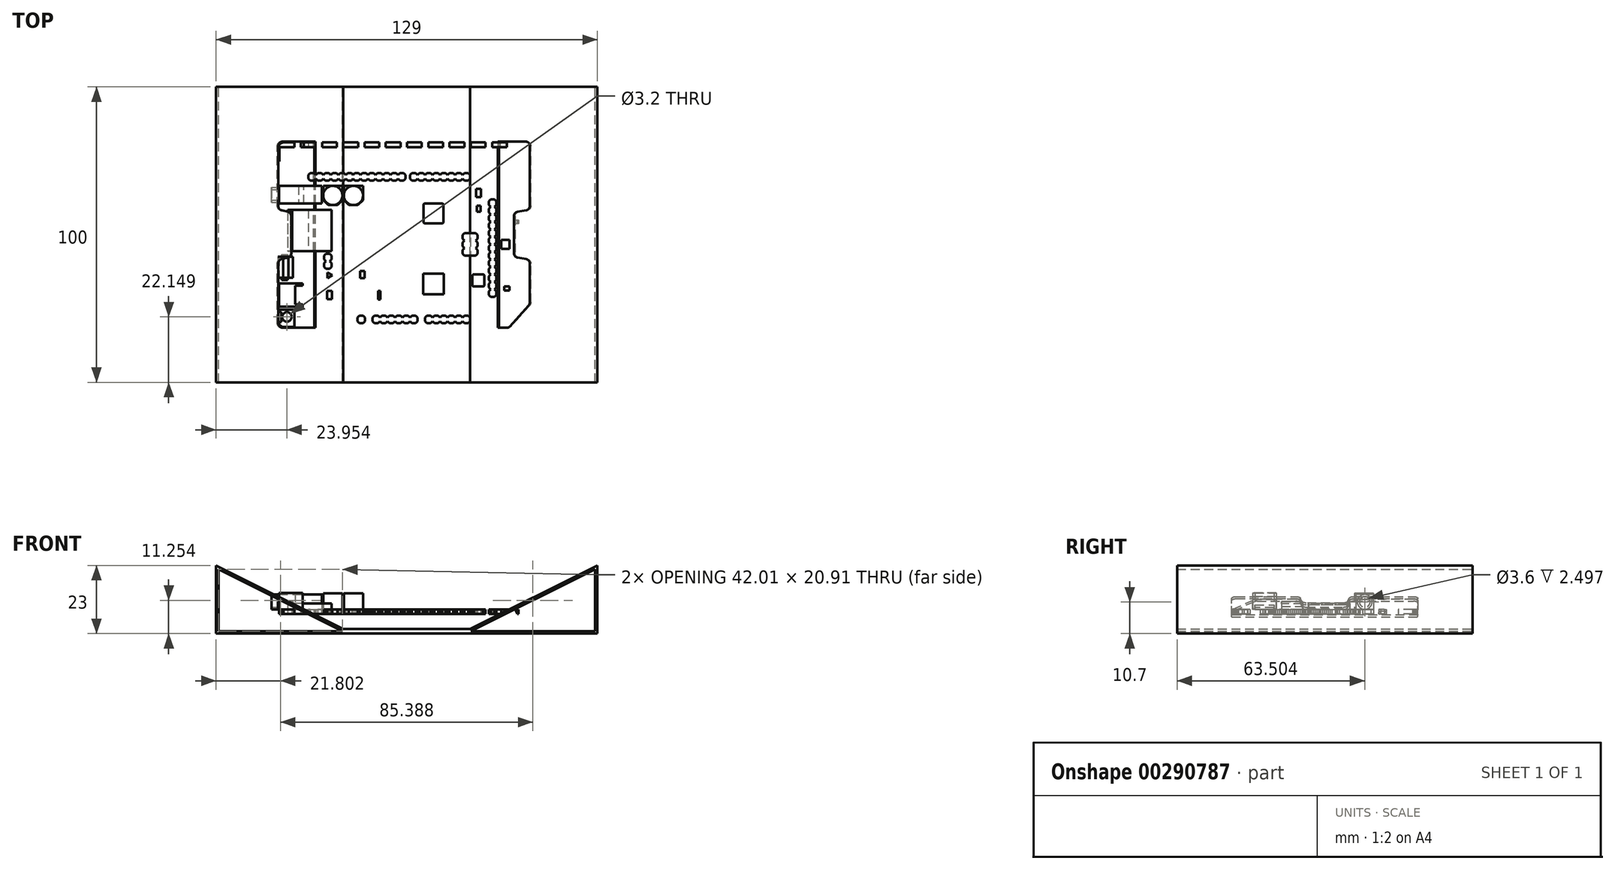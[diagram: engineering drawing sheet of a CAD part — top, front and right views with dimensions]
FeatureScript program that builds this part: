
annotation { "Feature Type Name" : "Feature", "Feature Type Description" : "" }
export const myFeature = defineFeature(function(context is Context, id is Id, definition is map)
    precondition{}
    {
        {
            var Q0;
            Q0=qCreatedBy(makeId("Top.planeOp"),FACE);
            var sketch = newSketch(context, id + "F0", { "sketchPlane" : qUnion([Q0])});
            skLineSegment(sketch, "E0", {"start": v(-41.68, 28.46) * mm, "end": v(-41.68, -30.97) * mm});
            skFitSpline(sketch, "E1", {"points": [v(-41.68, -30.97) * mm, v(-41.68, -31.8) * mm, v(-41.01, -32.47) * mm, v(-40.18, -32.47) * mm]});
            skLineSegment(sketch, "E2", {"start": v(-40.18, -32.47) * mm, "end": v(34.93, -32.47) * mm});
            skFitSpline(sketch, "E3", {"points": [v(-40.18, 29.96) * mm, v(-41.01, 29.96) * mm, v(-41.68, 29.29) * mm, v(-41.68, 28.46) * mm]});
            skLineSegment(sketch, "E4", {"start": v(-40.18, 29.96) * mm, "end": v(41.32, 29.96) * mm});
            skFitSpline(sketch, "E5", {"points": [v(42.82, 28.46) * mm, v(42.82, 29.29) * mm, v(42.15, 29.96) * mm, v(41.32, 29.96) * mm]});
            skLineSegment(sketch, "E6", {"start": v(42.82, 28.46) * mm, "end": v(42.82, -24.58) * mm});
            skLineSegment(sketch, "E7", {"start": v(42.82, -24.58) * mm, "end": v(34.93, -32.47) * mm});
            skLineSegment(sketch, "E8", {"start": v(-23.54, -14.96) * mm, "end": v(-25.32, -14.08) * mm});
            skLineSegment(sketch, "E9", {"start": v(-25.32, -14.08) * mm, "end": v(-25.32, -14.96) * mm});
            skLineSegment(sketch, "E10", {"start": v(-25.32, -14.96) * mm, "end": v(-25.32, -15.98) * mm});
            skLineSegment(sketch, "E11", {"start": v(-25.32, -15.98) * mm, "end": v(-23.54, -14.96) * mm});
            skLineSegment(sketch, "E12", {"start": v(-25.32, -14.96) * mm, "end": v(-25.95, -14.96) * mm});
            skLineSegment(sketch, "E13", {"start": v(-23.54, -14.96) * mm, "end": v(-23.16, -14.96) * mm});
            skLineSegment(sketch, "E14", {"start": v(-24.84, -27.62) * mm, "end": v(-24.35, -27.62) * mm});
            skLineSegment(sketch, "E15", {"start": v(-24.6, -27.38) * mm, "end": v(-24.6, -27.87) * mm});
            skLineSegment(sketch, "E16", {"start": v(-22.3, -27.62) * mm, "end": v(-21.8, -27.62) * mm});
            skLineSegment(sketch, "E17", {"start": v(-22.06, -27.38) * mm, "end": v(-22.06, -27.87) * mm});
            skLineSegment(sketch, "E18", {"start": v(-19.76, -27.62) * mm, "end": v(-19.27, -27.62) * mm});
            skLineSegment(sketch, "E19", {"start": v(-19.52, -27.38) * mm, "end": v(-19.52, -27.87) * mm});
            skLineSegment(sketch, "E20", {"start": v(-17.23, -27.62) * mm, "end": v(-16.74, -27.62) * mm});
            skLineSegment(sketch, "E21", {"start": v(-16.98, -27.38) * mm, "end": v(-16.98, -27.87) * mm});
            skLineSegment(sketch, "E22", {"start": v(-24.52, -31.43) * mm, "end": v(-24.03, -31.43) * mm});
            skLineSegment(sketch, "E23", {"start": v(-21.98, -31.43) * mm, "end": v(-21.5, -31.43) * mm});
            skLineSegment(sketch, "E24", {"start": v(-19.45, -31.43) * mm, "end": v(-18.96, -31.43) * mm});
            skLineSegment(sketch, "E25", {"start": v(-16.9, -31.43) * mm, "end": v(-16.42, -31.43) * mm});
            skLineSegment(sketch, "E26", {"start": v(-22.82, -17.79) * mm, "end": v(-22.33, -17.79) * mm});
            skLineSegment(sketch, "E27", {"start": v(-22.58, -17.54) * mm, "end": v(-22.58, -18.03) * mm});
            skLineSegment(sketch, "E28", {"start": v(-26.68, -17.86) * mm, "end": v(-26.19, -17.86) * mm});
            skLineSegment(sketch, "E29", {"start": v(-38.87, -9.81) * mm, "end": v(-38.5, -10.37) * mm});
            skLineSegment(sketch, "E30", {"start": v(-38.5, -9.81) * mm, "end": v(-38.87, -10.37) * mm});
            skLineSegment(sketch, "E31", {"start": v(-38.3, -10) * mm, "end": v(-38.12, -9.81) * mm});
            skLineSegment(sketch, "E32", {"start": v(-38.12, -9.81) * mm, "end": v(-38.12, -10.37) * mm});
            skLineSegment(sketch, "E33", {"start": v(-38.3, -10.37) * mm, "end": v(-37.93, -10.37) * mm});
            skLineSegment(sketch, "E34", {"start": v(19.2, -17.12) * mm, "end": v(19.2, -17.06) * mm});
            skLineSegment(sketch, "E35", {"start": v(4.38, -13) * mm, "end": v(4.38, -12.94) * mm});
            skLineSegment(sketch, "E36", {"start": v(13.53, -10.11) * mm, "end": v(13.47, -10.11) * mm});
            skLineSegment(sketch, "E37", {"start": v(8.14, -7.42) * mm, "end": v(8.08, -7.42) * mm});
            skLineSegment(sketch, "E38", {"start": v(15.4, -23.94) * mm, "end": v(15.4, -23.88) * mm});
            skLineSegment(sketch, "E39", {"start": v(19.2, -18.39) * mm, "end": v(19.2, -18.33) * mm});
            skLineSegment(sketch, "E40", {"start": v(5.89, -23.88) * mm, "end": v(5.89, -23.94) * mm});
            skLineSegment(sketch, "E41", {"start": v(-5.24, -16.93) * mm, "end": v(-5.18, -16.93) * mm});
            skLineSegment(sketch, "E42", {"start": v(17.9, -10.11) * mm, "end": v(17.97, -10.11) * mm});
            skLineSegment(sketch, "E43", {"start": v(-24.56, -19.44) * mm, "end": v(-24.56, -19.5) * mm});
            skLineSegment(sketch, "E44", {"start": v(1.13, 2.22) * mm, "end": v(1.13, 2.29) * mm});
            skLineSegment(sketch, "E45", {"start": v(1.13, 9.58) * mm, "end": v(1.13, 9.52) * mm});
            skLineSegment(sketch, "E46", {"start": v(39.79, -4.56) * mm, "end": v(39.85, -4.56) * mm});
            skLineSegment(sketch, "E47", {"start": v(37.1, -8.69) * mm, "end": v(37.15, -8.69) * mm});
            skLineSegment(sketch, "E48", {"start": v(18.57, 6.88) * mm, "end": v(18.57, 6.82) * mm});
            skLineSegment(sketch, "E49", {"start": v(29.67, 13.8) * mm, "end": v(29.67, 13.86) * mm});
            skLineSegment(sketch, "E50", {"start": v(21.1, 8.73) * mm, "end": v(21.1, 8.79) * mm});
            skLineSegment(sketch, "E51", {"start": v(21.1, 3.02) * mm, "end": v(21.1, 3.08) * mm});
            skLineSegment(sketch, "E52", {"start": v(25.86, 15.39) * mm, "end": v(25.86, 15.45) * mm});
            skLineSegment(sketch, "E53", {"start": v(25.86, 5.47) * mm, "end": v(25.86, 5.54) * mm});
            skLineSegment(sketch, "E54", {"start": v(3.95, 3.36) * mm, "end": v(4.01, 3.36) * mm});
            skLineSegment(sketch, "E55", {"start": v(10.61, -1.87) * mm, "end": v(10.67, -1.87) * mm});
            skLineSegment(sketch, "E56", {"start": v(3.95, 8.83) * mm, "end": v(4.01, 8.83) * mm});
            skLineSegment(sketch, "E57", {"start": v(18.57, 4.98) * mm, "end": v(18.57, 4.92) * mm});
            skLineSegment(sketch, "E58", {"start": v(-26.86, -14.03) * mm, "end": v(-26.86, -13.58) * mm});
            skLineSegment(sketch, "E59", {"start": v(-26.86, -13.58) * mm, "end": v(-22.26, -13.58) * mm});
            skLineSegment(sketch, "E60", {"start": v(-22.26, -13.58) * mm, "end": v(-22.26, -14.03) * mm});
            skLineSegment(sketch, "E61", {"start": v(-22.26, -16.03) * mm, "end": v(-22.26, -16.48) * mm});
            skLineSegment(sketch, "E62", {"start": v(-22.26, -16.48) * mm, "end": v(-26.86, -16.48) * mm});
            skLineSegment(sketch, "E63", {"start": v(-26.86, -16.48) * mm, "end": v(-26.86, -16.03) * mm});
            skLineSegment(sketch, "E64", {"start": v(-23.56, -14.03) * mm, "end": v(-23.56, -16.03) * mm});
            skLineSegment(sketch, "E65", {"start": v(-14.26, -15.9) * mm, "end": v(-14.26, -13.51) * mm});
            skLineSegment(sketch, "E66", {"start": v(-14.26, -13.51) * mm, "end": v(-12.66, -13.51) * mm});
            skLineSegment(sketch, "E67", {"start": v(-12.66, -13.51) * mm, "end": v(-12.66, -15.9) * mm});
            skLineSegment(sketch, "E68", {"start": v(-12.66, -15.9) * mm, "end": v(-14.26, -15.9) * mm});
            skLineSegment(sketch, "E69", {"start": v(-31.28, -12.8) * mm, "end": v(-31.28, -10.9) * mm});
            skLineSegment(sketch, "E70", {"start": v(-27.98, -12.8) * mm, "end": v(-27.98, -10.9) * mm});
            skLineSegment(sketch, "E71", {"start": v(-31.28, -12.75) * mm, "end": v(-31.28, -12.87) * mm});
            skLineSegment(sketch, "E72", {"start": v(-31.28, -12.87) * mm, "end": v(-31.03, -12.87) * mm});
            skLineSegment(sketch, "E73", {"start": v(-31.28, -10.97) * mm, "end": v(-31.28, -10.84) * mm});
            skLineSegment(sketch, "E74", {"start": v(-31.28, -10.84) * mm, "end": v(-31.03, -10.84) * mm});
            skLineSegment(sketch, "E75", {"start": v(-27.98, -12.75) * mm, "end": v(-27.98, -12.87) * mm});
            skLineSegment(sketch, "E76", {"start": v(-27.98, -12.87) * mm, "end": v(-28.24, -12.87) * mm});
            skLineSegment(sketch, "E77", {"start": v(-27.98, -10.97) * mm, "end": v(-27.98, -10.84) * mm});
            skLineSegment(sketch, "E78", {"start": v(-27.98, -10.84) * mm, "end": v(-28.24, -10.84) * mm});
            skLineSegment(sketch, "E79", {"start": v(-6.13, -15.63) * mm, "end": v(-6.13, -18.23) * mm});
            skLineSegment(sketch, "E80", {"start": v(-9.37, -18.23) * mm, "end": v(-9.37, -15.63) * mm});
            skFitSpline(sketch, "E81", {"points": [v(-6.13, -15.63) * mm, v(-6.13, -15.45) * mm, v(-6.27, -15.3) * mm, v(-6.45, -15.3) * mm]});
            skFitSpline(sketch, "E82", {"points": [v(-9.05, -15.3) * mm, v(-9.23, -15.3) * mm, v(-9.37, -15.45) * mm, v(-9.37, -15.63) * mm]});
            skFitSpline(sketch, "E83", {"points": [v(-9.37, -18.23) * mm, v(-9.37, -18.4) * mm, v(-9.23, -18.56) * mm, v(-9.05, -18.56) * mm]});
            skFitSpline(sketch, "E84", {"points": [v(-6.45, -18.56) * mm, v(-6.27, -18.56) * mm, v(-6.13, -18.4) * mm, v(-6.13, -18.23) * mm]});
            skLineSegment(sketch, "E85", {"start": v(-24.13, -23.1) * mm, "end": v(-24.99, -23.1) * mm});
            skLineSegment(sketch, "E86", {"start": v(-24.99, -20.27) * mm, "end": v(-24.13, -20.27) * mm});
            skLineSegment(sketch, "E87", {"start": v(-23.75, -21.42) * mm, "end": v(-23.75, -21.96) * mm});
            skLineSegment(sketch, "E88", {"start": v(-16.63, 2.1) * mm, "end": v(-20.44, 2.1) * mm});
            skLineSegment(sketch, "E89", {"start": v(-16.63, -2.98) * mm, "end": v(-20.44, -2.98) * mm});
            skLineSegment(sketch, "E90", {"start": v(-16.63, 2.1) * mm, "end": v(-16.63, 1.78) * mm});
            skLineSegment(sketch, "E91", {"start": v(-20.44, 2.1) * mm, "end": v(-20.44, 1.78) * mm});
            skLineSegment(sketch, "E92", {"start": v(-16.63, -2.98) * mm, "end": v(-16.63, -2.66) * mm});
            skLineSegment(sketch, "E93", {"start": v(-20.44, -2.98) * mm, "end": v(-20.44, -2.66) * mm});
            skLineSegment(sketch, "E94", {"start": v(36.56, -5.56) * mm, "end": v(36.56, -6.06) * mm});
            skLineSegment(sketch, "E95", {"start": v(36.56, -6.06) * mm, "end": v(36.06, -6.06) * mm});
            skLineSegment(sketch, "E96", {"start": v(33.56, -6.06) * mm, "end": v(34.06, -6.06) * mm});
            skLineSegment(sketch, "E97", {"start": v(36.56, -3.07) * mm, "end": v(36.06, -3.07) * mm});
            skLineSegment(sketch, "E98", {"start": v(33.56, -3.07) * mm, "end": v(34.06, -3.07) * mm});
            skLineSegment(sketch, "E99", {"start": v(33.56, -5.56) * mm, "end": v(33.56, -6.06) * mm});
            skLineSegment(sketch, "E100", {"start": v(33.56, -3.56) * mm, "end": v(33.56, -3.07) * mm});
            skLineSegment(sketch, "E101", {"start": v(36.56, -3.56) * mm, "end": v(36.56, -3.07) * mm});
            skLineSegment(sketch, "E102", {"start": v(25.44, 14.3) * mm, "end": v(26.3, 14.3) * mm});
            skLineSegment(sketch, "E103", {"start": v(26.3, 11.46) * mm, "end": v(25.44, 11.46) * mm});
            skLineSegment(sketch, "E104", {"start": v(25.06, 12.61) * mm, "end": v(25.06, 13.15) * mm});
            skLineSegment(sketch, "E105", {"start": v(21.1, -0.76) * mm, "end": v(20.47, -1.4) * mm});
            skLineSegment(sketch, "E106", {"start": v(20.47, -2.66) * mm, "end": v(21.1, -3.3) * mm});
            skLineSegment(sketch, "E107", {"start": v(21.1, -3.3) * mm, "end": v(20.47, -3.93) * mm});
            skLineSegment(sketch, "E108", {"start": v(20.47, -5.2) * mm, "end": v(21.1, -5.83) * mm});
            skLineSegment(sketch, "E109", {"start": v(21.1, -0.76) * mm, "end": v(24.91, -0.76) * mm});
            skLineSegment(sketch, "E110", {"start": v(24.91, -0.76) * mm, "end": v(25.55, -1.4) * mm});
            skLineSegment(sketch, "E111", {"start": v(25.55, -1.4) * mm, "end": v(25.55, -2.66) * mm});
            skLineSegment(sketch, "E112", {"start": v(25.55, -2.66) * mm, "end": v(24.91, -3.3) * mm});
            skLineSegment(sketch, "E113", {"start": v(24.91, -3.3) * mm, "end": v(25.55, -3.93) * mm});
            skLineSegment(sketch, "E114", {"start": v(25.55, -3.93) * mm, "end": v(25.55, -5.2) * mm});
            skLineSegment(sketch, "E115", {"start": v(25.55, -5.2) * mm, "end": v(24.91, -5.83) * mm});
            skLineSegment(sketch, "E116", {"start": v(24.91, -3.3) * mm, "end": v(21.1, -3.3) * mm});
            skLineSegment(sketch, "E117", {"start": v(24.91, -5.83) * mm, "end": v(21.1, -5.83) * mm});
            skLineSegment(sketch, "E118", {"start": v(20.47, -3.93) * mm, "end": v(20.47, -5.2) * mm});
            skLineSegment(sketch, "E119", {"start": v(20.47, -1.4) * mm, "end": v(20.47, -2.66) * mm});
            skLineSegment(sketch, "E120", {"start": v(21.1, -5.83) * mm, "end": v(20.47, -6.47) * mm});
            skLineSegment(sketch, "E121", {"start": v(20.47, -7.73) * mm, "end": v(21.1, -8.37) * mm});
            skLineSegment(sketch, "E122", {"start": v(24.91, -5.83) * mm, "end": v(25.55, -6.47) * mm});
            skLineSegment(sketch, "E123", {"start": v(25.55, -6.47) * mm, "end": v(25.55, -7.73) * mm});
            skLineSegment(sketch, "E124", {"start": v(25.55, -7.73) * mm, "end": v(24.91, -8.37) * mm});
            skLineSegment(sketch, "E125", {"start": v(24.91, -8.37) * mm, "end": v(21.1, -8.37) * mm});
            skLineSegment(sketch, "E126", {"start": v(20.47, -6.47) * mm, "end": v(20.47, -7.73) * mm});
            skLineSegment(sketch, "E127", {"start": v(0.81, -28.66) * mm, "end": v(2.08, -28.66) * mm});
            skLineSegment(sketch, "E128", {"start": v(2.08, -28.66) * mm, "end": v(2.71, -29.3) * mm});
            skLineSegment(sketch, "E129", {"start": v(2.71, -29.3) * mm, "end": v(2.71, -30.57) * mm});
            skLineSegment(sketch, "E130", {"start": v(2.71, -30.57) * mm, "end": v(2.08, -31.2) * mm});
            skLineSegment(sketch, "E131", {"start": v(-2.36, -29.3) * mm, "end": v(-1.73, -28.66) * mm});
            skLineSegment(sketch, "E132", {"start": v(-1.73, -28.66) * mm, "end": v(-0.46, -28.66) * mm});
            skLineSegment(sketch, "E133", {"start": v(-0.46, -28.66) * mm, "end": v(0.18, -29.3) * mm});
            skLineSegment(sketch, "E134", {"start": v(0.18, -29.3) * mm, "end": v(0.18, -30.57) * mm});
            skLineSegment(sketch, "E135", {"start": v(0.18, -30.57) * mm, "end": v(-0.46, -31.2) * mm});
            skLineSegment(sketch, "E136", {"start": v(-0.46, -31.2) * mm, "end": v(-1.73, -31.2) * mm});
            skLineSegment(sketch, "E137", {"start": v(-1.73, -31.2) * mm, "end": v(-2.36, -30.57) * mm});
            skLineSegment(sketch, "E138", {"start": v(0.81, -28.66) * mm, "end": v(0.18, -29.3) * mm});
            skLineSegment(sketch, "E139", {"start": v(0.18, -30.57) * mm, "end": v(0.81, -31.2) * mm});
            skLineSegment(sketch, "E140", {"start": v(2.08, -31.2) * mm, "end": v(0.81, -31.2) * mm});
            skLineSegment(sketch, "E141", {"start": v(-6.8, -28.66) * mm, "end": v(-5.53, -28.66) * mm});
            skLineSegment(sketch, "E142", {"start": v(-5.53, -28.66) * mm, "end": v(-4.9, -29.3) * mm});
            skLineSegment(sketch, "E143", {"start": v(-4.9, -29.3) * mm, "end": v(-4.9, -30.57) * mm});
            skLineSegment(sketch, "E144", {"start": v(-4.9, -30.57) * mm, "end": v(-5.53, -31.2) * mm});
            skLineSegment(sketch, "E145", {"start": v(-4.9, -29.3) * mm, "end": v(-4.26, -28.66) * mm});
            skLineSegment(sketch, "E146", {"start": v(-4.26, -28.66) * mm, "end": v(-3, -28.66) * mm});
            skLineSegment(sketch, "E147", {"start": v(-3, -28.66) * mm, "end": v(-2.36, -29.3) * mm});
            skLineSegment(sketch, "E148", {"start": v(-2.36, -29.3) * mm, "end": v(-2.36, -30.57) * mm});
            skLineSegment(sketch, "E149", {"start": v(-2.36, -30.57) * mm, "end": v(-3, -31.2) * mm});
            skLineSegment(sketch, "E150", {"start": v(-3, -31.2) * mm, "end": v(-4.26, -31.2) * mm});
            skLineSegment(sketch, "E151", {"start": v(-4.26, -31.2) * mm, "end": v(-4.9, -30.57) * mm});
            skLineSegment(sketch, "E152", {"start": v(-9.97, -29.3) * mm, "end": v(-9.34, -28.66) * mm});
            skLineSegment(sketch, "E153", {"start": v(-9.34, -28.66) * mm, "end": v(-8.07, -28.66) * mm});
            skLineSegment(sketch, "E154", {"start": v(-8.07, -28.66) * mm, "end": v(-7.43, -29.3) * mm});
            skLineSegment(sketch, "E155", {"start": v(-7.43, -29.3) * mm, "end": v(-7.43, -30.57) * mm});
            skLineSegment(sketch, "E156", {"start": v(-7.43, -30.57) * mm, "end": v(-8.07, -31.2) * mm});
            skLineSegment(sketch, "E157", {"start": v(-8.07, -31.2) * mm, "end": v(-9.34, -31.2) * mm});
            skLineSegment(sketch, "E158", {"start": v(-9.34, -31.2) * mm, "end": v(-9.97, -30.57) * mm});
            skLineSegment(sketch, "E159", {"start": v(-6.8, -28.66) * mm, "end": v(-7.43, -29.3) * mm});
            skLineSegment(sketch, "E160", {"start": v(-7.43, -30.57) * mm, "end": v(-6.8, -31.2) * mm});
            skLineSegment(sketch, "E161", {"start": v(-5.53, -31.2) * mm, "end": v(-6.8, -31.2) * mm});
            skLineSegment(sketch, "E162", {"start": v(-14.41, -28.66) * mm, "end": v(-13.14, -28.66) * mm});
            skLineSegment(sketch, "E163", {"start": v(-13.14, -28.66) * mm, "end": v(-12.5, -29.3) * mm});
            skLineSegment(sketch, "E164", {"start": v(-12.5, -29.3) * mm, "end": v(-12.5, -30.57) * mm});
            skLineSegment(sketch, "E165", {"start": v(-12.5, -30.57) * mm, "end": v(-13.14, -31.2) * mm});
            skLineSegment(sketch, "E166", {"start": v(-12.5, -29.3) * mm, "end": v(-11.87, -28.66) * mm});
            skLineSegment(sketch, "E167", {"start": v(-11.87, -28.66) * mm, "end": v(-10.6, -28.66) * mm});
            skLineSegment(sketch, "E168", {"start": v(-10.6, -28.66) * mm, "end": v(-9.97, -29.3) * mm});
            skLineSegment(sketch, "E169", {"start": v(-9.97, -29.3) * mm, "end": v(-9.97, -30.57) * mm});
            skLineSegment(sketch, "E170", {"start": v(-10.66, -30.05) * mm, "end": v(-11.3, -30.68) * mm});
            skLineSegment(sketch, "E171", {"start": v(-10.6, -31.2) * mm, "end": v(-11.87, -31.2) * mm});
            skLineSegment(sketch, "E172", {"start": v(-11.87, -31.2) * mm, "end": v(-12.5, -30.57) * mm});
            skLineSegment(sketch, "E173", {"start": v(-15.04, -29.3) * mm, "end": v(-15.04, -30.57) * mm});
            skLineSegment(sketch, "E174", {"start": v(-14.41, -28.66) * mm, "end": v(-15.04, -29.3) * mm});
            skLineSegment(sketch, "E175", {"start": v(-15.04, -30.57) * mm, "end": v(-14.41, -31.2) * mm});
            skLineSegment(sketch, "E176", {"start": v(-13.14, -31.2) * mm, "end": v(-14.41, -31.2) * mm});
            skLineSegment(sketch, "E177", {"start": v(3.35, -28.66) * mm, "end": v(4.62, -28.66) * mm});
            skLineSegment(sketch, "E178", {"start": v(4.62, -28.66) * mm, "end": v(5.25, -29.3) * mm});
            skLineSegment(sketch, "E179", {"start": v(5.25, -29.3) * mm, "end": v(5.25, -30.57) * mm});
            skLineSegment(sketch, "E180", {"start": v(5.25, -30.57) * mm, "end": v(4.62, -31.2) * mm});
            skLineSegment(sketch, "E181", {"start": v(3.35, -28.66) * mm, "end": v(2.71, -29.3) * mm});
            skLineSegment(sketch, "E182", {"start": v(2.71, -30.57) * mm, "end": v(3.35, -31.2) * mm});
            skLineSegment(sketch, "E183", {"start": v(4.62, -31.2) * mm, "end": v(3.35, -31.2) * mm});
            skLineSegment(sketch, "E184", {"start": v(16.03, -28.66) * mm, "end": v(17.3, -28.66) * mm});
            skLineSegment(sketch, "E185", {"start": v(17.3, -28.66) * mm, "end": v(17.94, -29.3) * mm});
            skLineSegment(sketch, "E186", {"start": v(17.94, -29.3) * mm, "end": v(17.94, -30.57) * mm});
            skLineSegment(sketch, "E187", {"start": v(17.94, -30.57) * mm, "end": v(17.3, -31.2) * mm});
            skLineSegment(sketch, "E188", {"start": v(17.94, -29.3) * mm, "end": v(18.57, -28.66) * mm});
            skLineSegment(sketch, "E189", {"start": v(18.57, -28.66) * mm, "end": v(19.84, -28.66) * mm});
            skLineSegment(sketch, "E190", {"start": v(19.84, -28.66) * mm, "end": v(20.47, -29.3) * mm});
            skLineSegment(sketch, "E191", {"start": v(20.47, -29.3) * mm, "end": v(20.47, -30.57) * mm});
            skLineSegment(sketch, "E192", {"start": v(20.47, -30.57) * mm, "end": v(19.84, -31.2) * mm});
            skLineSegment(sketch, "E193", {"start": v(19.84, -31.2) * mm, "end": v(18.57, -31.2) * mm});
            skLineSegment(sketch, "E194", {"start": v(18.57, -31.2) * mm, "end": v(17.94, -30.57) * mm});
            skLineSegment(sketch, "E195", {"start": v(12.86, -29.3) * mm, "end": v(13.5, -28.66) * mm});
            skLineSegment(sketch, "E196", {"start": v(13.5, -28.66) * mm, "end": v(14.77, -28.66) * mm});
            skLineSegment(sketch, "E197", {"start": v(14.77, -28.66) * mm, "end": v(15.4, -29.3) * mm});
            skLineSegment(sketch, "E198", {"start": v(15.4, -29.3) * mm, "end": v(15.4, -30.57) * mm});
            skLineSegment(sketch, "E199", {"start": v(15.4, -30.57) * mm, "end": v(14.77, -31.2) * mm});
            skLineSegment(sketch, "E200", {"start": v(14.77, -31.2) * mm, "end": v(13.5, -31.2) * mm});
            skLineSegment(sketch, "E201", {"start": v(13.5, -31.2) * mm, "end": v(12.86, -30.57) * mm});
            skLineSegment(sketch, "E202", {"start": v(16.03, -28.66) * mm, "end": v(15.4, -29.3) * mm});
            skLineSegment(sketch, "E203", {"start": v(15.4, -30.57) * mm, "end": v(16.03, -31.2) * mm});
            skLineSegment(sketch, "E204", {"start": v(17.3, -31.2) * mm, "end": v(16.03, -31.2) * mm});
            skLineSegment(sketch, "E205", {"start": v(8.42, -28.66) * mm, "end": v(9.7, -28.66) * mm});
            skLineSegment(sketch, "E206", {"start": v(9.7, -28.66) * mm, "end": v(10.33, -29.3) * mm});
            skLineSegment(sketch, "E207", {"start": v(10.33, -29.3) * mm, "end": v(10.33, -30.57) * mm});
            skLineSegment(sketch, "E208", {"start": v(10.33, -30.57) * mm, "end": v(9.7, -31.2) * mm});
            skLineSegment(sketch, "E209", {"start": v(10.33, -29.3) * mm, "end": v(10.96, -28.66) * mm});
            skLineSegment(sketch, "E210", {"start": v(10.96, -28.66) * mm, "end": v(12.23, -28.66) * mm});
            skLineSegment(sketch, "E211", {"start": v(12.23, -28.66) * mm, "end": v(12.86, -29.3) * mm});
            skLineSegment(sketch, "E212", {"start": v(12.86, -29.3) * mm, "end": v(12.86, -30.57) * mm});
            skLineSegment(sketch, "E213", {"start": v(12.86, -30.57) * mm, "end": v(12.23, -31.2) * mm});
            skLineSegment(sketch, "E214", {"start": v(12.23, -31.2) * mm, "end": v(10.96, -31.2) * mm});
            skLineSegment(sketch, "E215", {"start": v(10.96, -31.2) * mm, "end": v(10.33, -30.57) * mm});
            skLineSegment(sketch, "E216", {"start": v(7.79, -29.3) * mm, "end": v(7.79, -30.57) * mm});
            skLineSegment(sketch, "E217", {"start": v(8.42, -28.66) * mm, "end": v(7.79, -29.3) * mm});
            skLineSegment(sketch, "E218", {"start": v(7.79, -30.57) * mm, "end": v(8.42, -31.2) * mm});
            skLineSegment(sketch, "E219", {"start": v(9.7, -31.2) * mm, "end": v(8.42, -31.2) * mm});
            skLineSegment(sketch, "E220", {"start": v(21.1, -28.66) * mm, "end": v(22.38, -28.66) * mm});
            skLineSegment(sketch, "E221", {"start": v(22.38, -28.66) * mm, "end": v(23.01, -29.3) * mm});
            skLineSegment(sketch, "E222", {"start": v(23.01, -29.3) * mm, "end": v(23.01, -30.57) * mm});
            skLineSegment(sketch, "E223", {"start": v(23.01, -30.57) * mm, "end": v(22.38, -31.2) * mm});
            skLineSegment(sketch, "E224", {"start": v(21.1, -28.66) * mm, "end": v(20.47, -29.3) * mm});
            skLineSegment(sketch, "E225", {"start": v(20.47, -30.57) * mm, "end": v(21.1, -31.2) * mm});
            skLineSegment(sketch, "E226", {"start": v(22.38, -31.2) * mm, "end": v(21.1, -31.2) * mm});
            skLineSegment(sketch, "E227", {"start": v(7.15, 17) * mm, "end": v(5.89, 17) * mm});
            skLineSegment(sketch, "E228", {"start": v(5.89, 17) * mm, "end": v(5.25, 17.64) * mm});
            skLineSegment(sketch, "E229", {"start": v(5.25, 17.64) * mm, "end": v(5.25, 18.9) * mm});
            skLineSegment(sketch, "E230", {"start": v(5.25, 18.9) * mm, "end": v(5.89, 19.54) * mm});
            skLineSegment(sketch, "E231", {"start": v(10.33, 17.64) * mm, "end": v(9.7, 17) * mm});
            skLineSegment(sketch, "E232", {"start": v(9.7, 17) * mm, "end": v(8.42, 17) * mm});
            skLineSegment(sketch, "E233", {"start": v(8.42, 17) * mm, "end": v(7.79, 17.64) * mm});
            skLineSegment(sketch, "E234", {"start": v(7.79, 17.64) * mm, "end": v(7.79, 18.9) * mm});
            skLineSegment(sketch, "E235", {"start": v(7.79, 18.9) * mm, "end": v(8.42, 19.54) * mm});
            skLineSegment(sketch, "E236", {"start": v(8.42, 19.54) * mm, "end": v(9.7, 19.54) * mm});
            skLineSegment(sketch, "E237", {"start": v(9.7, 19.54) * mm, "end": v(10.33, 18.9) * mm});
            skLineSegment(sketch, "E238", {"start": v(7.15, 17) * mm, "end": v(7.79, 17.64) * mm});
            skLineSegment(sketch, "E239", {"start": v(7.79, 18.9) * mm, "end": v(7.15, 19.54) * mm});
            skLineSegment(sketch, "E240", {"start": v(5.89, 19.54) * mm, "end": v(7.15, 19.54) * mm});
            skLineSegment(sketch, "E241", {"start": v(14.77, 17) * mm, "end": v(13.5, 17) * mm});
            skLineSegment(sketch, "E242", {"start": v(13.5, 17) * mm, "end": v(12.86, 17.64) * mm});
            skLineSegment(sketch, "E243", {"start": v(12.86, 17.64) * mm, "end": v(12.86, 18.9) * mm});
            skLineSegment(sketch, "E244", {"start": v(12.86, 18.9) * mm, "end": v(13.5, 19.54) * mm});
            skLineSegment(sketch, "E245", {"start": v(12.86, 17.64) * mm, "end": v(12.23, 17) * mm});
            skLineSegment(sketch, "E246", {"start": v(12.23, 17) * mm, "end": v(10.96, 17) * mm});
            skLineSegment(sketch, "E247", {"start": v(10.96, 17) * mm, "end": v(10.33, 17.64) * mm});
            skLineSegment(sketch, "E248", {"start": v(10.33, 17.64) * mm, "end": v(10.33, 18.9) * mm});
            skLineSegment(sketch, "E249", {"start": v(10.33, 18.9) * mm, "end": v(10.96, 19.54) * mm});
            skLineSegment(sketch, "E250", {"start": v(10.96, 19.54) * mm, "end": v(12.23, 19.54) * mm});
            skLineSegment(sketch, "E251", {"start": v(12.23, 19.54) * mm, "end": v(12.86, 18.9) * mm});
            skLineSegment(sketch, "E252", {"start": v(17.94, 17.64) * mm, "end": v(17.3, 17) * mm});
            skLineSegment(sketch, "E253", {"start": v(17.3, 17) * mm, "end": v(16.03, 17) * mm});
            skLineSegment(sketch, "E254", {"start": v(16.03, 17) * mm, "end": v(15.4, 17.64) * mm});
            skLineSegment(sketch, "E255", {"start": v(15.4, 17.64) * mm, "end": v(15.4, 18.9) * mm});
            skLineSegment(sketch, "E256", {"start": v(15.4, 18.9) * mm, "end": v(16.03, 19.54) * mm});
            skLineSegment(sketch, "E257", {"start": v(16.03, 19.54) * mm, "end": v(17.3, 19.54) * mm});
            skLineSegment(sketch, "E258", {"start": v(17.3, 19.54) * mm, "end": v(17.94, 18.9) * mm});
            skLineSegment(sketch, "E259", {"start": v(14.77, 17) * mm, "end": v(15.4, 17.64) * mm});
            skLineSegment(sketch, "E260", {"start": v(15.4, 18.9) * mm, "end": v(14.77, 19.54) * mm});
            skLineSegment(sketch, "E261", {"start": v(13.5, 19.54) * mm, "end": v(14.77, 19.54) * mm});
            skLineSegment(sketch, "E262", {"start": v(22.38, 17) * mm, "end": v(21.1, 17) * mm});
            skLineSegment(sketch, "E263", {"start": v(21.1, 17) * mm, "end": v(20.47, 17.64) * mm});
            skLineSegment(sketch, "E264", {"start": v(20.47, 17.64) * mm, "end": v(20.47, 18.9) * mm});
            skLineSegment(sketch, "E265", {"start": v(20.47, 18.9) * mm, "end": v(21.1, 19.54) * mm});
            skLineSegment(sketch, "E266", {"start": v(20.47, 17.64) * mm, "end": v(19.84, 17) * mm});
            skLineSegment(sketch, "E267", {"start": v(19.84, 17) * mm, "end": v(18.57, 17) * mm});
            skLineSegment(sketch, "E268", {"start": v(18.57, 17) * mm, "end": v(17.94, 17.64) * mm});
            skLineSegment(sketch, "E269", {"start": v(17.94, 17.64) * mm, "end": v(17.94, 18.9) * mm});
            skLineSegment(sketch, "E270", {"start": v(17.94, 18.9) * mm, "end": v(18.57, 19.54) * mm});
            skLineSegment(sketch, "E271", {"start": v(18.57, 19.54) * mm, "end": v(19.84, 19.54) * mm});
            skLineSegment(sketch, "E272", {"start": v(19.84, 19.54) * mm, "end": v(20.47, 18.9) * mm});
            skLineSegment(sketch, "E273", {"start": v(23.01, 17.64) * mm, "end": v(23.01, 18.9) * mm});
            skLineSegment(sketch, "E274", {"start": v(22.38, 17) * mm, "end": v(23.01, 17.64) * mm});
            skLineSegment(sketch, "E275", {"start": v(23.01, 18.9) * mm, "end": v(22.38, 19.54) * mm});
            skLineSegment(sketch, "E276", {"start": v(21.1, 19.54) * mm, "end": v(22.38, 19.54) * mm});
            skLineSegment(sketch, "E277", {"start": v(4.62, 17) * mm, "end": v(3.35, 17) * mm});
            skLineSegment(sketch, "E278", {"start": v(3.35, 17) * mm, "end": v(2.71, 17.64) * mm});
            skLineSegment(sketch, "E279", {"start": v(2.71, 17.64) * mm, "end": v(2.71, 18.9) * mm});
            skLineSegment(sketch, "E280", {"start": v(2.71, 18.9) * mm, "end": v(3.35, 19.54) * mm});
            skLineSegment(sketch, "E281", {"start": v(4.62, 17) * mm, "end": v(5.25, 17.64) * mm});
            skLineSegment(sketch, "E282", {"start": v(5.25, 18.9) * mm, "end": v(4.62, 19.54) * mm});
            skLineSegment(sketch, "E283", {"start": v(3.35, 19.54) * mm, "end": v(4.62, 19.54) * mm});
            skLineSegment(sketch, "E284", {"start": v(-26.46, -12.17) * mm, "end": v(-26.46, -10.9) * mm});
            skLineSegment(sketch, "E285", {"start": v(-26.46, -10.9) * mm, "end": v(-25.83, -10.27) * mm});
            skLineSegment(sketch, "E286", {"start": v(-24.56, -10.27) * mm, "end": v(-23.92, -10.9) * mm});
            skLineSegment(sketch, "E287", {"start": v(-25.83, -10.27) * mm, "end": v(-26.46, -9.64) * mm});
            skLineSegment(sketch, "E288", {"start": v(-26.46, -9.64) * mm, "end": v(-26.46, -8.37) * mm});
            skLineSegment(sketch, "E289", {"start": v(-26.46, -8.37) * mm, "end": v(-25.83, -7.73) * mm});
            skLineSegment(sketch, "E290", {"start": v(-24.56, -7.73) * mm, "end": v(-23.92, -8.37) * mm});
            skLineSegment(sketch, "E291", {"start": v(-23.92, -8.37) * mm, "end": v(-23.92, -9.64) * mm});
            skLineSegment(sketch, "E292", {"start": v(-23.92, -9.64) * mm, "end": v(-24.56, -10.27) * mm});
            skLineSegment(sketch, "E293", {"start": v(-25.83, -12.8) * mm, "end": v(-24.56, -12.8) * mm});
            skLineSegment(sketch, "E294", {"start": v(-26.46, -12.17) * mm, "end": v(-25.83, -12.8) * mm});
            skLineSegment(sketch, "E295", {"start": v(-24.56, -12.8) * mm, "end": v(-23.92, -12.17) * mm});
            skLineSegment(sketch, "E296", {"start": v(-23.92, -10.9) * mm, "end": v(-23.92, -12.17) * mm});
            skLineSegment(sketch, "E297", {"start": v(-25.83, -7.73) * mm, "end": v(-24.56, -7.73) * mm});
            skLineSegment(sketch, "E298", {"start": v(-19.1, 17.64) * mm, "end": v(-19.74, 17) * mm});
            skLineSegment(sketch, "E299", {"start": v(-19.74, 17) * mm, "end": v(-21, 17) * mm});
            skLineSegment(sketch, "E300", {"start": v(-21, 17) * mm, "end": v(-21.64, 17.64) * mm});
            skLineSegment(sketch, "E301", {"start": v(-21.64, 17.64) * mm, "end": v(-21.64, 18.9) * mm});
            skLineSegment(sketch, "E302", {"start": v(-21.64, 18.9) * mm, "end": v(-21, 19.54) * mm});
            skLineSegment(sketch, "E303", {"start": v(-21, 19.54) * mm, "end": v(-19.74, 19.54) * mm});
            skLineSegment(sketch, "E304", {"start": v(-19.74, 19.54) * mm, "end": v(-19.1, 18.9) * mm});
            skLineSegment(sketch, "E305", {"start": v(-14.66, 17) * mm, "end": v(-15.93, 17) * mm});
            skLineSegment(sketch, "E306", {"start": v(-15.93, 17) * mm, "end": v(-16.57, 17.64) * mm});
            skLineSegment(sketch, "E307", {"start": v(-16.57, 17.64) * mm, "end": v(-16.57, 18.9) * mm});
            skLineSegment(sketch, "E308", {"start": v(-16.57, 18.9) * mm, "end": v(-15.93, 19.54) * mm});
            skLineSegment(sketch, "E309", {"start": v(-16.57, 17.64) * mm, "end": v(-17.2, 17) * mm});
            skLineSegment(sketch, "E310", {"start": v(-17.2, 17) * mm, "end": v(-18.47, 17) * mm});
            skLineSegment(sketch, "E311", {"start": v(-18.47, 17) * mm, "end": v(-19.1, 17.64) * mm});
            skLineSegment(sketch, "E312", {"start": v(-19.1, 17.64) * mm, "end": v(-19.1, 18.9) * mm});
            skLineSegment(sketch, "E313", {"start": v(-19.1, 18.9) * mm, "end": v(-18.47, 19.54) * mm});
            skLineSegment(sketch, "E314", {"start": v(-18.47, 19.54) * mm, "end": v(-17.2, 19.54) * mm});
            skLineSegment(sketch, "E315", {"start": v(-17.2, 19.54) * mm, "end": v(-16.57, 18.9) * mm});
            skLineSegment(sketch, "E316", {"start": v(-11.5, 17.64) * mm, "end": v(-12.13, 17) * mm});
            skLineSegment(sketch, "E317", {"start": v(-12.13, 17) * mm, "end": v(-13.4, 17) * mm});
            skLineSegment(sketch, "E318", {"start": v(-13.4, 17) * mm, "end": v(-14.03, 17.64) * mm});
            skLineSegment(sketch, "E319", {"start": v(-14.03, 17.64) * mm, "end": v(-14.03, 18.9) * mm});
            skLineSegment(sketch, "E320", {"start": v(-14.03, 18.9) * mm, "end": v(-13.4, 19.54) * mm});
            skLineSegment(sketch, "E321", {"start": v(-13.4, 19.54) * mm, "end": v(-12.13, 19.54) * mm});
            skLineSegment(sketch, "E322", {"start": v(-12.13, 19.54) * mm, "end": v(-11.5, 18.9) * mm});
            skLineSegment(sketch, "E323", {"start": v(-14.66, 17) * mm, "end": v(-14.03, 17.64) * mm});
            skLineSegment(sketch, "E324", {"start": v(-14.03, 18.9) * mm, "end": v(-14.66, 19.54) * mm});
            skLineSegment(sketch, "E325", {"start": v(-15.93, 19.54) * mm, "end": v(-14.66, 19.54) * mm});
            skLineSegment(sketch, "E326", {"start": v(-7.05, 17) * mm, "end": v(-8.32, 17) * mm});
            skLineSegment(sketch, "E327", {"start": v(-8.32, 17) * mm, "end": v(-8.96, 17.64) * mm});
            skLineSegment(sketch, "E328", {"start": v(-8.96, 17.64) * mm, "end": v(-8.96, 18.9) * mm});
            skLineSegment(sketch, "E329", {"start": v(-8.96, 18.9) * mm, "end": v(-8.32, 19.54) * mm});
            skLineSegment(sketch, "E330", {"start": v(-8.96, 17.64) * mm, "end": v(-9.6, 17) * mm});
            skLineSegment(sketch, "E331", {"start": v(-9.6, 17) * mm, "end": v(-10.86, 17) * mm});
            skLineSegment(sketch, "E332", {"start": v(-10.86, 17) * mm, "end": v(-11.5, 17.64) * mm});
            skLineSegment(sketch, "E333", {"start": v(-11.5, 17.64) * mm, "end": v(-11.5, 18.9) * mm});
            skLineSegment(sketch, "E334", {"start": v(-11.5, 18.9) * mm, "end": v(-10.86, 19.54) * mm});
            skLineSegment(sketch, "E335", {"start": v(-10.86, 19.54) * mm, "end": v(-9.6, 19.54) * mm});
            skLineSegment(sketch, "E336", {"start": v(-9.6, 19.54) * mm, "end": v(-8.96, 18.9) * mm});
            skLineSegment(sketch, "E337", {"start": v(-3.88, 17.64) * mm, "end": v(-4.52, 17) * mm});
            skLineSegment(sketch, "E338", {"start": v(-4.52, 17) * mm, "end": v(-5.78, 17) * mm});
            skLineSegment(sketch, "E339", {"start": v(-5.78, 17) * mm, "end": v(-6.42, 17.64) * mm});
            skLineSegment(sketch, "E340", {"start": v(-6.42, 17.64) * mm, "end": v(-6.42, 18.9) * mm});
            skLineSegment(sketch, "E341", {"start": v(-6.42, 18.9) * mm, "end": v(-5.78, 19.54) * mm});
            skLineSegment(sketch, "E342", {"start": v(-5.78, 19.54) * mm, "end": v(-4.52, 19.54) * mm});
            skLineSegment(sketch, "E343", {"start": v(-4.52, 19.54) * mm, "end": v(-3.88, 18.9) * mm});
            skLineSegment(sketch, "E344", {"start": v(-7.05, 17) * mm, "end": v(-6.42, 17.64) * mm});
            skLineSegment(sketch, "E345", {"start": v(-6.42, 18.9) * mm, "end": v(-7.05, 19.54) * mm});
            skLineSegment(sketch, "E346", {"start": v(-8.32, 19.54) * mm, "end": v(-7.05, 19.54) * mm});
            skLineSegment(sketch, "E347", {"start": v(0.56, 17) * mm, "end": v(-0.71, 17) * mm});
            skLineSegment(sketch, "E348", {"start": v(-0.71, 17) * mm, "end": v(-1.34, 17.64) * mm});
            skLineSegment(sketch, "E349", {"start": v(-1.34, 17.64) * mm, "end": v(-1.34, 18.9) * mm});
            skLineSegment(sketch, "E350", {"start": v(-1.34, 18.9) * mm, "end": v(-0.71, 19.54) * mm});
            skLineSegment(sketch, "E351", {"start": v(-1.34, 17.64) * mm, "end": v(-1.98, 17) * mm});
            skLineSegment(sketch, "E352", {"start": v(-1.98, 17) * mm, "end": v(-3.25, 17) * mm});
            skLineSegment(sketch, "E353", {"start": v(-3.25, 17) * mm, "end": v(-3.88, 17.64) * mm});
            skLineSegment(sketch, "E354", {"start": v(-3.88, 17.64) * mm, "end": v(-3.88, 18.9) * mm});
            skLineSegment(sketch, "E355", {"start": v(-3.88, 18.9) * mm, "end": v(-3.25, 19.54) * mm});
            skLineSegment(sketch, "E356", {"start": v(-3.25, 19.54) * mm, "end": v(-1.98, 19.54) * mm});
            skLineSegment(sketch, "E357", {"start": v(-1.98, 19.54) * mm, "end": v(-1.34, 18.9) * mm});
            skLineSegment(sketch, "E358", {"start": v(1.2, 17.64) * mm, "end": v(1.2, 18.9) * mm});
            skLineSegment(sketch, "E359", {"start": v(0.56, 17) * mm, "end": v(1.2, 17.64) * mm});
            skLineSegment(sketch, "E360", {"start": v(1.2, 18.9) * mm, "end": v(0.56, 19.54) * mm});
            skLineSegment(sketch, "E361", {"start": v(-0.71, 19.54) * mm, "end": v(0.56, 19.54) * mm});
            skLineSegment(sketch, "E362", {"start": v(-22.28, 17) * mm, "end": v(-23.54, 17) * mm});
            skLineSegment(sketch, "E363", {"start": v(-23.54, 17) * mm, "end": v(-24.18, 17.64) * mm});
            skLineSegment(sketch, "E364", {"start": v(-24.18, 17.64) * mm, "end": v(-24.18, 18.9) * mm});
            skLineSegment(sketch, "E365", {"start": v(-24.18, 18.9) * mm, "end": v(-23.54, 19.54) * mm});
            skLineSegment(sketch, "E366", {"start": v(-22.28, 17) * mm, "end": v(-21.64, 17.64) * mm});
            skLineSegment(sketch, "E367", {"start": v(-21.64, 18.9) * mm, "end": v(-22.28, 19.54) * mm});
            skLineSegment(sketch, "E368", {"start": v(-23.54, 19.54) * mm, "end": v(-22.28, 19.54) * mm});
            skLineSegment(sketch, "E369", {"start": v(-4.15, 14.63) * mm, "end": v(-4.15, 13.03) * mm});
            skFitSpline(sketch, "E370", {"points": [v(-5.85, 14.83) * mm, v(-5.99, 14.86) * mm, v(-6.12, 14.77) * mm, v(-6.15, 14.63) * mm]});
            skFitSpline(sketch, "E371", {"points": [v(-6.15, 13.03) * mm, v(-6.12, 12.9) * mm, v(-5.99, 12.8) * mm, v(-5.85, 12.83) * mm]});
            skFitSpline(sketch, "E372", {"points": [v(-4.45, 12.83) * mm, v(-4.31, 12.8) * mm, v(-4.18, 12.9) * mm, v(-4.15, 13.03) * mm]});
            skFitSpline(sketch, "E373", {"points": [v(-4.15, 14.63) * mm, v(-4.18, 14.77) * mm, v(-4.31, 14.86) * mm, v(-4.45, 14.83) * mm]});
            skLineSegment(sketch, "E374", {"start": v(-6.15, 13.03) * mm, "end": v(-6.15, 14.63) * mm});
            skLineSegment(sketch, "E375", {"start": v(-1.61, 14.63) * mm, "end": v(-1.61, 13.03) * mm});
            skFitSpline(sketch, "E376", {"points": [v(-3.36, 14.93) * mm, v(-3.51, 14.91) * mm, v(-3.63, 14.78) * mm, v(-3.61, 14.63) * mm]});
            skFitSpline(sketch, "E377", {"points": [v(-3.61, 13.03) * mm, v(-3.63, 12.88) * mm, v(-3.51, 12.75) * mm, v(-3.36, 12.73) * mm]});
            skFitSpline(sketch, "E378", {"points": [v(-1.86, 12.73) * mm, v(-1.71, 12.74) * mm, v(-1.6, 12.88) * mm, v(-1.61, 13.03) * mm]});
            skFitSpline(sketch, "E379", {"points": [v(-1.61, 14.63) * mm, v(-1.6, 14.78) * mm, v(-1.71, 14.91) * mm, v(-1.86, 14.93) * mm]});
            skLineSegment(sketch, "E380", {"start": v(-1.86, 14.93) * mm, "end": v(-3.36, 14.93) * mm});
            skLineSegment(sketch, "E381", {"start": v(-1.86, 12.73) * mm, "end": v(-3.36, 12.73) * mm});
            skLineSegment(sketch, "E382", {"start": v(-3.61, 13.03) * mm, "end": v(-3.61, 14.63) * mm});
            skLineSegment(sketch, "E383", {"start": v(0.92, 14.63) * mm, "end": v(0.92, 13.03) * mm});
            skFitSpline(sketch, "E384", {"points": [v(-0.83, 14.93) * mm, v(-0.98, 14.91) * mm, v(-1.09, 14.78) * mm, v(-1.08, 14.63) * mm]});
            skFitSpline(sketch, "E385", {"points": [v(-1.08, 13.03) * mm, v(-1.09, 12.88) * mm, v(-0.98, 12.75) * mm, v(-0.83, 12.73) * mm]});
            skFitSpline(sketch, "E386", {"points": [v(0.67, 12.73) * mm, v(0.82, 12.74) * mm, v(0.94, 12.88) * mm, v(0.92, 13.03) * mm]});
            skFitSpline(sketch, "E387", {"points": [v(0.92, 14.63) * mm, v(0.94, 14.78) * mm, v(0.82, 14.91) * mm, v(0.67, 14.93) * mm]});
            skLineSegment(sketch, "E388", {"start": v(0.67, 14.93) * mm, "end": v(-0.83, 14.93) * mm});
            skLineSegment(sketch, "E389", {"start": v(0.67, 12.73) * mm, "end": v(-0.83, 12.73) * mm});
            skLineSegment(sketch, "E390", {"start": v(-1.08, 13.03) * mm, "end": v(-1.08, 14.63) * mm});
            skLineSegment(sketch, "E391", {"start": v(4.98, 14.63) * mm, "end": v(4.98, 13.03) * mm});
            skFitSpline(sketch, "E392", {"points": [v(3.23, 14.93) * mm, v(3.08, 14.91) * mm, v(2.97, 14.78) * mm, v(2.98, 14.63) * mm]});
            skFitSpline(sketch, "E393", {"points": [v(2.98, 13.03) * mm, v(2.97, 12.88) * mm, v(3.08, 12.75) * mm, v(3.23, 12.73) * mm]});
            skFitSpline(sketch, "E394", {"points": [v(4.73, 12.73) * mm, v(4.88, 12.74) * mm, v(5, 12.88) * mm, v(4.98, 13.03) * mm]});
            skFitSpline(sketch, "E395", {"points": [v(4.98, 14.63) * mm, v(5, 14.78) * mm, v(4.88, 14.91) * mm, v(4.73, 14.93) * mm]});
            skLineSegment(sketch, "E396", {"start": v(4.73, 14.93) * mm, "end": v(3.23, 14.93) * mm});
            skLineSegment(sketch, "E397", {"start": v(4.73, 12.73) * mm, "end": v(3.23, 12.73) * mm});
            skLineSegment(sketch, "E398", {"start": v(2.98, 13.03) * mm, "end": v(2.98, 14.63) * mm});
            skLineSegment(sketch, "E399", {"start": v(7.52, 14.63) * mm, "end": v(7.52, 13.03) * mm});
            skFitSpline(sketch, "E400", {"points": [v(5.77, 14.93) * mm, v(5.62, 14.91) * mm, v(5.5, 14.78) * mm, v(5.52, 14.63) * mm]});
            skFitSpline(sketch, "E401", {"points": [v(5.52, 13.03) * mm, v(5.5, 12.88) * mm, v(5.62, 12.75) * mm, v(5.77, 12.73) * mm]});
            skFitSpline(sketch, "E402", {"points": [v(7.27, 12.73) * mm, v(7.42, 12.74) * mm, v(7.53, 12.88) * mm, v(7.52, 13.03) * mm]});
            skFitSpline(sketch, "E403", {"points": [v(7.52, 14.63) * mm, v(7.53, 14.78) * mm, v(7.42, 14.91) * mm, v(7.27, 14.93) * mm]});
            skLineSegment(sketch, "E404", {"start": v(7.27, 14.93) * mm, "end": v(5.77, 14.93) * mm});
            skLineSegment(sketch, "E405", {"start": v(7.27, 12.73) * mm, "end": v(5.77, 12.73) * mm});
            skLineSegment(sketch, "E406", {"start": v(5.52, 13.03) * mm, "end": v(5.52, 14.63) * mm});
            skLineSegment(sketch, "E407", {"start": v(10.06, 14.63) * mm, "end": v(10.06, 13.03) * mm});
            skFitSpline(sketch, "E408", {"points": [v(8.3, 14.93) * mm, v(8.16, 14.91) * mm, v(8.04, 14.78) * mm, v(8.06, 14.63) * mm]});
            skFitSpline(sketch, "E409", {"points": [v(8.06, 13.03) * mm, v(8.04, 12.88) * mm, v(8.16, 12.75) * mm, v(8.3, 12.73) * mm]});
            skFitSpline(sketch, "E410", {"points": [v(9.8, 12.73) * mm, v(9.96, 12.74) * mm, v(10.07, 12.88) * mm, v(10.06, 13.03) * mm]});
            skFitSpline(sketch, "E411", {"points": [v(10.06, 14.63) * mm, v(10.07, 14.78) * mm, v(9.96, 14.91) * mm, v(9.8, 14.93) * mm]});
            skLineSegment(sketch, "E412", {"start": v(9.8, 14.93) * mm, "end": v(8.3, 14.93) * mm});
            skLineSegment(sketch, "E413", {"start": v(9.8, 12.73) * mm, "end": v(8.3, 12.73) * mm});
            skLineSegment(sketch, "E414", {"start": v(8.06, 13.03) * mm, "end": v(8.06, 14.63) * mm});
            skLineSegment(sketch, "E415", {"start": v(24, 1.63) * mm, "end": v(24, 0.03) * mm});
            skFitSpline(sketch, "E416", {"points": [v(22.31, 1.83) * mm, v(22.17, 1.85) * mm, v(22.04, 1.76) * mm, v(22.01, 1.63) * mm]});
            skFitSpline(sketch, "E417", {"points": [v(22.01, 0.03) * mm, v(22.04, -0.1) * mm, v(22.17, -0.2) * mm, v(22.31, -0.17) * mm]});
            skFitSpline(sketch, "E418", {"points": [v(23.7, -0.17) * mm, v(23.85, -0.2) * mm, v(23.98, -0.1) * mm, v(24, 0.03) * mm]});
            skFitSpline(sketch, "E419", {"points": [v(24, 1.63) * mm, v(23.98, 1.76) * mm, v(23.85, 1.85) * mm, v(23.7, 1.83) * mm]});
            skLineSegment(sketch, "E420", {"start": v(22.01, 0.03) * mm, "end": v(22.01, 1.63) * mm});
            skLineSegment(sketch, "E421", {"start": v(-26.71, 18.9) * mm, "end": v(-26.08, 19.54) * mm});
            skLineSegment(sketch, "E422", {"start": v(-26.08, 19.54) * mm, "end": v(-24.81, 19.54) * mm});
            skLineSegment(sketch, "E423", {"start": v(-24.81, 19.54) * mm, "end": v(-24.18, 18.9) * mm});
            skLineSegment(sketch, "E424", {"start": v(-24.18, 17.64) * mm, "end": v(-24.81, 17) * mm});
            skLineSegment(sketch, "E425", {"start": v(-24.81, 17) * mm, "end": v(-26.08, 17) * mm});
            skLineSegment(sketch, "E426", {"start": v(-26.08, 17) * mm, "end": v(-26.71, 17.64) * mm});
            skLineSegment(sketch, "E427", {"start": v(-31.15, 19.54) * mm, "end": v(-29.89, 19.54) * mm});
            skLineSegment(sketch, "E428", {"start": v(-29.89, 19.54) * mm, "end": v(-29.25, 18.9) * mm});
            skLineSegment(sketch, "E429", {"start": v(-29.25, 17.64) * mm, "end": v(-29.89, 17) * mm});
            skLineSegment(sketch, "E430", {"start": v(-29.25, 18.9) * mm, "end": v(-28.62, 19.54) * mm});
            skLineSegment(sketch, "E431", {"start": v(-28.62, 19.54) * mm, "end": v(-27.35, 19.54) * mm});
            skLineSegment(sketch, "E432", {"start": v(-27.35, 19.54) * mm, "end": v(-26.71, 18.9) * mm});
            skLineSegment(sketch, "E433", {"start": v(-26.71, 17.64) * mm, "end": v(-27.35, 17) * mm});
            skLineSegment(sketch, "E434", {"start": v(-27.35, 17) * mm, "end": v(-28.62, 17) * mm});
            skLineSegment(sketch, "E435", {"start": v(-28.62, 17) * mm, "end": v(-29.25, 17.64) * mm});
            skLineSegment(sketch, "E436", {"start": v(-31.79, 18.9) * mm, "end": v(-31.79, 17.64) * mm});
            skLineSegment(sketch, "E437", {"start": v(-31.15, 19.54) * mm, "end": v(-31.79, 18.9) * mm});
            skLineSegment(sketch, "E438", {"start": v(-31.79, 17.64) * mm, "end": v(-31.15, 17) * mm});
            skLineSegment(sketch, "E439", {"start": v(-29.89, 17) * mm, "end": v(-31.15, 17) * mm});
            skLineSegment(sketch, "E440", {"start": v(-24.18, 18.9) * mm, "end": v(-24.18, 17.64) * mm});
            skLineSegment(sketch, "E441", {"start": v(31.26, -17.25) * mm, "end": v(31.89, -17.88) * mm});
            skLineSegment(sketch, "E442", {"start": v(31.89, -17.88) * mm, "end": v(31.89, -19.15) * mm});
            skLineSegment(sketch, "E443", {"start": v(31.89, -19.15) * mm, "end": v(31.26, -19.79) * mm});
            skLineSegment(sketch, "E444", {"start": v(31.26, -19.79) * mm, "end": v(29.99, -19.79) * mm});
            skLineSegment(sketch, "E445", {"start": v(29.99, -19.79) * mm, "end": v(29.35, -19.15) * mm});
            skLineSegment(sketch, "E446", {"start": v(29.35, -19.15) * mm, "end": v(29.35, -17.88) * mm});
            skLineSegment(sketch, "E447", {"start": v(29.35, -17.88) * mm, "end": v(29.99, -17.25) * mm});
            skLineSegment(sketch, "E448", {"start": v(31.89, -12.8) * mm, "end": v(31.89, -14.08) * mm});
            skLineSegment(sketch, "E449", {"start": v(31.89, -14.08) * mm, "end": v(31.26, -14.71) * mm});
            skLineSegment(sketch, "E450", {"start": v(31.26, -14.71) * mm, "end": v(29.99, -14.71) * mm});
            skLineSegment(sketch, "E451", {"start": v(29.99, -14.71) * mm, "end": v(29.35, -14.08) * mm});
            skLineSegment(sketch, "E452", {"start": v(31.26, -14.71) * mm, "end": v(31.89, -15.35) * mm});
            skLineSegment(sketch, "E453", {"start": v(31.89, -15.35) * mm, "end": v(31.89, -16.61) * mm});
            skLineSegment(sketch, "E454", {"start": v(31.89, -16.61) * mm, "end": v(31.26, -17.25) * mm});
            skLineSegment(sketch, "E455", {"start": v(31.26, -17.25) * mm, "end": v(29.99, -17.25) * mm});
            skLineSegment(sketch, "E456", {"start": v(29.99, -17.25) * mm, "end": v(29.35, -16.61) * mm});
            skLineSegment(sketch, "E457", {"start": v(29.35, -16.61) * mm, "end": v(29.35, -15.35) * mm});
            skLineSegment(sketch, "E458", {"start": v(29.35, -15.35) * mm, "end": v(29.99, -14.71) * mm});
            skLineSegment(sketch, "E459", {"start": v(31.26, -9.64) * mm, "end": v(31.89, -10.27) * mm});
            skLineSegment(sketch, "E460", {"start": v(31.89, -10.27) * mm, "end": v(31.89, -11.54) * mm});
            skLineSegment(sketch, "E461", {"start": v(31.89, -11.54) * mm, "end": v(31.26, -12.17) * mm});
            skLineSegment(sketch, "E462", {"start": v(31.26, -12.17) * mm, "end": v(29.99, -12.17) * mm});
            skLineSegment(sketch, "E463", {"start": v(29.99, -12.17) * mm, "end": v(29.35, -11.54) * mm});
            skLineSegment(sketch, "E464", {"start": v(29.35, -11.54) * mm, "end": v(29.35, -10.27) * mm});
            skLineSegment(sketch, "E465", {"start": v(29.35, -10.27) * mm, "end": v(29.99, -9.64) * mm});
            skLineSegment(sketch, "E466", {"start": v(31.89, -12.8) * mm, "end": v(31.26, -12.17) * mm});
            skLineSegment(sketch, "E467", {"start": v(29.99, -12.17) * mm, "end": v(29.35, -12.8) * mm});
            skLineSegment(sketch, "E468", {"start": v(29.35, -14.08) * mm, "end": v(29.35, -12.8) * mm});
            skLineSegment(sketch, "E469", {"start": v(31.89, -5.2) * mm, "end": v(31.89, -6.47) * mm});
            skLineSegment(sketch, "E470", {"start": v(31.89, -6.47) * mm, "end": v(31.26, -7.1) * mm});
            skLineSegment(sketch, "E471", {"start": v(31.26, -7.1) * mm, "end": v(29.99, -7.1) * mm});
            skLineSegment(sketch, "E472", {"start": v(29.99, -7.1) * mm, "end": v(29.35, -6.47) * mm});
            skLineSegment(sketch, "E473", {"start": v(31.26, -7.1) * mm, "end": v(31.89, -7.73) * mm});
            skLineSegment(sketch, "E474", {"start": v(31.89, -7.73) * mm, "end": v(31.89, -9) * mm});
            skLineSegment(sketch, "E475", {"start": v(31.89, -9) * mm, "end": v(31.26, -9.64) * mm});
            skLineSegment(sketch, "E476", {"start": v(31.26, -9.64) * mm, "end": v(29.99, -9.64) * mm});
            skLineSegment(sketch, "E477", {"start": v(29.99, -9.64) * mm, "end": v(29.35, -9) * mm});
            skLineSegment(sketch, "E478", {"start": v(29.35, -9) * mm, "end": v(29.35, -7.73) * mm});
            skLineSegment(sketch, "E479", {"start": v(29.35, -7.73) * mm, "end": v(29.99, -7.1) * mm});
            skLineSegment(sketch, "E480", {"start": v(31.26, -2.03) * mm, "end": v(31.89, -2.66) * mm});
            skLineSegment(sketch, "E481", {"start": v(31.89, -2.66) * mm, "end": v(31.89, -3.93) * mm});
            skLineSegment(sketch, "E482", {"start": v(31.89, -3.93) * mm, "end": v(31.26, -4.56) * mm});
            skLineSegment(sketch, "E483", {"start": v(31.26, -4.56) * mm, "end": v(29.99, -4.56) * mm});
            skLineSegment(sketch, "E484", {"start": v(29.99, -4.56) * mm, "end": v(29.35, -3.93) * mm});
            skLineSegment(sketch, "E485", {"start": v(29.35, -3.93) * mm, "end": v(29.35, -2.66) * mm});
            skLineSegment(sketch, "E486", {"start": v(29.35, -2.66) * mm, "end": v(29.99, -2.03) * mm});
            skLineSegment(sketch, "E487", {"start": v(31.89, -5.2) * mm, "end": v(31.26, -4.56) * mm});
            skLineSegment(sketch, "E488", {"start": v(29.99, -4.56) * mm, "end": v(29.35, -5.2) * mm});
            skLineSegment(sketch, "E489", {"start": v(29.35, -6.47) * mm, "end": v(29.35, -5.2) * mm});
            skLineSegment(sketch, "E490", {"start": v(31.89, 2.41) * mm, "end": v(31.89, 1.14) * mm});
            skLineSegment(sketch, "E491", {"start": v(31.89, 1.14) * mm, "end": v(31.26, 0.51) * mm});
            skLineSegment(sketch, "E492", {"start": v(31.26, 0.51) * mm, "end": v(29.99, 0.51) * mm});
            skLineSegment(sketch, "E493", {"start": v(29.99, 0.51) * mm, "end": v(29.35, 1.14) * mm});
            skLineSegment(sketch, "E494", {"start": v(31.26, 0.51) * mm, "end": v(31.89, -0.12) * mm});
            skLineSegment(sketch, "E495", {"start": v(31.89, -0.12) * mm, "end": v(31.89, -1.4) * mm});
            skLineSegment(sketch, "E496", {"start": v(31.89, -1.4) * mm, "end": v(31.26, -2.03) * mm});
            skLineSegment(sketch, "E497", {"start": v(31.26, -2.03) * mm, "end": v(29.99, -2.03) * mm});
            skLineSegment(sketch, "E498", {"start": v(29.99, -2.03) * mm, "end": v(29.35, -1.4) * mm});
            skLineSegment(sketch, "E499", {"start": v(29.35, -1.4) * mm, "end": v(29.35, -0.12) * mm});
            skLineSegment(sketch, "E500", {"start": v(29.35, -0.12) * mm, "end": v(29.99, 0.51) * mm});
            skLineSegment(sketch, "E501", {"start": v(31.26, 5.58) * mm, "end": v(31.89, 4.95) * mm});
            skLineSegment(sketch, "E502", {"start": v(31.89, 4.95) * mm, "end": v(31.89, 3.68) * mm});
            skLineSegment(sketch, "E503", {"start": v(31.89, 3.68) * mm, "end": v(31.26, 3.05) * mm});
            skLineSegment(sketch, "E504", {"start": v(31.26, 3.05) * mm, "end": v(29.99, 3.05) * mm});
            skLineSegment(sketch, "E505", {"start": v(29.99, 3.05) * mm, "end": v(29.35, 3.68) * mm});
            skLineSegment(sketch, "E506", {"start": v(29.35, 3.68) * mm, "end": v(29.35, 4.95) * mm});
            skLineSegment(sketch, "E507", {"start": v(29.35, 4.95) * mm, "end": v(29.99, 5.58) * mm});
            skLineSegment(sketch, "E508", {"start": v(31.89, 2.41) * mm, "end": v(31.26, 3.05) * mm});
            skLineSegment(sketch, "E509", {"start": v(29.99, 3.05) * mm, "end": v(29.35, 2.41) * mm});
            skLineSegment(sketch, "E510", {"start": v(29.35, 1.14) * mm, "end": v(29.35, 2.41) * mm});
            skLineSegment(sketch, "E511", {"start": v(31.89, 10.02) * mm, "end": v(31.89, 8.76) * mm});
            skLineSegment(sketch, "E512", {"start": v(31.89, 8.76) * mm, "end": v(31.26, 8.12) * mm});
            skLineSegment(sketch, "E513", {"start": v(31.26, 8.12) * mm, "end": v(29.99, 8.12) * mm});
            skLineSegment(sketch, "E514", {"start": v(29.99, 8.12) * mm, "end": v(29.35, 8.76) * mm});
            skLineSegment(sketch, "E515", {"start": v(31.26, 8.12) * mm, "end": v(31.89, 7.49) * mm});
            skLineSegment(sketch, "E516", {"start": v(31.89, 7.49) * mm, "end": v(31.89, 6.22) * mm});
            skLineSegment(sketch, "E517", {"start": v(31.89, 6.22) * mm, "end": v(31.26, 5.58) * mm});
            skLineSegment(sketch, "E518", {"start": v(31.26, 5.58) * mm, "end": v(29.99, 5.58) * mm});
            skLineSegment(sketch, "E519", {"start": v(29.99, 5.58) * mm, "end": v(29.35, 6.22) * mm});
            skLineSegment(sketch, "E520", {"start": v(29.35, 6.22) * mm, "end": v(29.35, 7.49) * mm});
            skLineSegment(sketch, "E521", {"start": v(29.35, 7.49) * mm, "end": v(29.99, 8.12) * mm});
            skLineSegment(sketch, "E522", {"start": v(31.26, 10.66) * mm, "end": v(29.99, 10.66) * mm});
            skLineSegment(sketch, "E523", {"start": v(31.89, 10.02) * mm, "end": v(31.26, 10.66) * mm});
            skLineSegment(sketch, "E524", {"start": v(29.99, 10.66) * mm, "end": v(29.35, 10.02) * mm});
            skLineSegment(sketch, "E525", {"start": v(29.35, 8.76) * mm, "end": v(29.35, 10.02) * mm});
            skLineSegment(sketch, "E526", {"start": v(31.26, -19.79) * mm, "end": v(31.89, -20.42) * mm});
            skLineSegment(sketch, "E527", {"start": v(31.89, -20.42) * mm, "end": v(31.89, -21.69) * mm});
            skLineSegment(sketch, "E528", {"start": v(31.89, -21.69) * mm, "end": v(31.26, -22.32) * mm});
            skLineSegment(sketch, "E529", {"start": v(31.26, -22.32) * mm, "end": v(29.99, -22.32) * mm});
            skLineSegment(sketch, "E530", {"start": v(29.99, -22.32) * mm, "end": v(29.35, -21.69) * mm});
            skLineSegment(sketch, "E531", {"start": v(29.35, -21.69) * mm, "end": v(29.35, -20.42) * mm});
            skLineSegment(sketch, "E532", {"start": v(29.35, -20.42) * mm, "end": v(29.99, -19.79) * mm});
            skLineSegment(sketch, "E533", {"start": v(-11.46, -23.69) * mm, "end": v(-15.46, -23.69) * mm});
            skLineSegment(sketch, "E534", {"start": v(-15.46, -19.7) * mm, "end": v(-11.46, -19.7) * mm});
            skLineSegment(sketch, "E535", {"start": v(-11.46, -23.69) * mm, "end": v(-11.46, -23.49) * mm});
            skLineSegment(sketch, "E536", {"start": v(-15.46, -23.69) * mm, "end": v(-15.46, -23.49) * mm});
            skLineSegment(sketch, "E537", {"start": v(-11.46, -19.7) * mm, "end": v(-11.46, -19.9) * mm});
            skLineSegment(sketch, "E538", {"start": v(-15.46, -19.7) * mm, "end": v(-15.46, -19.9) * mm});
            skLineSegment(sketch, "E539", {"start": v(-15.52, 15.25) * mm, "end": v(-13.23, 15.25) * mm});
            skLineSegment(sketch, "E540", {"start": v(-13.23, 15.25) * mm, "end": v(-13.23, 10.46) * mm});
            skLineSegment(sketch, "E541", {"start": v(-13.23, 10.46) * mm, "end": v(-14.92, 8.76) * mm});
            skLineSegment(sketch, "E542", {"start": v(-14.92, 8.76) * mm, "end": v(-15.52, 8.76) * mm});
            skLineSegment(sketch, "E543", {"start": v(-17.42, 8.76) * mm, "end": v(-18.02, 8.76) * mm});
            skLineSegment(sketch, "E544", {"start": v(-18.02, 8.76) * mm, "end": v(-19.72, 10.46) * mm});
            skLineSegment(sketch, "E545", {"start": v(-19.72, 10.46) * mm, "end": v(-19.72, 15.25) * mm});
            skLineSegment(sketch, "E546", {"start": v(-19.72, 15.25) * mm, "end": v(-17.42, 15.25) * mm});
            skLineSegment(sketch, "E547", {"start": v(-22.5, 15.25) * mm, "end": v(-20.2, 15.25) * mm});
            skLineSegment(sketch, "E548", {"start": v(-20.2, 15.25) * mm, "end": v(-20.2, 10.46) * mm});
            skLineSegment(sketch, "E549", {"start": v(-20.2, 10.46) * mm, "end": v(-21.9, 8.76) * mm});
            skLineSegment(sketch, "E550", {"start": v(-21.9, 8.76) * mm, "end": v(-22.5, 8.76) * mm});
            skLineSegment(sketch, "E551", {"start": v(-24.4, 8.76) * mm, "end": v(-25, 8.76) * mm});
            skLineSegment(sketch, "E552", {"start": v(-25, 8.76) * mm, "end": v(-26.7, 10.46) * mm});
            skLineSegment(sketch, "E553", {"start": v(-26.7, 10.46) * mm, "end": v(-26.7, 15.25) * mm});
            skLineSegment(sketch, "E554", {"start": v(-26.7, 15.25) * mm, "end": v(-24.4, 15.25) * mm});
            skLineSegment(sketch, "E555", {"start": v(9.04, -9.6) * mm, "end": v(9.04, -8.4) * mm});
            skLineSegment(sketch, "E556", {"start": v(10.34, -6.5) * mm, "end": v(10.94, -6.5) * mm});
            skLineSegment(sketch, "E557", {"start": v(12.24, -8.4) * mm, "end": v(12.24, -9.6) * mm});
            skLineSegment(sketch, "E558", {"start": v(10.34, -11.5) * mm, "end": v(10.94, -11.5) * mm});
            skLineSegment(sketch, "E559", {"start": v(39.02, -18.77) * mm, "end": v(38.42, -18.77) * mm});
            skLineSegment(sketch, "E560", {"start": v(38.42, -18.77) * mm, "end": v(38.42, -19.57) * mm});
            skLineSegment(sketch, "E561", {"start": v(40.62, -18.77) * mm, "end": v(41.22, -18.77) * mm});
            skLineSegment(sketch, "E562", {"start": v(41.22, -18.77) * mm, "end": v(41.22, -19.57) * mm});
            skLineSegment(sketch, "E563", {"start": v(35.21, -18.77) * mm, "end": v(34.61, -18.77) * mm});
            skLineSegment(sketch, "E564", {"start": v(34.61, -18.77) * mm, "end": v(34.61, -19.57) * mm});
            skLineSegment(sketch, "E565", {"start": v(36.81, -18.77) * mm, "end": v(37.41, -18.77) * mm});
            skLineSegment(sketch, "E566", {"start": v(37.41, -18.77) * mm, "end": v(37.41, -19.57) * mm});
            skLineSegment(sketch, "E567", {"start": v(-0.47, 5.3) * mm, "end": v(-0.47, 6.5) * mm});
            skLineSegment(sketch, "E568", {"start": v(0.83, 8.4) * mm, "end": v(1.43, 8.4) * mm});
            skLineSegment(sketch, "E569", {"start": v(2.73, 6.5) * mm, "end": v(2.73, 5.3) * mm});
            skLineSegment(sketch, "E570", {"start": v(0.83, 3.4) * mm, "end": v(1.43, 3.4) * mm});
            skLineSegment(sketch, "E571", {"start": v(38.71, 2.35) * mm, "end": v(39.31, 2.35) * mm});
            skLineSegment(sketch, "E572", {"start": v(39.31, 2.35) * mm, "end": v(39.31, 3.15) * mm});
            skLineSegment(sketch, "E573", {"start": v(37.12, 2.35) * mm, "end": v(36.52, 2.35) * mm});
            skLineSegment(sketch, "E574", {"start": v(36.52, 2.35) * mm, "end": v(36.52, 3.15) * mm});
            skLineSegment(sketch, "E575", {"start": v(29.38, -26.13) * mm, "end": v(31.89, -26.13) * mm});
            skLineSegment(sketch, "E576", {"start": v(33.16, -27.13) * mm, "end": v(33.16, -30.2) * mm});
            skLineSegment(sketch, "E577", {"start": v(31.86, -31.2) * mm, "end": v(29.38, -31.2) * mm});
            skLineSegment(sketch, "E578", {"start": v(28.08, -30.2) * mm, "end": v(28.08, -27.13) * mm});
            skLineSegment(sketch, "E579", {"start": v(-26.77, -26.85) * mm, "end": v(-25.77, -26.85) * mm});
            skLineSegment(sketch, "E580", {"start": v(-25.77, -26.85) * mm, "end": v(-25.77, -29.85) * mm});
            skLineSegment(sketch, "E581", {"start": v(-25.77, -29.85) * mm, "end": v(-26.77, -29.85) * mm});
            skLineSegment(sketch, "E582", {"start": v(-33.76, -26.85) * mm, "end": v(-34.76, -26.85) * mm});
            skLineSegment(sketch, "E583", {"start": v(-34.76, -26.85) * mm, "end": v(-34.76, -29.85) * mm});
            skLineSegment(sketch, "E584", {"start": v(-34.76, -29.85) * mm, "end": v(-33.76, -29.85) * mm});
            skLineSegment(sketch, "E585", {"start": v(23.8, -18.24) * mm, "end": v(23.8, -15.24) * mm});
            skFitSpline(sketch, "E586", {"points": [v(24.3, -14.74) * mm, v(24.03, -14.74) * mm, v(23.8, -14.97) * mm, v(23.8, -15.24) * mm]});
            skLineSegment(sketch, "E587", {"start": v(24.3, -14.74) * mm, "end": v(27.3, -14.74) * mm});
            skFitSpline(sketch, "E588", {"points": [v(27.8, -15.24) * mm, v(27.8, -14.97) * mm, v(27.58, -14.74) * mm, v(27.3, -14.74) * mm]});
            skLineSegment(sketch, "E589", {"start": v(27.8, -15.24) * mm, "end": v(27.8, -18.24) * mm});
            skFitSpline(sketch, "E590", {"points": [v(27.3, -18.74) * mm, v(27.58, -18.74) * mm, v(27.8, -18.51) * mm, v(27.8, -18.24) * mm]});
            skLineSegment(sketch, "E591", {"start": v(27.3, -18.74) * mm, "end": v(24.3, -18.74) * mm});
            skFitSpline(sketch, "E592", {"points": [v(23.8, -18.24) * mm, v(23.8, -18.51) * mm, v(24.03, -18.74) * mm, v(24.3, -18.74) * mm]});
            skLineSegment(sketch, "E593", {"start": v(-7.37, -20.27) * mm, "end": v(-7.37, -23.16) * mm});
            skLineSegment(sketch, "E594", {"start": v(-7.37, -23.16) * mm, "end": v(-8.13, -23.16) * mm});
            skLineSegment(sketch, "E595", {"start": v(-8.13, -23.16) * mm, "end": v(-8.13, -20.27) * mm});
            skLineSegment(sketch, "E596", {"start": v(-8.13, -20.27) * mm, "end": v(-7.37, -20.27) * mm});
            skLineSegment(sketch, "E597", {"start": v(14.01, 2.8) * mm, "end": v(13.74, 2.53) * mm});
            skLineSegment(sketch, "E598", {"start": v(13.74, 2.53) * mm, "end": v(7.55, 2.53) * mm});
            skLineSegment(sketch, "E599", {"start": v(7.55, 2.53) * mm, "end": v(7.27, 2.8) * mm});
            skLineSegment(sketch, "E600", {"start": v(7.27, 2.8) * mm, "end": v(7.27, 9) * mm});
            skLineSegment(sketch, "E601", {"start": v(7.27, 9) * mm, "end": v(7.55, 9.27) * mm});
            skLineSegment(sketch, "E602", {"start": v(7.55, 9.27) * mm, "end": v(13.74, 9.27) * mm});
            skLineSegment(sketch, "E603", {"start": v(13.74, 9.27) * mm, "end": v(14.01, 9) * mm});
            skLineSegment(sketch, "E604", {"start": v(14.01, 9) * mm, "end": v(14.01, 2.8) * mm});
            skLineSegment(sketch, "E605", {"start": v(-41.23, -8.27) * mm, "end": v(-41.23, -9.34) * mm});
            skLineSegment(sketch, "E606", {"start": v(-41.23, -10.34) * mm, "end": v(-41.23, -11.41) * mm});
            skLineSegment(sketch, "E607", {"start": v(-41.23, -12.41) * mm, "end": v(-41.23, -13.48) * mm});
            skLineSegment(sketch, "E608", {"start": v(-41.23, -14.48) * mm, "end": v(-41.23, -15.55) * mm});
            skLineSegment(sketch, "E609", {"start": v(-36.99, -8.78) * mm, "end": v(-36.99, -15.88) * mm});
            skLineSegment(sketch, "E610", {"start": v(-36.99, -15.88) * mm, "end": v(-38.77, -15.88) * mm});
            skLineSegment(sketch, "E611", {"start": v(-38.77, -15.88) * mm, "end": v(-38.77, -16.65) * mm});
            skLineSegment(sketch, "E612", {"start": v(-38.77, -16.65) * mm, "end": v(-40.8, -16.65) * mm});
            skLineSegment(sketch, "E613", {"start": v(-40.8, -16.65) * mm, "end": v(-40.8, -15.88) * mm});
            skLineSegment(sketch, "E614", {"start": v(-40.8, -15.88) * mm, "end": v(-42.06, -15.88) * mm});
            skLineSegment(sketch, "E615", {"start": v(-42.06, -15.88) * mm, "end": v(-42.06, -8.78) * mm});
            skLineSegment(sketch, "E616", {"start": v(-42.06, -8.78) * mm, "end": v(-40.8, -8.78) * mm});
            skLineSegment(sketch, "E617", {"start": v(-40.8, -8.78) * mm, "end": v(-40.8, -8.02) * mm});
            skLineSegment(sketch, "E618", {"start": v(-40.8, -8.02) * mm, "end": v(-38.77, -8.02) * mm});
            skLineSegment(sketch, "E619", {"start": v(-38.77, -8.02) * mm, "end": v(-38.77, -8.78) * mm});
            skLineSegment(sketch, "E620", {"start": v(-38.77, -8.78) * mm, "end": v(-36.99, -8.78) * mm});
            skLineSegment(sketch, "E621", {"start": v(-37.2, -25.68) * mm, "end": v(-33.7, -25.68) * mm});
            skLineSegment(sketch, "E622", {"start": v(-33.7, -25.68) * mm, "end": v(-33.7, -24.88) * mm});
            skLineSegment(sketch, "E623", {"start": v(-33.7, -24.88) * mm, "end": v(-36.2, -24.88) * mm});
            skLineSegment(sketch, "E624", {"start": v(-36.2, -24.88) * mm, "end": v(-36.2, -23.69) * mm});
            skLineSegment(sketch, "E625", {"start": v(-36.2, -19.7) * mm, "end": v(-36.2, -18.5) * mm});
            skLineSegment(sketch, "E626", {"start": v(-36.2, -18.5) * mm, "end": v(-33.7, -18.5) * mm});
            skLineSegment(sketch, "E627", {"start": v(-33.7, -18.5) * mm, "end": v(-33.7, -17.7) * mm});
            skLineSegment(sketch, "E628", {"start": v(-33.7, -17.7) * mm, "end": v(-37.2, -17.7) * mm});
            skLineSegment(sketch, "E629", {"start": v(-23.92, -6.78) * mm, "end": v(-37.24, -6.78) * mm});
            skLineSegment(sketch, "E630", {"start": v(-23.92, -6.78) * mm, "end": v(-23.92, -2.03) * mm});
            skLineSegment(sketch, "E631", {"start": v(-23.92, 0.83) * mm, "end": v(-23.92, 3.68) * mm});
            skLineSegment(sketch, "E632", {"start": v(-36.3, 7.17) * mm, "end": v(-23.92, 7.17) * mm});
            skLineSegment(sketch, "E633", {"start": v(-23.92, 7.17) * mm, "end": v(-23.92, 6.54) * mm});
            skLineSegment(sketch, "E634", {"start": v(-39.1, -5.48) * mm, "end": v(-39.1, -2.89) * mm});
            skLineSegment(sketch, "E635", {"start": v(-39.1, -2.89) * mm, "end": v(-36.8, -1.89) * mm});
            skLineSegment(sketch, "E636", {"start": v(-36.8, -1.89) * mm, "end": v(-36.8, 5.3) * mm});
            skLineSegment(sketch, "E637", {"start": v(-36.8, 5.3) * mm, "end": v(-37.8, 5.8) * mm});
            skLineSegment(sketch, "E638", {"start": v(-38.71, 7.2) * mm, "end": v(-38.71, -6.78) * mm});
            skLineSegment(sketch, "E639", {"start": v(-38.71, -6.78) * mm, "end": v(-23.93, -6.78) * mm});
            skLineSegment(sketch, "E640", {"start": v(-23.93, -6.78) * mm, "end": v(-23.93, 7.2) * mm});
            skLineSegment(sketch, "E641", {"start": v(-23.93, 7.2) * mm, "end": v(-38.71, 7.2) * mm});
            skLineSegment(sketch, "E642", {"start": v(-41.68, 15.24) * mm, "end": v(-38.69, 15.24) * mm});
            skLineSegment(sketch, "E643", {"start": v(-35.7, 15.24) * mm, "end": v(-27.2, 15.24) * mm});
            skLineSegment(sketch, "E644", {"start": v(-27.2, 15.24) * mm, "end": v(-27.2, 9.25) * mm});
            skLineSegment(sketch, "E645", {"start": v(-27.2, 9.25) * mm, "end": v(-28.2, 9.25) * mm});
            skLineSegment(sketch, "E646", {"start": v(-31.7, 9.25) * mm, "end": v(-37.69, 9.25) * mm});
            skLineSegment(sketch, "E647", {"start": v(-40.68, 9.25) * mm, "end": v(-41.68, 9.25) * mm});
            skLineSegment(sketch, "E648", {"start": v(-41.68, 9.25) * mm, "end": v(-41.68, 9.75) * mm});
            skLineSegment(sketch, "E649", {"start": v(-41.68, 9.75) * mm, "end": v(-41.68, 14.74) * mm});
            skLineSegment(sketch, "E650", {"start": v(-41.68, 14.74) * mm, "end": v(-41.68, 15.24) * mm});
            skLineSegment(sketch, "E651", {"start": v(-41.68, 14.74) * mm, "end": v(-44.18, 14.74) * mm});
            skLineSegment(sketch, "E652", {"start": v(-44.18, 14.74) * mm, "end": v(-44.18, 9.75) * mm});
            skLineSegment(sketch, "E653", {"start": v(-44.18, 9.75) * mm, "end": v(-41.68, 9.75) * mm});
            skLineSegment(sketch, "E654", {"start": v(-14.42, -16.78) * mm, "end": v(-12.5, -16.78) * mm});
            skLineSegment(sketch, "E655", {"start": v(-14.42, -18.35) * mm, "end": v(-12.5, -18.35) * mm});
            skLineSegment(sketch, "E656", {"start": v(-17.89, -18.35) * mm, "end": v(-19.81, -18.35) * mm});
            skLineSegment(sketch, "E657", {"start": v(-17.89, -16.78) * mm, "end": v(-19.81, -16.78) * mm});
            skLineSegment(sketch, "E658", {"start": v(-19.81, -8.22) * mm, "end": v(-17.89, -8.22) * mm});
            skLineSegment(sketch, "E659", {"start": v(-19.81, -9.79) * mm, "end": v(-17.89, -9.79) * mm});
            skLineSegment(sketch, "E660", {"start": v(19.45, -17.31) * mm, "end": v(18.96, -17.31) * mm});
            skLineSegment(sketch, "E661", {"start": v(18.96, -16.87) * mm, "end": v(19.45, -16.87) * mm});
            skLineSegment(sketch, "E662", {"start": v(4.62, -13.2) * mm, "end": v(4.13, -13.2) * mm});
            skLineSegment(sketch, "E663", {"start": v(4.13, -12.74) * mm, "end": v(4.62, -12.74) * mm});
            skLineSegment(sketch, "E664", {"start": v(13.72, -9.87) * mm, "end": v(13.72, -10.36) * mm});
            skLineSegment(sketch, "E665", {"start": v(13.27, -10.36) * mm, "end": v(13.27, -9.87) * mm});
            skLineSegment(sketch, "E666", {"start": v(8.33, -7.17) * mm, "end": v(8.33, -7.66) * mm});
            skLineSegment(sketch, "E667", {"start": v(7.88, -7.66) * mm, "end": v(7.88, -7.17) * mm});
            skLineSegment(sketch, "E668", {"start": v(15.64, -24.13) * mm, "end": v(15.15, -24.13) * mm});
            skLineSegment(sketch, "E669", {"start": v(15.15, -23.68) * mm, "end": v(15.64, -23.68) * mm});
            skLineSegment(sketch, "E670", {"start": v(19.45, -18.58) * mm, "end": v(18.96, -18.58) * mm});
            skLineSegment(sketch, "E671", {"start": v(18.96, -18.13) * mm, "end": v(19.45, -18.13) * mm});
            skLineSegment(sketch, "E672", {"start": v(5.64, -23.68) * mm, "end": v(6.13, -23.68) * mm});
            skLineSegment(sketch, "E673", {"start": v(6.13, -24.13) * mm, "end": v(5.64, -24.13) * mm});
            skLineSegment(sketch, "E674", {"start": v(-5.44, -17.18) * mm, "end": v(-5.44, -16.69) * mm});
            skLineSegment(sketch, "E675", {"start": v(-5, -16.69) * mm, "end": v(-5, -17.18) * mm});
            skLineSegment(sketch, "E676", {"start": v(17.71, -10.36) * mm, "end": v(17.71, -9.87) * mm});
            skLineSegment(sketch, "E677", {"start": v(18.16, -9.87) * mm, "end": v(18.16, -10.36) * mm});
            skLineSegment(sketch, "E678", {"start": v(-19.81, -10.75) * mm, "end": v(-17.89, -10.75) * mm});
            skLineSegment(sketch, "E679", {"start": v(-19.81, -12.33) * mm, "end": v(-17.89, -12.33) * mm});
            skLineSegment(sketch, "E680", {"start": v(-14.25, -11.24) * mm, "end": v(-14.25, -9.3) * mm});
            skLineSegment(sketch, "E681", {"start": v(-12.67, -11.24) * mm, "end": v(-12.67, -9.3) * mm});
            skLineSegment(sketch, "E682", {"start": v(-24.8, -19.24) * mm, "end": v(-24.31, -19.24) * mm});
            skLineSegment(sketch, "E683", {"start": v(-24.31, -19.7) * mm, "end": v(-24.8, -19.7) * mm});
            skLineSegment(sketch, "E684", {"start": v(1.37, 2.03) * mm, "end": v(0.88, 2.03) * mm});
            skLineSegment(sketch, "E685", {"start": v(0.88, 2.48) * mm, "end": v(1.37, 2.48) * mm});
            skLineSegment(sketch, "E686", {"start": v(0.88, 9.77) * mm, "end": v(1.37, 9.77) * mm});
            skLineSegment(sketch, "E687", {"start": v(1.37, 9.33) * mm, "end": v(0.88, 9.33) * mm});
            skLineSegment(sketch, "E688", {"start": v(39.6, -4.8) * mm, "end": v(39.6, -4.32) * mm});
            skLineSegment(sketch, "E689", {"start": v(40.04, -4.32) * mm, "end": v(40.04, -4.8) * mm});
            skLineSegment(sketch, "E690", {"start": v(36.9, -8.93) * mm, "end": v(36.9, -8.44) * mm});
            skLineSegment(sketch, "E691", {"start": v(37.35, -8.44) * mm, "end": v(37.35, -8.93) * mm});
            skLineSegment(sketch, "E692", {"start": v(18.33, 7.08) * mm, "end": v(18.82, 7.08) * mm});
            skLineSegment(sketch, "E693", {"start": v(18.82, 6.63) * mm, "end": v(18.33, 6.63) * mm});
            skLineSegment(sketch, "E694", {"start": v(29.91, 13.6) * mm, "end": v(29.43, 13.6) * mm});
            skLineSegment(sketch, "E695", {"start": v(29.43, 14.05) * mm, "end": v(29.91, 14.05) * mm});
            skLineSegment(sketch, "E696", {"start": v(21.35, 8.53) * mm, "end": v(20.86, 8.53) * mm});
            skLineSegment(sketch, "E697", {"start": v(20.86, 8.98) * mm, "end": v(21.35, 8.98) * mm});
            skLineSegment(sketch, "E698", {"start": v(21.35, 2.82) * mm, "end": v(20.86, 2.82) * mm});
            skLineSegment(sketch, "E699", {"start": v(20.86, 3.27) * mm, "end": v(21.35, 3.27) * mm});
            skLineSegment(sketch, "E700", {"start": v(26.83, 9.08) * mm, "end": v(24.9, 9.08) * mm});
            skLineSegment(sketch, "E701", {"start": v(26.83, 10.65) * mm, "end": v(24.9, 10.65) * mm});
            skLineSegment(sketch, "E702", {"start": v(24.9, 4.23) * mm, "end": v(26.83, 4.23) * mm});
            skLineSegment(sketch, "E703", {"start": v(24.9, 2.66) * mm, "end": v(26.83, 2.66) * mm});
            skLineSegment(sketch, "E704", {"start": v(26.1, 15.2) * mm, "end": v(25.62, 15.2) * mm});
            skLineSegment(sketch, "E705", {"start": v(25.62, 15.64) * mm, "end": v(26.1, 15.64) * mm});
            skLineSegment(sketch, "E706", {"start": v(26.1, 5.28) * mm, "end": v(25.62, 5.28) * mm});
            skLineSegment(sketch, "E707", {"start": v(25.62, 5.73) * mm, "end": v(26.1, 5.73) * mm});
            skLineSegment(sketch, "E708", {"start": v(3.76, 3.12) * mm, "end": v(3.76, 3.6) * mm});
            skLineSegment(sketch, "E709", {"start": v(4.2, 3.6) * mm, "end": v(4.2, 3.12) * mm});
            skLineSegment(sketch, "E710", {"start": v(10.42, -2.11) * mm, "end": v(10.42, -1.62) * mm});
            skLineSegment(sketch, "E711", {"start": v(10.87, -1.62) * mm, "end": v(10.87, -2.11) * mm});
            skLineSegment(sketch, "E712", {"start": v(3.76, 8.59) * mm, "end": v(3.76, 9.08) * mm});
            skLineSegment(sketch, "E713", {"start": v(4.2, 9.08) * mm, "end": v(4.2, 8.59) * mm});
            skLineSegment(sketch, "E714", {"start": v(18.33, 5.17) * mm, "end": v(18.82, 5.17) * mm});
            skLineSegment(sketch, "E715", {"start": v(18.82, 4.73) * mm, "end": v(18.33, 4.73) * mm});
            skLineSegment(sketch, "E716", {"start": v(-25.08, -17.3) * mm, "end": v(-24.03, -17.3) * mm});
            skLineSegment(sketch, "E717", {"start": v(-24.06, -18.46) * mm, "end": v(-25.48, -18.46) * mm});
            skLineSegment(sketch, "E718", {"start": v(-9.1, -18.56) * mm, "end": v(-8.95, -18.56) * mm});
            skLineSegment(sketch, "E719", {"start": v(-8.5, -18.56) * mm, "end": v(-8.3, -18.56) * mm});
            skLineSegment(sketch, "E720", {"start": v(-7.85, -18.56) * mm, "end": v(-7.65, -18.56) * mm});
            skLineSegment(sketch, "E721", {"start": v(-7.2, -18.56) * mm, "end": v(-7, -18.56) * mm});
            skLineSegment(sketch, "E722", {"start": v(-6.55, -18.56) * mm, "end": v(-6.45, -18.56) * mm});
            skLineSegment(sketch, "E723", {"start": v(-9.05, -15.3) * mm, "end": v(-8.95, -15.3) * mm});
            skLineSegment(sketch, "E724", {"start": v(-8.5, -15.3) * mm, "end": v(-8.3, -15.3) * mm});
            skLineSegment(sketch, "E725", {"start": v(-7.85, -15.3) * mm, "end": v(-7.65, -15.3) * mm});
            skLineSegment(sketch, "E726", {"start": v(-7.2, -15.3) * mm, "end": v(-7, -15.3) * mm});
            skLineSegment(sketch, "E727", {"start": v(-6.55, -15.3) * mm, "end": v(-6.45, -15.3) * mm});
            skLineSegment(sketch, "E728", {"start": v(-25.36, -23.09) * mm, "end": v(-25.36, -20.29) * mm});
            skLineSegment(sketch, "E729", {"start": v(-23.76, -20.29) * mm, "end": v(-23.76, -23.09) * mm});
            skLineSegment(sketch, "E730", {"start": v(-23.76, -23.09) * mm, "end": v(-25.36, -23.09) * mm});
            skLineSegment(sketch, "E731", {"start": v(-23.76, -20.29) * mm, "end": v(-25.36, -20.29) * mm});
            skLineSegment(sketch, "E732", {"start": v(36.56, -3.07) * mm, "end": v(36.56, -6.06) * mm});
            skLineSegment(sketch, "E733", {"start": v(33.56, -6.06) * mm, "end": v(36.56, -6.06) * mm});
            skLineSegment(sketch, "E734", {"start": v(33.56, -6.06) * mm, "end": v(33.56, -3.07) * mm});
            skLineSegment(sketch, "E735", {"start": v(36.56, -3.07) * mm, "end": v(33.56, -3.07) * mm});
            skLineSegment(sketch, "E736", {"start": v(25.24, 8.49) * mm, "end": v(26.49, 8.49) * mm});
            skLineSegment(sketch, "E737", {"start": v(26.49, 6.49) * mm, "end": v(25.24, 6.49) * mm});
            skLineSegment(sketch, "E738", {"start": v(26.49, 6.49) * mm, "end": v(26.49, 8.49) * mm});
            skLineSegment(sketch, "E739", {"start": v(25.24, 6.49) * mm, "end": v(25.24, 8.49) * mm});
            skLineSegment(sketch, "E740", {"start": v(26.66, 14.28) * mm, "end": v(26.66, 11.48) * mm});
            skLineSegment(sketch, "E741", {"start": v(25.07, 11.48) * mm, "end": v(25.07, 14.28) * mm});
            skLineSegment(sketch, "E742", {"start": v(25.07, 14.28) * mm, "end": v(26.66, 14.28) * mm});
            skLineSegment(sketch, "E743", {"start": v(25.07, 11.48) * mm, "end": v(26.66, 11.48) * mm});
            skLineSegment(sketch, "E744", {"start": v(-22.28, -30.14) * mm, "end": v(-22.28, -29.1) * mm});
            skLineSegment(sketch, "E745", {"start": v(-21.13, -29.12) * mm, "end": v(-21.13, -30.54) * mm});
            skLineSegment(sketch, "E746", {"start": v(-33.34, -15.6) * mm, "end": v(-33.34, -15.1) * mm});
            skLineSegment(sketch, "E747", {"start": v(-32.9, -15.1) * mm, "end": v(-32.9, -15.6) * mm});
            skLineSegment(sketch, "E748", {"start": v(15.94, -9.87) * mm, "end": v(15.94, -10.36) * mm});
            skLineSegment(sketch, "E749", {"start": v(15.5, -10.36) * mm, "end": v(15.5, -9.87) * mm});
            skLineSegment(sketch, "E750", {"start": v(-24.82, -30.14) * mm, "end": v(-24.82, -29.1) * mm});
            skLineSegment(sketch, "E751", {"start": v(-23.67, -29.12) * mm, "end": v(-23.67, -30.54) * mm});
            skLineSegment(sketch, "E752", {"start": v(-14.92, 8.76) * mm, "end": v(-18.02, 8.76) * mm});
            skLineSegment(sketch, "E753", {"start": v(-19.72, 15.25) * mm, "end": v(-13.23, 15.25) * mm});
            skLineSegment(sketch, "E754", {"start": v(-21.9, 8.76) * mm, "end": v(-25, 8.76) * mm});
            skLineSegment(sketch, "E755", {"start": v(-26.7, 15.25) * mm, "end": v(-20.2, 15.25) * mm});
            skLineSegment(sketch, "E756", {"start": v(41.24, -18.8) * mm, "end": v(41.24, -20.13) * mm});
            skLineSegment(sketch, "E757", {"start": v(41.24, -20.13) * mm, "end": v(38.4, -20.13) * mm});
            skLineSegment(sketch, "E758", {"start": v(38.4, -20.13) * mm, "end": v(38.4, -18.8) * mm});
            skLineSegment(sketch, "E759", {"start": v(38.4, -18.8) * mm, "end": v(41.24, -18.8) * mm});
            skLineSegment(sketch, "E760", {"start": v(37.43, -18.8) * mm, "end": v(37.43, -20.13) * mm});
            skLineSegment(sketch, "E761", {"start": v(37.43, -20.13) * mm, "end": v(34.6, -20.13) * mm});
            skLineSegment(sketch, "E762", {"start": v(34.6, -20.13) * mm, "end": v(34.6, -18.8) * mm});
            skLineSegment(sketch, "E763", {"start": v(34.6, -18.8) * mm, "end": v(37.43, -18.8) * mm});
            skLineSegment(sketch, "E764", {"start": v(36.5, 2.39) * mm, "end": v(36.5, 3.7) * mm});
            skLineSegment(sketch, "E765", {"start": v(36.5, 3.7) * mm, "end": v(39.34, 3.7) * mm});
            skLineSegment(sketch, "E766", {"start": v(39.34, 3.7) * mm, "end": v(39.34, 2.39) * mm});
            skLineSegment(sketch, "E767", {"start": v(39.34, 2.39) * mm, "end": v(36.5, 2.39) * mm});
            skLineSegment(sketch, "E768", {"start": v(26.9, -28.9) * mm, "end": v(26.9, -28.42) * mm});
            skLineSegment(sketch, "E769", {"start": v(27.36, -28.42) * mm, "end": v(27.36, -28.9) * mm});
            skLineSegment(sketch, "E770", {"start": v(-18.13, -14.93) * mm, "end": v(-18.62, -14.93) * mm});
            skLineSegment(sketch, "E771", {"start": v(-18.62, -14.49) * mm, "end": v(-18.13, -14.49) * mm});
            skLineSegment(sketch, "E772", {"start": v(-18.13, -13.67) * mm, "end": v(-18.62, -13.67) * mm});
            skLineSegment(sketch, "E773", {"start": v(-18.62, -13.22) * mm, "end": v(-18.13, -13.22) * mm});
            skLineSegment(sketch, "E774", {"start": v(-30.36, -15.1) * mm, "end": v(-30.36, -15.6) * mm});
            skLineSegment(sketch, "E775", {"start": v(-30.8, -15.6) * mm, "end": v(-30.8, -15.1) * mm});
            skLineSegment(sketch, "E776", {"start": v(-28.46, -15.1) * mm, "end": v(-28.46, -15.6) * mm});
            skLineSegment(sketch, "E777", {"start": v(-28.9, -15.6) * mm, "end": v(-28.9, -15.1) * mm});
            skLineSegment(sketch, "E778", {"start": v(3.76, 5.66) * mm, "end": v(3.76, 6.15) * mm});
            skLineSegment(sketch, "E779", {"start": v(4.2, 6.15) * mm, "end": v(4.2, 5.66) * mm});
            skLineSegment(sketch, "E780", {"start": v(36.74, -0.53) * mm, "end": v(36.74, -0.04) * mm});
            skLineSegment(sketch, "E781", {"start": v(37.19, -0.04) * mm, "end": v(37.19, -0.53) * mm});
            skLineSegment(sketch, "E782", {"start": v(18.82, 11.07) * mm, "end": v(18.33, 11.07) * mm});
            skLineSegment(sketch, "E783", {"start": v(18.33, 11.52) * mm, "end": v(18.82, 11.52) * mm});
            skLineSegment(sketch, "E784", {"start": v(6.74, -1.62) * mm, "end": v(6.74, -2.11) * mm});
            skLineSegment(sketch, "E785", {"start": v(6.3, -2.11) * mm, "end": v(6.3, -1.62) * mm});
            skLineSegment(sketch, "E786", {"start": v(16.73, -1.62) * mm, "end": v(16.73, -2.11) * mm});
            skLineSegment(sketch, "E787", {"start": v(16.29, -2.11) * mm, "end": v(16.29, -1.62) * mm});
            skLineSegment(sketch, "E788", {"start": v(7.56, -2.11) * mm, "end": v(7.56, -1.62) * mm});
            skLineSegment(sketch, "E789", {"start": v(8.01, -1.62) * mm, "end": v(8.01, -2.11) * mm});
            skLineSegment(sketch, "E790", {"start": v(12.13, -1.62) * mm, "end": v(12.13, -2.11) * mm});
            skLineSegment(sketch, "E791", {"start": v(11.69, -2.11) * mm, "end": v(11.69, -1.62) * mm});
            skLineSegment(sketch, "E792", {"start": v(21.35, 11.07) * mm, "end": v(20.86, 11.07) * mm});
            skLineSegment(sketch, "E793", {"start": v(20.86, 11.52) * mm, "end": v(21.35, 11.52) * mm});
            skLineSegment(sketch, "E794", {"start": v(13.88, -1.62) * mm, "end": v(13.88, -2.11) * mm});
            skLineSegment(sketch, "E795", {"start": v(13.43, -2.11) * mm, "end": v(13.43, -1.62) * mm});
            skLineSegment(sketch, "E796", {"start": v(14.86, -2.11) * mm, "end": v(14.86, -1.62) * mm});
            skLineSegment(sketch, "E797", {"start": v(15.3, -1.62) * mm, "end": v(15.3, -2.11) * mm});
            skLineSegment(sketch, "E798", {"start": v(18.33, 8.98) * mm, "end": v(18.82, 8.98) * mm});
            skLineSegment(sketch, "E799", {"start": v(18.82, 8.53) * mm, "end": v(18.33, 8.53) * mm});
            skLineSegment(sketch, "E800", {"start": v(18.33, 3.27) * mm, "end": v(18.82, 3.27) * mm});
            skLineSegment(sketch, "E801", {"start": v(18.82, 2.82) * mm, "end": v(18.33, 2.82) * mm});
            skLineSegment(sketch, "E802", {"start": v(-22.17, -11.78) * mm, "end": v(-22.17, -11.3) * mm});
            skLineSegment(sketch, "E803", {"start": v(-21.72, -11.3) * mm, "end": v(-21.72, -11.78) * mm});
            skLineSegment(sketch, "E804", {"start": v(36.37, 7.92) * mm, "end": v(36.92, 7.92) * mm});
            skLineSegment(sketch, "E805", {"start": v(37.32, 7.92) * mm, "end": v(37.72, 7.92) * mm});
            skLineSegment(sketch, "E806", {"start": v(38.11, 7.92) * mm, "end": v(38.51, 7.92) * mm});
            skLineSegment(sketch, "E807", {"start": v(38.91, 7.92) * mm, "end": v(39.46, 7.92) * mm});
            skLineSegment(sketch, "E808", {"start": v(39.46, 7.92) * mm, "end": v(39.46, 6.42) * mm});
            skLineSegment(sketch, "E809", {"start": v(36.37, 6.42) * mm, "end": v(36.37, 7.92) * mm});
            skLineSegment(sketch, "E810", {"start": v(39.46, 6.42) * mm, "end": v(38.91, 6.42) * mm});
            skLineSegment(sketch, "E811", {"start": v(38.51, 6.42) * mm, "end": v(38.11, 6.42) * mm});
            skLineSegment(sketch, "E812", {"start": v(37.72, 6.42) * mm, "end": v(37.32, 6.42) * mm});
            skLineSegment(sketch, "E813", {"start": v(36.92, 6.42) * mm, "end": v(36.37, 6.42) * mm});
            skLineSegment(sketch, "E814", {"start": v(-28.24, -19.74) * mm, "end": v(-28.8, -19.74) * mm});
            skLineSegment(sketch, "E815", {"start": v(-29.2, -19.74) * mm, "end": v(-29.6, -19.74) * mm});
            skLineSegment(sketch, "E816", {"start": v(-30, -19.74) * mm, "end": v(-30.4, -19.74) * mm});
            skLineSegment(sketch, "E817", {"start": v(-30.79, -19.74) * mm, "end": v(-31.34, -19.74) * mm});
            skLineSegment(sketch, "E818", {"start": v(-31.34, -19.74) * mm, "end": v(-31.34, -18.24) * mm});
            skLineSegment(sketch, "E819", {"start": v(-28.24, -18.24) * mm, "end": v(-28.24, -19.74) * mm});
            skLineSegment(sketch, "E820", {"start": v(-31.34, -18.24) * mm, "end": v(-30.79, -18.24) * mm});
            skLineSegment(sketch, "E821", {"start": v(-30.4, -18.24) * mm, "end": v(-30, -18.24) * mm});
            skLineSegment(sketch, "E822", {"start": v(-29.6, -18.24) * mm, "end": v(-29.2, -18.24) * mm});
            skLineSegment(sketch, "E823", {"start": v(-28.8, -18.24) * mm, "end": v(-28.24, -18.24) * mm});
            skLineSegment(sketch, "E824", {"start": v(-17.94, -23.7) * mm, "end": v(-18.49, -23.7) * mm});
            skLineSegment(sketch, "E825", {"start": v(-18.89, -23.7) * mm, "end": v(-19.28, -23.7) * mm});
            skLineSegment(sketch, "E826", {"start": v(-19.68, -23.7) * mm, "end": v(-20.08, -23.7) * mm});
            skLineSegment(sketch, "E827", {"start": v(-20.48, -23.7) * mm, "end": v(-21.03, -23.7) * mm});
            skLineSegment(sketch, "E828", {"start": v(-21.03, -23.7) * mm, "end": v(-21.03, -22.2) * mm});
            skLineSegment(sketch, "E829", {"start": v(-17.94, -22.2) * mm, "end": v(-17.94, -23.7) * mm});
            skLineSegment(sketch, "E830", {"start": v(-21.03, -22.2) * mm, "end": v(-20.48, -22.2) * mm});
            skLineSegment(sketch, "E831", {"start": v(-20.08, -22.2) * mm, "end": v(-19.68, -22.2) * mm});
            skLineSegment(sketch, "E832", {"start": v(-19.28, -22.2) * mm, "end": v(-18.89, -22.2) * mm});
            skLineSegment(sketch, "E833", {"start": v(-18.49, -22.2) * mm, "end": v(-17.94, -22.2) * mm});
            skLineSegment(sketch, "E834", {"start": v(39.46, -24.02) * mm, "end": v(38.91, -24.02) * mm});
            skLineSegment(sketch, "E835", {"start": v(38.51, -24.02) * mm, "end": v(38.11, -24.02) * mm});
            skLineSegment(sketch, "E836", {"start": v(37.72, -24.02) * mm, "end": v(37.32, -24.02) * mm});
            skLineSegment(sketch, "E837", {"start": v(36.92, -24.02) * mm, "end": v(36.37, -24.02) * mm});
            skLineSegment(sketch, "E838", {"start": v(36.37, -24.02) * mm, "end": v(36.37, -22.52) * mm});
            skLineSegment(sketch, "E839", {"start": v(39.46, -22.52) * mm, "end": v(39.46, -24.02) * mm});
            skLineSegment(sketch, "E840", {"start": v(36.37, -22.52) * mm, "end": v(36.92, -22.52) * mm});
            skLineSegment(sketch, "E841", {"start": v(37.32, -22.52) * mm, "end": v(37.72, -22.52) * mm});
            skLineSegment(sketch, "E842", {"start": v(38.11, -22.52) * mm, "end": v(38.51, -22.52) * mm});
            skLineSegment(sketch, "E843", {"start": v(38.91, -22.52) * mm, "end": v(39.46, -22.52) * mm});
            skLineSegment(sketch, "E844", {"start": v(-1.77, 7.45) * mm, "end": v(-1.77, 6.9) * mm});
            skLineSegment(sketch, "E845", {"start": v(-1.77, 6.5) * mm, "end": v(-1.77, 6.1) * mm});
            skLineSegment(sketch, "E846", {"start": v(-1.77, 5.7) * mm, "end": v(-1.77, 5.3) * mm});
            skLineSegment(sketch, "E847", {"start": v(-1.77, 4.9) * mm, "end": v(-1.77, 4.35) * mm});
            skLineSegment(sketch, "E848", {"start": v(-1.77, 4.35) * mm, "end": v(-3.27, 4.35) * mm});
            skLineSegment(sketch, "E849", {"start": v(-3.27, 7.45) * mm, "end": v(-1.77, 7.45) * mm});
            skLineSegment(sketch, "E850", {"start": v(-3.27, 4.35) * mm, "end": v(-3.27, 4.9) * mm});
            skLineSegment(sketch, "E851", {"start": v(-3.27, 5.3) * mm, "end": v(-3.27, 5.7) * mm});
            skLineSegment(sketch, "E852", {"start": v(-3.27, 6.1) * mm, "end": v(-3.27, 6.5) * mm});
            skLineSegment(sketch, "E853", {"start": v(-3.27, 6.9) * mm, "end": v(-3.27, 7.45) * mm});
            skLineSegment(sketch, "E854", {"start": v(-21.03, -19.35) * mm, "end": v(-20.48, -19.35) * mm});
            skLineSegment(sketch, "E855", {"start": v(-20.08, -19.35) * mm, "end": v(-19.68, -19.35) * mm});
            skLineSegment(sketch, "E856", {"start": v(-19.28, -19.35) * mm, "end": v(-18.89, -19.35) * mm});
            skLineSegment(sketch, "E857", {"start": v(-18.49, -19.35) * mm, "end": v(-17.94, -19.35) * mm});
            skLineSegment(sketch, "E858", {"start": v(-17.94, -19.35) * mm, "end": v(-17.94, -20.85) * mm});
            skLineSegment(sketch, "E859", {"start": v(-21.03, -20.85) * mm, "end": v(-21.03, -19.35) * mm});
            skLineSegment(sketch, "E860", {"start": v(-17.94, -20.85) * mm, "end": v(-18.49, -20.85) * mm});
            skLineSegment(sketch, "E861", {"start": v(-18.89, -20.85) * mm, "end": v(-19.28, -20.85) * mm});
            skLineSegment(sketch, "E862", {"start": v(-19.68, -20.85) * mm, "end": v(-20.08, -20.85) * mm});
            skLineSegment(sketch, "E863", {"start": v(-20.48, -20.85) * mm, "end": v(-21.03, -20.85) * mm});
            skLineSegment(sketch, "E864", {"start": v(-17.2, -30.14) * mm, "end": v(-17.2, -29.1) * mm});
            skLineSegment(sketch, "E865", {"start": v(-16.06, -29.12) * mm, "end": v(-16.06, -30.54) * mm});
            skLineSegment(sketch, "E866", {"start": v(28.08, -27.13) * mm, "end": v(29.08, -26.13) * mm});
            skLineSegment(sketch, "E867", {"start": v(32.16, -26.13) * mm, "end": v(33.16, -27.13) * mm});
            skLineSegment(sketch, "E868", {"start": v(33.16, -30.2) * mm, "end": v(32.16, -31.2) * mm});
            skLineSegment(sketch, "E869", {"start": v(29.08, -31.2) * mm, "end": v(28.08, -30.2) * mm});
            skLineSegment(sketch, "E870", {"start": v(31.89, -30.57) * mm, "end": v(31.07, -30.57) * mm});
            skLineSegment(sketch, "E871", {"start": v(31.07, -30.57) * mm, "end": v(30.61, -30.82) * mm});
            skLineSegment(sketch, "E872", {"start": v(30.4, -30.57) * mm, "end": v(29.5, -30.57) * mm});
            skLineSegment(sketch, "E873", {"start": v(-19.74, -30.14) * mm, "end": v(-19.74, -29.1) * mm});
            skLineSegment(sketch, "E874", {"start": v(-18.6, -29.12) * mm, "end": v(-18.6, -30.54) * mm});
            skLineSegment(sketch, "E875", {"start": v(14.14, -14.39) * mm, "end": v(7.15, -14.39) * mm});
            skLineSegment(sketch, "E876", {"start": v(7.15, -14.39) * mm, "end": v(7.15, -21.38) * mm});
            skLineSegment(sketch, "E877", {"start": v(7.15, -21.38) * mm, "end": v(14.14, -21.38) * mm});
            skLineSegment(sketch, "E878", {"start": v(14.14, -21.38) * mm, "end": v(14.14, -14.39) * mm});
            skLineSegment(sketch, "E879", {"start": v(-34.39, -19.48) * mm, "end": v(-34.39, -18.7) * mm});
            skLineSegment(sketch, "E880", {"start": v(-34.78, -19.1) * mm, "end": v(-34, -19.1) * mm});
            skLineSegment(sketch, "E881", {"start": v(-34.39, -24.55) * mm, "end": v(-34.39, -23.78) * mm});
            skLineSegment(sketch, "E882", {"start": v(-41.68, 28.4) * mm, "end": v(-41.68, 28.46) * mm});
            skLineSegment(sketch, "E883", {"start": v(-41.68, 28.46) * mm, "end": v(-41.66, 28.72) * mm});
            skLineSegment(sketch, "E884", {"start": v(-41.66, 28.72) * mm, "end": v(-41.6, 28.97) * mm});
            skLineSegment(sketch, "E885", {"start": v(-41.6, 28.97) * mm, "end": v(-41.48, 29.2) * mm});
            skLineSegment(sketch, "E886", {"start": v(-41.48, 29.2) * mm, "end": v(-41.33, 29.42) * mm});
            skLineSegment(sketch, "E887", {"start": v(-41.33, 29.42) * mm, "end": v(-41.15, 29.6) * mm});
            skLineSegment(sketch, "E888", {"start": v(-41.15, 29.6) * mm, "end": v(-40.93, 29.76) * mm});
            skLineSegment(sketch, "E889", {"start": v(-40.93, 29.76) * mm, "end": v(-40.7, 29.87) * mm});
            skLineSegment(sketch, "E890", {"start": v(-40.7, 29.87) * mm, "end": v(-40.45, 29.93) * mm});
            skLineSegment(sketch, "E891", {"start": v(-40.45, 29.93) * mm, "end": v(-40.18, 29.96) * mm});
            skLineSegment(sketch, "E892", {"start": v(-40.18, 29.96) * mm, "end": v(-36.49, 29.96) * mm});
            skLineSegment(sketch, "E893", {"start": v(-36.49, 29.96) * mm, "end": v(-36.49, 28.4) * mm});
            skLineSegment(sketch, "E894", {"start": v(-36.49, 28.4) * mm, "end": v(-41.68, 28.4) * mm});
            skLineSegment(sketch, "E895", {"start": v(-41.68, 28.46) * mm, "end": v(-41.48, 28.46) * mm});
            skLineSegment(sketch, "E896", {"start": v(-41.48, 28.46) * mm, "end": v(-41.48, 23.56) * mm});
            skLineSegment(sketch, "E897", {"start": v(-41.48, 23.56) * mm, "end": v(-41.68, 23.56) * mm});
            skLineSegment(sketch, "E898", {"start": v(-41.68, 23.56) * mm, "end": v(-41.68, 28.46) * mm});
            skLineSegment(sketch, "E899", {"start": v(42.82, 28.4) * mm, "end": v(42.82, 28.46) * mm});
            skLineSegment(sketch, "E900", {"start": v(42.82, 28.46) * mm, "end": v(42.8, 28.72) * mm});
            skLineSegment(sketch, "E901", {"start": v(42.8, 28.72) * mm, "end": v(42.73, 28.97) * mm});
            skLineSegment(sketch, "E902", {"start": v(42.73, 28.97) * mm, "end": v(42.62, 29.2) * mm});
            skLineSegment(sketch, "E903", {"start": v(42.62, 29.2) * mm, "end": v(42.47, 29.42) * mm});
            skLineSegment(sketch, "E904", {"start": v(42.47, 29.42) * mm, "end": v(42.28, 29.6) * mm});
            skLineSegment(sketch, "E905", {"start": v(42.28, 29.6) * mm, "end": v(42.07, 29.76) * mm});
            skLineSegment(sketch, "E906", {"start": v(42.07, 29.76) * mm, "end": v(41.83, 29.87) * mm});
            skLineSegment(sketch, "E907", {"start": v(41.83, 29.87) * mm, "end": v(41.58, 29.93) * mm});
            skLineSegment(sketch, "E908", {"start": v(41.58, 29.93) * mm, "end": v(41.32, 29.96) * mm});
            skLineSegment(sketch, "E909", {"start": v(41.32, 29.96) * mm, "end": v(37.62, 29.96) * mm});
            skLineSegment(sketch, "E910", {"start": v(37.62, 29.96) * mm, "end": v(37.62, 28.4) * mm});
            skLineSegment(sketch, "E911", {"start": v(37.62, 28.4) * mm, "end": v(42.82, 28.4) * mm});
            skLineSegment(sketch, "E912", {"start": v(42.82, 28.46) * mm, "end": v(42.62, 28.46) * mm});
            skLineSegment(sketch, "E913", {"start": v(42.62, 28.46) * mm, "end": v(42.62, 23.56) * mm});
            skLineSegment(sketch, "E914", {"start": v(42.62, 23.56) * mm, "end": v(42.82, 23.56) * mm});
            skLineSegment(sketch, "E915", {"start": v(42.82, 23.56) * mm, "end": v(42.82, 28.46) * mm});
            skLineSegment(sketch, "E916", {"start": v(-41.68, -27.38) * mm, "end": v(-36.49, -27.38) * mm});
            skLineSegment(sketch, "E917", {"start": v(-36.49, -27.38) * mm, "end": v(-36.49, -26.58) * mm});
            skLineSegment(sketch, "E918", {"start": v(-36.49, -26.58) * mm, "end": v(-41.68, -26.58) * mm});
            skLineSegment(sketch, "E919", {"start": v(-41.68, -26.58) * mm, "end": v(-41.68, -27.38) * mm});
            skLineSegment(sketch, "E920", {"start": v(-41.68, -30.77) * mm, "end": v(-36.49, -30.77) * mm, "construction": true});
            skLineSegment(sketch, "E921", {"start": v(-36.49, -30.77) * mm, "end": v(-36.49, -32.47) * mm});
            skLineSegment(sketch, "E922", {"start": v(-36.49, -32.47) * mm, "end": v(-40.18, -32.47) * mm});
            skLineSegment(sketch, "E923", {"start": v(-40.18, -32.47) * mm, "end": v(-40.45, -32.45) * mm});
            skLineSegment(sketch, "E924", {"start": v(-40.45, -32.45) * mm, "end": v(-40.7, -32.38) * mm});
            skLineSegment(sketch, "E925", {"start": v(-40.7, -32.38) * mm, "end": v(-40.93, -32.27) * mm});
            skLineSegment(sketch, "E926", {"start": v(-40.93, -32.27) * mm, "end": v(-41.15, -32.12) * mm});
            skLineSegment(sketch, "E927", {"start": v(-41.15, -32.12) * mm, "end": v(-41.33, -31.94) * mm});
            skLineSegment(sketch, "E928", {"start": v(-41.33, -31.94) * mm, "end": v(-41.48, -31.72) * mm});
            skLineSegment(sketch, "E929", {"start": v(-41.48, -31.72) * mm, "end": v(-41.6, -31.48) * mm});
            skLineSegment(sketch, "E930", {"start": v(-41.6, -31.48) * mm, "end": v(-41.66, -31.23) * mm});
            skLineSegment(sketch, "E931", {"start": v(-41.66, -31.23) * mm, "end": v(-41.68, -30.97) * mm});
            skLineSegment(sketch, "E932", {"start": v(-41.68, -30.97) * mm, "end": v(-41.68, -30.77) * mm});
            skLineSegment(sketch, "E933", {"start": v(-40.88, -27.41) * mm, "end": v(-41.68, -27.41) * mm, "construction": true});
            skLineSegment(sketch, "E934", {"start": v(-41.68, -27.38) * mm, "end": v(-41.68, -30.77) * mm});
            skLineSegment(sketch, "E935", {"start": v(-41.68, -30.77) * mm, "end": v(-40.88, -30.77) * mm});
            skLineSegment(sketch, "E936", {"start": v(-40.88, -30.77) * mm, "end": v(-40.88, -27.38) * mm});
            skLineSegment(sketch, "E937", {"start": v(-36.49, -30.8) * mm, "end": v(-37.09, -30.8) * mm});
            skLineSegment(sketch, "E938", {"start": v(-37.09, -30.77) * mm, "end": v(-37.09, -27.38) * mm});
            skLineSegment(sketch, "E939", {"start": v(-37.09, -27.38) * mm, "end": v(-36.49, -27.38) * mm});
            skLineSegment(sketch, "E940", {"start": v(-36.49, -27.38) * mm, "end": v(-36.49, -30.77) * mm});
            skLineSegment(sketch, "E941", {"start": v(30.43, 28.4) * mm, "end": v(30.43, 29.96) * mm});
            skLineSegment(sketch, "E942", {"start": v(30.43, 29.96) * mm, "end": v(35.43, 29.96) * mm});
            skLineSegment(sketch, "E943", {"start": v(35.43, 29.96) * mm, "end": v(35.43, 28.4) * mm});
            skLineSegment(sketch, "E944", {"start": v(35.43, 28.4) * mm, "end": v(30.43, 28.4) * mm});
            skLineSegment(sketch, "E945", {"start": v(23.24, 28.4) * mm, "end": v(23.24, 29.96) * mm});
            skLineSegment(sketch, "E946", {"start": v(23.24, 29.96) * mm, "end": v(28.23, 29.96) * mm});
            skLineSegment(sketch, "E947", {"start": v(28.23, 29.96) * mm, "end": v(28.23, 28.4) * mm});
            skLineSegment(sketch, "E948", {"start": v(28.23, 28.4) * mm, "end": v(23.24, 28.4) * mm});
            skLineSegment(sketch, "E949", {"start": v(16.05, 28.4) * mm, "end": v(16.05, 29.96) * mm});
            skLineSegment(sketch, "E950", {"start": v(16.05, 29.96) * mm, "end": v(21.04, 29.96) * mm});
            skLineSegment(sketch, "E951", {"start": v(21.04, 29.96) * mm, "end": v(21.04, 28.4) * mm});
            skLineSegment(sketch, "E952", {"start": v(21.04, 28.4) * mm, "end": v(16.05, 28.4) * mm});
            skLineSegment(sketch, "E953", {"start": v(8.86, 28.4) * mm, "end": v(8.86, 29.96) * mm});
            skLineSegment(sketch, "E954", {"start": v(8.86, 29.96) * mm, "end": v(13.85, 29.96) * mm});
            skLineSegment(sketch, "E955", {"start": v(13.85, 29.96) * mm, "end": v(13.85, 28.4) * mm});
            skLineSegment(sketch, "E956", {"start": v(13.85, 28.4) * mm, "end": v(8.86, 28.4) * mm});
            skLineSegment(sketch, "E957", {"start": v(1.67, 28.4) * mm, "end": v(1.67, 29.96) * mm});
            skLineSegment(sketch, "E958", {"start": v(1.67, 29.96) * mm, "end": v(6.66, 29.96) * mm});
            skLineSegment(sketch, "E959", {"start": v(6.66, 29.96) * mm, "end": v(6.66, 28.4) * mm});
            skLineSegment(sketch, "E960", {"start": v(6.66, 28.4) * mm, "end": v(1.67, 28.4) * mm});
            skLineSegment(sketch, "E961", {"start": v(-5.53, 28.4) * mm, "end": v(-5.53, 29.96) * mm});
            skLineSegment(sketch, "E962", {"start": v(-5.53, 29.96) * mm, "end": v(-0.53, 29.96) * mm});
            skLineSegment(sketch, "E963", {"start": v(-0.53, 29.96) * mm, "end": v(-0.53, 28.4) * mm});
            skLineSegment(sketch, "E964", {"start": v(-0.53, 28.4) * mm, "end": v(-5.53, 28.4) * mm});
            skLineSegment(sketch, "E965", {"start": v(-12.72, 28.4) * mm, "end": v(-12.72, 29.96) * mm});
            skLineSegment(sketch, "E966", {"start": v(-12.72, 29.96) * mm, "end": v(-7.72, 29.96) * mm});
            skLineSegment(sketch, "E967", {"start": v(-7.72, 29.96) * mm, "end": v(-7.72, 28.4) * mm});
            skLineSegment(sketch, "E968", {"start": v(-7.72, 28.4) * mm, "end": v(-12.72, 28.4) * mm});
            skLineSegment(sketch, "E969", {"start": v(-19.9, 28.4) * mm, "end": v(-19.9, 29.96) * mm});
            skLineSegment(sketch, "E970", {"start": v(-19.9, 29.96) * mm, "end": v(-14.91, 29.96) * mm});
            skLineSegment(sketch, "E971", {"start": v(-14.91, 29.96) * mm, "end": v(-14.91, 28.4) * mm});
            skLineSegment(sketch, "E972", {"start": v(-14.91, 28.4) * mm, "end": v(-19.9, 28.4) * mm});
            skLineSegment(sketch, "E973", {"start": v(-27.1, 28.4) * mm, "end": v(-27.1, 29.96) * mm});
            skLineSegment(sketch, "E974", {"start": v(-27.1, 29.96) * mm, "end": v(-22.1, 29.96) * mm});
            skLineSegment(sketch, "E975", {"start": v(-22.1, 29.96) * mm, "end": v(-22.1, 28.4) * mm});
            skLineSegment(sketch, "E976", {"start": v(-22.1, 28.4) * mm, "end": v(-27.1, 28.4) * mm});
            skLineSegment(sketch, "E977", {"start": v(-34.3, 28.4) * mm, "end": v(-34.3, 29.96) * mm});
            skLineSegment(sketch, "E978", {"start": v(-34.3, 29.96) * mm, "end": v(-29.3, 29.96) * mm});
            skLineSegment(sketch, "E979", {"start": v(-29.3, 29.96) * mm, "end": v(-29.3, 28.4) * mm});
            skLineSegment(sketch, "E980", {"start": v(-29.3, 28.4) * mm, "end": v(-34.3, 28.4) * mm});
            skCircle(sketch, "E981", {"center": v(-38.99, -29.11) * mm, "radius": 1.6 * mm});
            skLineSegment(sketch, "E982", {"start": v(-40.88, -27.41) * mm, "end": v(-37.09, -30.8) * mm});
            skCircle(sketch, "E983", {"center": v(-38.99, 20.89) * mm, "radius": 1.6 * mm});
            skCircle(sketch, "E984", {"center": v(38.01, 20.89) * mm, "radius": 1.6 * mm});
            skLineSegment(sketch, "E985", {"start": v(-38.99, 20.89) * mm, "end": v(-38.99, -29.11) * mm, "construction": true});
            skLineSegment(sketch, "E986", {"start": v(38.01, 20.89) * mm, "end": v(-38.99, 20.89) * mm, "construction": true});
            skLineSegment(sketch, "E987", {"start": v(0, -32.47) * mm, "end": v(0, 29.96) * mm, "construction": true});
            skLineSegment(sketch, "E988", {"start": v(0, -1.26) * mm, "end": v(-4.47, -1.26) * mm, "construction": true});
            skSolve(sketch);
        }
        {
            var Q0;
            {var subQ52=sQuery(id+"F0.wireOp",EDGE,"E2");Q0=makeQuery(id+"F0.imprint","IMPRINT",FACE,{"disambiguationData":[TD([[makeQuery(id+"F0.imprint","IMPRINT",EDGE,{"derivedFrom":subQ52}),1.0]])]});}
            var Q1;
            {var subQ7=sQuery(id+"F0.wireOp",EDGE,"E641");Q1=makeQuery(id+"F0.imprint","IMPRINT",FACE,{"disambiguationData":[TD([[makeQuery(id+"F0.imprint","IMPRINT",EDGE,{"derivedFrom":subQ7}),1.0]])]});}
            var Q2;
            {var subQ138=sQuery(id+"F0.wireOp",EDGE,"E548");Q2=makeQuery(id+"F0.imprint","IMPRINT",FACE,{"disambiguationData":[TD([[makeQuery(id+"F0.imprint","IMPRINT",EDGE,{"derivedFrom":subQ138}),-1.0]])]});}
            var Q3;
            {var subQ138=sQuery(id+"F0.wireOp",EDGE,"E540");Q3=makeQuery(id+"F0.imprint","IMPRINT",FACE,{"disambiguationData":[TD([[makeQuery(id+"F0.imprint","IMPRINT",EDGE,{"derivedFrom":subQ138}),-1.0]])]});}
            var Q4;
            Q4=makeQuery(id+"F0.imprint","IMPRINT",FACE,{"disambiguationData":[TD([[makeQuery(id+"F0.imprint","IMPRINT",EDGE,{"derivedFrom":sQuery(id+"F0.wireOp",EDGE,"E421")}),-1.0]])]});
            var Q5;
            Q5=makeQuery(id+"F0.imprint","IMPRINT",FACE,{"disambiguationData":[TD([[makeQuery(id+"F0.imprint","IMPRINT",EDGE,{"derivedFrom":sQuery(id+"F0.wireOp",EDGE,"E597")}),-1.0]])]});
            var Q6;
            Q6=makeQuery(id+"F0.imprint","IMPRINT",FACE,{"disambiguationData":[TD([[makeQuery(id+"F0.imprint","IMPRINT",EDGE,{"derivedFrom":sQuery(id+"F0.wireOp",EDGE,"E875")}),1.0]])]});
            var Q7;
            Q7=makeQuery(id+"F0.imprint","IMPRINT",FACE,{"disambiguationData":[TD([[makeQuery(id+"F0.imprint","IMPRINT",EDGE,{"derivedFrom":sQuery(id+"F0.wireOp",EDGE,"E593")}),-1.0]])]});
            var Q8;
            Q8=makeQuery(id+"F0.imprint","IMPRINT",FACE,{"disambiguationData":[TD([[makeQuery(id+"F0.imprint","IMPRINT",EDGE,{"derivedFrom":sQuery(id+"F0.wireOp",EDGE,"E65")}),-1.0]])]});
            var Q9;
            Q9=makeQuery(id+"F0.imprint","IMPRINT",FACE,{"disambiguationData":[TD([[makeQuery(id+"F0.imprint","IMPRINT",EDGE,{"derivedFrom":sQuery(id+"F0.wireOp",EDGE,"E284")}),-1.0]])]});
            var Q10;
            Q10=makeQuery(id+"F0.imprint","IMPRINT",FACE,{"disambiguationData":[TD([[makeQuery(id+"F0.imprint","IMPRINT",EDGE,{"derivedFrom":sQuery(id+"F0.wireOp",EDGE,"E609")}),-1.0]])]});
            var Q11;
            Q11=makeQuery(id+"F0.imprint","IMPRINT",FACE,{"disambiguationData":[TD([[makeQuery(id+"F0.imprint","IMPRINT",EDGE,{"derivedFrom":sQuery(id+"F0.wireOp",EDGE,"E728")}),-1.0]])]});
            var Q12;
            {var subQ4=sQuery(id+"F0.wireOp",EDGE,"E922");Q12=makeQuery(id+"F0.imprint","IMPRINT",FACE,{"disambiguationData":[TD([[makeQuery(id+"F0.imprint","IMPRINT",EDGE,{"derivedFrom":subQ4}),-1.0]])]});}
            var Q13;
            {var subQ0=sQuery(id+"F0.wireOp",EDGE,"E933");Q13=makeQuery(id+"F0.imprint","IMPRINT",FACE,{"disambiguationData":[TD([[makeQuery(id+"F0.imprint","IMPRINT",EDGE,{"derivedFrom":subQ0}),1.0]])]});}
            var Q14;
            {var subQ0=sQuery(id+"F0.wireOp",EDGE,"E982");var subQ3=sQuery(id+"F0.wireOp",EDGE,"E981");var subQ4=makeQuery(id+"F0.imprint","INTERSECT",VERTEX,{"disambiguationData":[OD(0.0)],"derivedFrom":[subQ3,subQ0]});Q14=makeQuery(id+"F0.imprint","IMPRINT",FACE,{"disambiguationData":[TD([[makeQuery(id+"F0.imprint","IMPRINT",EDGE,{"disambiguationData":[TD([[subQ4,-1.0]])],"derivedFrom":subQ3}),-1.0]])]});}
            var Q15;
            {var subQ0=sQuery(id+"F0.wireOp",EDGE,"E938");Q15=makeQuery(id+"F0.imprint","IMPRINT",FACE,{"disambiguationData":[TD([[makeQuery(id+"F0.imprint","IMPRINT",EDGE,{"derivedFrom":subQ0}),1.0]])]});}
            var Q16;
            Q16=makeQuery(id+"F0.imprint","IMPRINT",FACE,{"disambiguationData":[TD([[makeQuery(id+"F0.imprint","IMPRINT",EDGE,{"derivedFrom":sQuery(id+"F0.wireOp",EDGE,"E917")}),1.0]])]});
            var Q17;
            Q17=makeQuery(id+"F0.imprint","IMPRINT",FACE,{"disambiguationData":[TD([[makeQuery(id+"F0.imprint","IMPRINT",EDGE,{"derivedFrom":sQuery(id+"F0.wireOp",EDGE,"E162")}),-1.0]])]});
            var Q18;
            Q18=makeQuery(id+"F0.imprint","IMPRINT",FACE,{"disambiguationData":[TD([[makeQuery(id+"F0.imprint","IMPRINT",EDGE,{"derivedFrom":sQuery(id+"F0.wireOp",EDGE,"E152")}),-1.0]])]});
            var Q19;
            Q19=makeQuery(id+"F0.imprint","IMPRINT",FACE,{"disambiguationData":[TD([[makeQuery(id+"F0.imprint","IMPRINT",EDGE,{"derivedFrom":sQuery(id+"F0.wireOp",EDGE,"E141")}),-1.0]])]});
            var Q20;
            Q20=makeQuery(id+"F0.imprint","IMPRINT",FACE,{"disambiguationData":[TD([[makeQuery(id+"F0.imprint","IMPRINT",EDGE,{"derivedFrom":sQuery(id+"F0.wireOp",EDGE,"E143")}),1.0]])]});
            var Q21;
            Q21=makeQuery(id+"F0.imprint","IMPRINT",FACE,{"disambiguationData":[TD([[makeQuery(id+"F0.imprint","IMPRINT",EDGE,{"derivedFrom":sQuery(id+"F0.wireOp",EDGE,"E131")}),-1.0]])]});
            var Q22;
            Q22=makeQuery(id+"F0.imprint","IMPRINT",FACE,{"disambiguationData":[TD([[makeQuery(id+"F0.imprint","IMPRINT",EDGE,{"derivedFrom":sQuery(id+"F0.wireOp",EDGE,"E127")}),-1.0]])]});
            var Q23;
            Q23=makeQuery(id+"F0.imprint","IMPRINT",FACE,{"disambiguationData":[TD([[makeQuery(id+"F0.imprint","IMPRINT",EDGE,{"derivedFrom":sQuery(id+"F0.wireOp",EDGE,"E129")}),1.0]])]});
            var Q24;
            Q24=makeQuery(id+"F0.imprint","IMPRINT",FACE,{"disambiguationData":[TD([[makeQuery(id+"F0.imprint","IMPRINT",EDGE,{"derivedFrom":sQuery(id+"F0.wireOp",EDGE,"E205")}),-1.0]])]});
            var Q25;
            Q25=makeQuery(id+"F0.imprint","IMPRINT",FACE,{"disambiguationData":[TD([[makeQuery(id+"F0.imprint","IMPRINT",EDGE,{"derivedFrom":sQuery(id+"F0.wireOp",EDGE,"E207")}),1.0]])]});
            var Q26;
            Q26=makeQuery(id+"F0.imprint","IMPRINT",FACE,{"disambiguationData":[TD([[makeQuery(id+"F0.imprint","IMPRINT",EDGE,{"derivedFrom":sQuery(id+"F0.wireOp",EDGE,"E195")}),-1.0]])]});
            var Q27;
            Q27=makeQuery(id+"F0.imprint","IMPRINT",FACE,{"disambiguationData":[TD([[makeQuery(id+"F0.imprint","IMPRINT",EDGE,{"derivedFrom":sQuery(id+"F0.wireOp",EDGE,"E184")}),-1.0]])]});
            var Q28;
            Q28=makeQuery(id+"F0.imprint","IMPRINT",FACE,{"disambiguationData":[TD([[makeQuery(id+"F0.imprint","IMPRINT",EDGE,{"derivedFrom":sQuery(id+"F0.wireOp",EDGE,"E186")}),1.0]])]});
            var Q29;
            Q29=makeQuery(id+"F0.imprint","IMPRINT",FACE,{"disambiguationData":[TD([[makeQuery(id+"F0.imprint","IMPRINT",EDGE,{"derivedFrom":sQuery(id+"F0.wireOp",EDGE,"E191")}),1.0]])]});
            var Q30;
            Q30=makeQuery(id+"F0.imprint","IMPRINT",FACE,{"disambiguationData":[TD([[makeQuery(id+"F0.imprint","IMPRINT",EDGE,{"derivedFrom":sQuery(id+"F0.wireOp",EDGE,"E105")}),1.0]])]});
            var Q31;
            Q31=makeQuery(id+"F0.imprint","IMPRINT",FACE,{"disambiguationData":[TD([[makeQuery(id+"F0.imprint","IMPRINT",EDGE,{"derivedFrom":sQuery(id+"F0.wireOp",EDGE,"E107")}),1.0]])]});
            var Q32;
            Q32=makeQuery(id+"F0.imprint","IMPRINT",FACE,{"disambiguationData":[TD([[makeQuery(id+"F0.imprint","IMPRINT",EDGE,{"derivedFrom":sQuery(id+"F0.wireOp",EDGE,"E117")}),1.0]])]});
            var Q33;
            Q33=makeQuery(id+"F0.imprint","IMPRINT",FACE,{"disambiguationData":[TD([[makeQuery(id+"F0.imprint","IMPRINT",EDGE,{"derivedFrom":sQuery(id+"F0.wireOp",EDGE,"E585")}),-1.0]])]});
            var Q34;
            Q34=makeQuery(id+"F0.imprint","IMPRINT",FACE,{"disambiguationData":[TD([[makeQuery(id+"F0.imprint","IMPRINT",EDGE,{"derivedFrom":sQuery(id+"F0.wireOp",EDGE,"E740")}),-1.0]])]});
            var Q35;
            Q35=makeQuery(id+"F0.imprint","IMPRINT",FACE,{"disambiguationData":[TD([[makeQuery(id+"F0.imprint","IMPRINT",EDGE,{"derivedFrom":sQuery(id+"F0.wireOp",EDGE,"E736")}),-1.0]])]});
            var Q36;
            {var subQ3=sQuery(id+"F0.wireOp",EDGE,"E764");Q36=makeQuery(id+"F0.imprint","IMPRINT",FACE,{"disambiguationData":[TD([[makeQuery(id+"F0.imprint","IMPRINT",EDGE,{"derivedFrom":subQ3}),-1.0]])]});}
            var Q37;
            {var subQ1=sQuery(id+"F0.wireOp",EDGE,"E732");var subQ13=makeQuery(id+"F0.imprint","IMPRINT",VERTEX,{"disambiguationData":[OD(0.0)],"derivedFrom":subQ1});Q37=makeQuery(id+"F0.imprint","IMPRINT",FACE,{"disambiguationData":[TD([[makeQuery(id+"F0.imprint","IMPRINT",EDGE,{"disambiguationData":[TD([[subQ13,-1.0]])],"derivedFrom":subQ1}),-1.0]])]});}
            var Q38;
            {var subQ3=sQuery(id+"F0.wireOp",EDGE,"E760");Q38=makeQuery(id+"F0.imprint","IMPRINT",FACE,{"disambiguationData":[TD([[makeQuery(id+"F0.imprint","IMPRINT",EDGE,{"derivedFrom":subQ3}),-1.0]])]});}
            var Q39;
            {var subQ3=sQuery(id+"F0.wireOp",EDGE,"E756");Q39=makeQuery(id+"F0.imprint","IMPRINT",FACE,{"disambiguationData":[TD([[makeQuery(id+"F0.imprint","IMPRINT",EDGE,{"derivedFrom":subQ3}),-1.0]])]});}
            var Q40;
            Q40=makeQuery(id+"F0.imprint","IMPRINT",FACE,{"disambiguationData":[TD([[makeQuery(id+"F0.imprint","IMPRINT",EDGE,{"derivedFrom":sQuery(id+"F0.wireOp",EDGE,"E900")}),1.0]])]});
            var Q41;
            Q41=makeQuery(id+"F0.imprint","IMPRINT",FACE,{"disambiguationData":[TD([[makeQuery(id+"F0.imprint","IMPRINT",EDGE,{"derivedFrom":sQuery(id+"F0.wireOp",EDGE,"E941")}),-1.0]])]});
            var Q42;
            Q42=makeQuery(id+"F0.imprint","IMPRINT",FACE,{"disambiguationData":[TD([[makeQuery(id+"F0.imprint","IMPRINT",EDGE,{"derivedFrom":sQuery(id+"F0.wireOp",EDGE,"E945")}),-1.0]])]});
            var Q43;
            Q43=makeQuery(id+"F0.imprint","IMPRINT",FACE,{"disambiguationData":[TD([[makeQuery(id+"F0.imprint","IMPRINT",EDGE,{"derivedFrom":sQuery(id+"F0.wireOp",EDGE,"E949")}),-1.0]])]});
            var Q44;
            Q44=makeQuery(id+"F0.imprint","IMPRINT",FACE,{"disambiguationData":[TD([[makeQuery(id+"F0.imprint","IMPRINT",EDGE,{"derivedFrom":sQuery(id+"F0.wireOp",EDGE,"E953")}),-1.0]])]});
            var Q45;
            Q45=makeQuery(id+"F0.imprint","IMPRINT",FACE,{"disambiguationData":[TD([[makeQuery(id+"F0.imprint","IMPRINT",EDGE,{"derivedFrom":sQuery(id+"F0.wireOp",EDGE,"E957")}),-1.0]])]});
            var Q46;
            Q46=makeQuery(id+"F0.imprint","IMPRINT",FACE,{"disambiguationData":[TD([[makeQuery(id+"F0.imprint","IMPRINT",EDGE,{"derivedFrom":sQuery(id+"F0.wireOp",EDGE,"E961")}),-1.0]])]});
            var Q47;
            Q47=makeQuery(id+"F0.imprint","IMPRINT",FACE,{"disambiguationData":[TD([[makeQuery(id+"F0.imprint","IMPRINT",EDGE,{"derivedFrom":sQuery(id+"F0.wireOp",EDGE,"E965")}),-1.0]])]});
            var Q48;
            Q48=makeQuery(id+"F0.imprint","IMPRINT",FACE,{"disambiguationData":[TD([[makeQuery(id+"F0.imprint","IMPRINT",EDGE,{"derivedFrom":sQuery(id+"F0.wireOp",EDGE,"E969")}),-1.0]])]});
            var Q49;
            Q49=makeQuery(id+"F0.imprint","IMPRINT",FACE,{"disambiguationData":[TD([[makeQuery(id+"F0.imprint","IMPRINT",EDGE,{"derivedFrom":sQuery(id+"F0.wireOp",EDGE,"E973")}),-1.0]])]});
            var Q50;
            Q50=makeQuery(id+"F0.imprint","IMPRINT",FACE,{"disambiguationData":[TD([[makeQuery(id+"F0.imprint","IMPRINT",EDGE,{"derivedFrom":sQuery(id+"F0.wireOp",EDGE,"E977")}),-1.0]])]});
            var Q51;
            Q51=makeQuery(id+"F0.imprint","IMPRINT",FACE,{"disambiguationData":[TD([[makeQuery(id+"F0.imprint","IMPRINT",EDGE,{"derivedFrom":sQuery(id+"F0.wireOp",EDGE,"E883")}),-1.0]])]});
            var Q52;
            {var subQ4=sQuery(id+"F0.wireOp",EDGE,"E9");Q52=makeQuery(id+"F0.imprint","IMPRINT",FACE,{"disambiguationData":[TD([[makeQuery(id+"F0.imprint","IMPRINT",EDGE,{"derivedFrom":subQ4}),1.0]])]});}
            var Q53;
            {var subQ2=sQuery(id+"F0.wireOp",EDGE,"E938");Q53=makeQuery(id+"F0.imprint","IMPRINT",FACE,{"disambiguationData":[TD([[makeQuery(id+"F0.imprint","IMPRINT",EDGE,{"derivedFrom":subQ2}),-1.0]])]});}
            var Q54;
            Q54=makeQuery(id+"F0.imprint","IMPRINT",FACE,{"disambiguationData":[TD([[makeQuery(id+"F0.imprint","IMPRINT",EDGE,{"derivedFrom":sQuery(id+"F0.wireOp",EDGE,"E301")}),1.0]])]});
            var Q55;
            Q55=makeQuery(id+"F0.imprint","IMPRINT",FACE,{"disambiguationData":[TD([[makeQuery(id+"F0.imprint","IMPRINT",EDGE,{"derivedFrom":sQuery(id+"F0.wireOp",EDGE,"E298")}),-1.0]])]});
            var Q56;
            Q56=makeQuery(id+"F0.imprint","IMPRINT",FACE,{"disambiguationData":[TD([[makeQuery(id+"F0.imprint","IMPRINT",EDGE,{"derivedFrom":sQuery(id+"F0.wireOp",EDGE,"E307")}),1.0]])]});
            var Q57;
            Q57=makeQuery(id+"F0.imprint","IMPRINT",FACE,{"disambiguationData":[TD([[makeQuery(id+"F0.imprint","IMPRINT",EDGE,{"derivedFrom":sQuery(id+"F0.wireOp",EDGE,"E305")}),-1.0]])]});
            var Q58;
            Q58=makeQuery(id+"F0.imprint","IMPRINT",FACE,{"disambiguationData":[TD([[makeQuery(id+"F0.imprint","IMPRINT",EDGE,{"derivedFrom":sQuery(id+"F0.wireOp",EDGE,"E316")}),-1.0]])]});
            var Q59;
            Q59=makeQuery(id+"F0.imprint","IMPRINT",FACE,{"disambiguationData":[TD([[makeQuery(id+"F0.imprint","IMPRINT",EDGE,{"derivedFrom":sQuery(id+"F0.wireOp",EDGE,"E328")}),1.0]])]});
            var Q60;
            Q60=makeQuery(id+"F0.imprint","IMPRINT",FACE,{"disambiguationData":[TD([[makeQuery(id+"F0.imprint","IMPRINT",EDGE,{"derivedFrom":sQuery(id+"F0.wireOp",EDGE,"E326")}),-1.0]])]});
            var Q61;
            Q61=makeQuery(id+"F0.imprint","IMPRINT",FACE,{"disambiguationData":[TD([[makeQuery(id+"F0.imprint","IMPRINT",EDGE,{"derivedFrom":sQuery(id+"F0.wireOp",EDGE,"E337")}),-1.0]])]});
            var Q62;
            Q62=makeQuery(id+"F0.imprint","IMPRINT",FACE,{"disambiguationData":[TD([[makeQuery(id+"F0.imprint","IMPRINT",EDGE,{"derivedFrom":sQuery(id+"F0.wireOp",EDGE,"E349")}),1.0]])]});
            var Q63;
            Q63=makeQuery(id+"F0.imprint","IMPRINT",FACE,{"disambiguationData":[TD([[makeQuery(id+"F0.imprint","IMPRINT",EDGE,{"derivedFrom":sQuery(id+"F0.wireOp",EDGE,"E347")}),-1.0]])]});
            var Q64;
            Q64=makeQuery(id+"F0.imprint","IMPRINT",FACE,{"disambiguationData":[TD([[makeQuery(id+"F0.imprint","IMPRINT",EDGE,{"derivedFrom":sQuery(id+"F0.wireOp",EDGE,"E229")}),1.0]])]});
            var Q65;
            Q65=makeQuery(id+"F0.imprint","IMPRINT",FACE,{"disambiguationData":[TD([[makeQuery(id+"F0.imprint","IMPRINT",EDGE,{"derivedFrom":sQuery(id+"F0.wireOp",EDGE,"E227")}),-1.0]])]});
            var Q66;
            Q66=makeQuery(id+"F0.imprint","IMPRINT",FACE,{"disambiguationData":[TD([[makeQuery(id+"F0.imprint","IMPRINT",EDGE,{"derivedFrom":sQuery(id+"F0.wireOp",EDGE,"E231")}),-1.0]])]});
            var Q67;
            Q67=makeQuery(id+"F0.imprint","IMPRINT",FACE,{"disambiguationData":[TD([[makeQuery(id+"F0.imprint","IMPRINT",EDGE,{"derivedFrom":sQuery(id+"F0.wireOp",EDGE,"E243")}),1.0]])]});
            var Q68;
            Q68=makeQuery(id+"F0.imprint","IMPRINT",FACE,{"disambiguationData":[TD([[makeQuery(id+"F0.imprint","IMPRINT",EDGE,{"derivedFrom":sQuery(id+"F0.wireOp",EDGE,"E241")}),-1.0]])]});
            var Q69;
            Q69=makeQuery(id+"F0.imprint","IMPRINT",FACE,{"disambiguationData":[TD([[makeQuery(id+"F0.imprint","IMPRINT",EDGE,{"derivedFrom":sQuery(id+"F0.wireOp",EDGE,"E252")}),-1.0]])]});
            var Q70;
            Q70=makeQuery(id+"F0.imprint","IMPRINT",FACE,{"disambiguationData":[TD([[makeQuery(id+"F0.imprint","IMPRINT",EDGE,{"derivedFrom":sQuery(id+"F0.wireOp",EDGE,"E264")}),1.0]])]});
            var Q71;
            Q71=makeQuery(id+"F0.imprint","IMPRINT",FACE,{"disambiguationData":[TD([[makeQuery(id+"F0.imprint","IMPRINT",EDGE,{"derivedFrom":sQuery(id+"F0.wireOp",EDGE,"E262")}),-1.0]])]});
            var Q72;
            Q72=makeQuery(id+"F0.imprint","IMPRINT",FACE,{"disambiguationData":[TD([[makeQuery(id+"F0.imprint","IMPRINT",EDGE,{"derivedFrom":sQuery(id+"F0.wireOp",EDGE,"E511")}),-1.0]])]});
            var Q73;
            Q73=makeQuery(id+"F0.imprint","IMPRINT",FACE,{"disambiguationData":[TD([[makeQuery(id+"F0.imprint","IMPRINT",EDGE,{"derivedFrom":sQuery(id+"F0.wireOp",EDGE,"E513")}),1.0]])]});
            var Q74;
            Q74=makeQuery(id+"F0.imprint","IMPRINT",FACE,{"disambiguationData":[TD([[makeQuery(id+"F0.imprint","IMPRINT",EDGE,{"derivedFrom":sQuery(id+"F0.wireOp",EDGE,"E501")}),-1.0]])]});
            var Q75;
            Q75=makeQuery(id+"F0.imprint","IMPRINT",FACE,{"disambiguationData":[TD([[makeQuery(id+"F0.imprint","IMPRINT",EDGE,{"derivedFrom":sQuery(id+"F0.wireOp",EDGE,"E490")}),-1.0]])]});
            var Q76;
            Q76=makeQuery(id+"F0.imprint","IMPRINT",FACE,{"disambiguationData":[TD([[makeQuery(id+"F0.imprint","IMPRINT",EDGE,{"derivedFrom":sQuery(id+"F0.wireOp",EDGE,"E492")}),1.0]])]});
            var Q77;
            Q77=makeQuery(id+"F0.imprint","IMPRINT",FACE,{"disambiguationData":[TD([[makeQuery(id+"F0.imprint","IMPRINT",EDGE,{"derivedFrom":sQuery(id+"F0.wireOp",EDGE,"E480")}),-1.0]])]});
            var Q78;
            Q78=makeQuery(id+"F0.imprint","IMPRINT",FACE,{"disambiguationData":[TD([[makeQuery(id+"F0.imprint","IMPRINT",EDGE,{"derivedFrom":sQuery(id+"F0.wireOp",EDGE,"E469")}),-1.0]])]});
            var Q79;
            Q79=makeQuery(id+"F0.imprint","IMPRINT",FACE,{"disambiguationData":[TD([[makeQuery(id+"F0.imprint","IMPRINT",EDGE,{"derivedFrom":sQuery(id+"F0.wireOp",EDGE,"E471")}),1.0]])]});
            var Q80;
            Q80=makeQuery(id+"F0.imprint","IMPRINT",FACE,{"disambiguationData":[TD([[makeQuery(id+"F0.imprint","IMPRINT",EDGE,{"derivedFrom":sQuery(id+"F0.wireOp",EDGE,"E459")}),-1.0]])]});
            var Q81;
            Q81=makeQuery(id+"F0.imprint","IMPRINT",FACE,{"disambiguationData":[TD([[makeQuery(id+"F0.imprint","IMPRINT",EDGE,{"derivedFrom":sQuery(id+"F0.wireOp",EDGE,"E448")}),-1.0]])]});
            var Q82;
            Q82=makeQuery(id+"F0.imprint","IMPRINT",FACE,{"disambiguationData":[TD([[makeQuery(id+"F0.imprint","IMPRINT",EDGE,{"derivedFrom":sQuery(id+"F0.wireOp",EDGE,"E450")}),1.0]])]});
            var Q83;
            Q83=makeQuery(id+"F0.imprint","IMPRINT",FACE,{"disambiguationData":[TD([[makeQuery(id+"F0.imprint","IMPRINT",EDGE,{"derivedFrom":sQuery(id+"F0.wireOp",EDGE,"E441")}),-1.0]])]});
            var Q84;
            Q84=makeQuery(id+"F0.imprint","IMPRINT",FACE,{"disambiguationData":[TD([[makeQuery(id+"F0.imprint","IMPRINT",EDGE,{"derivedFrom":sQuery(id+"F0.wireOp",EDGE,"E444")}),1.0]])]});
            var Q85;
            {var subQ0=sQuery(id+"F0.wireOp",EDGE,"252386f9-dabc-4674-b6ae-04492572d4a4");Q85=makeQuery(id+"F0.imprint","IMPRINT",FACE,{"disambiguationData":[TD([[makeQuery(id+"F0.imprint","IMPRINT",EDGE,{"derivedFrom":subQ0}),1.0]])]});}
            var Q86;
            {var subQ2=sQuery(id+"F0.wireOp",EDGE,"f6065b7d-d8b1-440b-a7fc-2817690d246a");Q86=makeQuery(id+"F0.imprint","IMPRINT",FACE,{"disambiguationData":[TD([[makeQuery(id+"F0.imprint","IMPRINT",EDGE,{"derivedFrom":subQ2}),1.0]])]});}
            var Q87;
            {var subQ0=sQuery(id+"F0.wireOp",EDGE,"7a5b22f3-aa68-411b-8e6a-b4af1a465028");Q87=makeQuery(id+"F0.imprint","IMPRINT",FACE,{"disambiguationData":[TD([[makeQuery(id+"F0.imprint","IMPRINT",EDGE,{"derivedFrom":subQ0}),1.0]])]});}
            var Q88;
            {var subQ0=sQuery(id+"F0.wireOp",EDGE,"3731301d-478a-4cb7-a1f6-3041514f356d");Q88=makeQuery(id+"F0.imprint","IMPRINT",FACE,{"disambiguationData":[TD([[makeQuery(id+"F0.imprint","IMPRINT",EDGE,{"derivedFrom":subQ0}),1.0]])]});}
            var Q89;
            {var subQ0=sQuery(id+"F0.wireOp",EDGE,"eefe6b1c-418f-4e59-aa66-084deaf969fc");Q89=makeQuery(id+"F0.imprint","IMPRINT",FACE,{"disambiguationData":[TD([[makeQuery(id+"F0.imprint","IMPRINT",EDGE,{"derivedFrom":subQ0}),1.0]])]});}
            var Q90;
            {var subQ0=sQuery(id+"F0.wireOp",EDGE,"44486e8c-84c5-4fb4-baac-4e849509ee9a");Q90=makeQuery(id+"F0.imprint","IMPRINT",FACE,{"disambiguationData":[TD([[makeQuery(id+"F0.imprint","IMPRINT",EDGE,{"derivedFrom":subQ0}),1.0]])]});}
            var Q91;
            {var subQ0=sQuery(id+"F0.wireOp",EDGE,"96f90c27-1492-453f-a3a9-e72a87e015aa");Q91=makeQuery(id+"F0.imprint","IMPRINT",FACE,{"disambiguationData":[TD([[makeQuery(id+"F0.imprint","IMPRINT",EDGE,{"derivedFrom":subQ0}),1.0]])]});}
            var Q92;
            {var subQ0=sQuery(id+"F0.wireOp",EDGE,"ef226b76-5e5c-49e5-9cb3-e6bcb19234fd");Q92=makeQuery(id+"F0.imprint","IMPRINT",FACE,{"disambiguationData":[TD([[makeQuery(id+"F0.imprint","IMPRINT",EDGE,{"derivedFrom":subQ0}),1.0]])]});}
            var Q93;
            {var subQ0=sQuery(id+"F0.wireOp",EDGE,"b9a1a632-b982-4872-94e6-f372a4a18f35");Q93=makeQuery(id+"F0.imprint","IMPRINT",FACE,{"disambiguationData":[TD([[makeQuery(id+"F0.imprint","IMPRINT",EDGE,{"derivedFrom":subQ0}),1.0]])]});}
            var Q94;
            {var subQ5=sQuery(id+"F0.wireOp",EDGE,"E914");Q94=makeQuery(id+"F0.imprint","IMPRINT",FACE,{"disambiguationData":[TD([[makeQuery(id+"F0.imprint","IMPRINT",EDGE,{"derivedFrom":subQ5}),1.0]])]});}
            var Q95;
            {var subQ5=sQuery(id+"F0.wireOp",EDGE,"E912");Q95=makeQuery(id+"F0.imprint","IMPRINT",FACE,{"disambiguationData":[TD([[makeQuery(id+"F0.imprint","IMPRINT",EDGE,{"derivedFrom":subQ5}),1.0]])]});}
            var Q96;
            {var subQ5=sQuery(id+"F0.wireOp",EDGE,"E895");Q96=makeQuery(id+"F0.imprint","IMPRINT",FACE,{"disambiguationData":[TD([[makeQuery(id+"F0.imprint","IMPRINT",EDGE,{"derivedFrom":subQ5}),-1.0]])]});}
            var Q97;
            {var subQ5=sQuery(id+"F0.wireOp",EDGE,"E897");Q97=makeQuery(id+"F0.imprint","IMPRINT",FACE,{"disambiguationData":[TD([[makeQuery(id+"F0.imprint","IMPRINT",EDGE,{"derivedFrom":subQ5}),-1.0]])]});}
            var Q98;
            {var subQ1=sQuery(id+"F0.wireOp",EDGE,"E934");Q98=makeQuery(id+"F0.imprint","IMPRINT",FACE,{"disambiguationData":[TD([[makeQuery(id+"F0.imprint","IMPRINT",EDGE,{"derivedFrom":subQ1}),1.0]])]});}
            var Q99;
            {var subQ0=sQuery(id+"F0.wireOp",EDGE,"E937");Q99=makeQuery(id+"F0.imprint","IMPRINT",FACE,{"disambiguationData":[TD([[makeQuery(id+"F0.imprint","IMPRINT",EDGE,{"derivedFrom":subQ0}),-1.0]])]});}
            extrude(context, id + "F1", {"entities" : qUnion([Q0, Q1, Q2, Q3, Q4, Q5, Q6, Q7, Q8, Q9, Q10, Q11, Q12, Q13, Q14, Q15, Q16, Q17, Q18, Q19, Q20, Q21, Q22, Q23, Q24, Q25, Q26, Q27, Q28, Q29, Q30, Q31, Q32, Q33, Q34, Q35, Q36, Q37, Q38, Q39, Q40, Q41, Q42, Q43, Q44, Q45, Q46, Q47, Q48, Q49, Q50, Q51, Q52, Q53, Q54, Q55, Q56, Q57, Q58, Q59, Q60, Q61, Q62, Q63, Q64, Q65, Q66, Q67, Q68, Q69, Q70, Q71, Q72, Q73, Q74, Q75, Q76, Q77, Q78, Q79, Q80, Q81, Q82, Q83, Q84, Q85, Q86, Q87, Q88, Q89, Q90, Q91, Q92, Q93, Q94, Q95, Q96, Q97, Q98, Q99]), "depth" : 1.6 * mm});
        }
        {
            var Q0;
            Q0=makeQuery(id+"F1.opExtrude","CAP_FACE",FACE,{"disambiguationData":[OSD([sQuery(id+"F0.wireOp",EDGE,"E0"),sQuery(id+"F0.wireOp",EDGE,"E2"),sQuery(id+"F0.wireOp",EDGE,"E4"),sQuery(id+"F0.wireOp",EDGE,"E6"),sQuery(id+"F0.wireOp",EDGE,"E7"),sQuery(id+"F0.wireOp",EDGE,"E8"),sQuery(id+"F0.wireOp",EDGE,"E11"),sQuery(id+"F0.wireOp",EDGE,"E64"),sQuery(id+"F0.wireOp",EDGE,"E648"),sQuery(id+"F0.wireOp",EDGE,"E649"),sQuery(id+"F0.wireOp",EDGE,"E650"),sQuery(id+"F0.wireOp",EDGE,"E883"),sQuery(id+"F0.wireOp",EDGE,"E884"),sQuery(id+"F0.wireOp",EDGE,"E885"),sQuery(id+"F0.wireOp",EDGE,"E886"),sQuery(id+"F0.wireOp",EDGE,"E887"),sQuery(id+"F0.wireOp",EDGE,"E888"),sQuery(id+"F0.wireOp",EDGE,"E889"),sQuery(id+"F0.wireOp",EDGE,"E890"),sQuery(id+"F0.wireOp",EDGE,"E891"),sQuery(id+"F0.wireOp",EDGE,"E892"),sQuery(id+"F0.wireOp",EDGE,"E898"),sQuery(id+"F0.wireOp",EDGE,"E900"),sQuery(id+"F0.wireOp",EDGE,"E901"),sQuery(id+"F0.wireOp",EDGE,"E902"),sQuery(id+"F0.wireOp",EDGE,"E903"),sQuery(id+"F0.wireOp",EDGE,"E904"),sQuery(id+"F0.wireOp",EDGE,"E905"),sQuery(id+"F0.wireOp",EDGE,"E906"),sQuery(id+"F0.wireOp",EDGE,"E907"),sQuery(id+"F0.wireOp",EDGE,"E908"),sQuery(id+"F0.wireOp",EDGE,"E909"),sQuery(id+"F0.wireOp",EDGE,"E915"),sQuery(id+"F0.wireOp",EDGE,"E919"),sQuery(id+"F0.wireOp",EDGE,"E922"),sQuery(id+"F0.wireOp",EDGE,"E923"),sQuery(id+"F0.wireOp",EDGE,"E924"),sQuery(id+"F0.wireOp",EDGE,"E925"),sQuery(id+"F0.wireOp",EDGE,"E926"),sQuery(id+"F0.wireOp",EDGE,"E927"),sQuery(id+"F0.wireOp",EDGE,"E928"),sQuery(id+"F0.wireOp",EDGE,"E929"),sQuery(id+"F0.wireOp",EDGE,"E930"),sQuery(id+"F0.wireOp",EDGE,"E931"),sQuery(id+"F0.wireOp",EDGE,"E932"),sQuery(id+"F0.wireOp",EDGE,"E934"),sQuery(id+"F0.wireOp",EDGE,"E942"),sQuery(id+"F0.wireOp",EDGE,"E946"),sQuery(id+"F0.wireOp",EDGE,"E950"),sQuery(id+"F0.wireOp",EDGE,"E954"),sQuery(id+"F0.wireOp",EDGE,"E958"),sQuery(id+"F0.wireOp",EDGE,"E962"),sQuery(id+"F0.wireOp",EDGE,"E966"),sQuery(id+"F0.wireOp",EDGE,"E970"),sQuery(id+"F0.wireOp",EDGE,"E974"),sQuery(id+"F0.wireOp",EDGE,"E978"),sQuery(id+"F0.wireOp",EDGE,"E981"),sQuery(id+"F0.wireOp",EDGE,"E983"),sQuery(id+"F0.wireOp",EDGE,"E984")])],"isStart":false});
            var sketch = newSketch(context, id + "F2", { "sketchPlane" : qUnion([Q0])});
            skLineSegment(sketch, "E989.bottom", {"start": v(-41.68, 15.24) * mm, "end": v(-27.2, 15.24) * mm});
            skLineSegment(sketch, "E989.top", {"start": v(-41.68, 9.25) * mm, "end": v(-27.2, 9.25) * mm});
            skLineSegment(sketch, "E989.left", {"start": v(-41.68, 15.24) * mm, "end": v(-41.68, 9.25) * mm});
            skLineSegment(sketch, "E989.right", {"start": v(-27.2, 15.24) * mm, "end": v(-27.2, 9.25) * mm});
            skSolve(sketch);
        }
        {
            var Q0;
            Q0 = qSketchRegion(id + "F2", true);
            extrude(context, id + "F3", {"entities" : qUnion([Q0]), "operationType" : NewBodyOperationType.ADD, "depth" : 5 * mm});
        }
        {
            var Q0;
            Q0=makeQuery(id+"F3.boolean.opBoolean","MERGE",FACE,{"derivedFrom":[makeQuery(id+"F1.opExtrude","SWEPT_FACE",FACE,{"disambiguationData":[OSD([sQuery(id+"F0.wireOp",EDGE,"E0"),sQuery(id+"F0.wireOp",EDGE,"E648"),sQuery(id+"F0.wireOp",EDGE,"E649"),sQuery(id+"F0.wireOp",EDGE,"E650"),sQuery(id+"F0.wireOp",EDGE,"E898"),sQuery(id+"F0.wireOp",EDGE,"E919"),sQuery(id+"F0.wireOp",EDGE,"E932"),sQuery(id+"F0.wireOp",EDGE,"E934")])]}),makeQuery(id+"F3.opExtrude","SWEPT_FACE",FACE,{"disambiguationData":[OSD([sQuery(id+"F2.wireOp",EDGE,"E989.left")])]})]});
            var sketch = newSketch(context, id + "F4", { "sketchPlane" : qUnion([Q0])});
            skCircle(sketch, "E990", {"center": v(-12.24, 4.1) * mm, "radius": 2.5 * mm});
            skLineSegment(sketch, "E991", {"start": v(-12.24, 6.6) * mm, "end": v(-12.24, 4.1) * mm, "construction": true});
            skLineSegment(sketch, "E992", {"start": v(-15.24, 4.1) * mm, "end": v(-12.24, 4.1) * mm, "construction": true});
            skCircle(sketch, "E993", {"center": v(-12.24, 4.1) * mm, "radius": 1.8 * mm});
            skSolve(sketch);
        }
        {
            var Q0;
            Q0=makeQuery(id+"F1.opExtrude","CAP_FACE",FACE,{"disambiguationData":[OSD([sQuery(id+"F0.wireOp",EDGE,"E0"),sQuery(id+"F0.wireOp",EDGE,"E2"),sQuery(id+"F0.wireOp",EDGE,"E4"),sQuery(id+"F0.wireOp",EDGE,"E6"),sQuery(id+"F0.wireOp",EDGE,"E7"),sQuery(id+"F0.wireOp",EDGE,"E8"),sQuery(id+"F0.wireOp",EDGE,"E11"),sQuery(id+"F0.wireOp",EDGE,"E64"),sQuery(id+"F0.wireOp",EDGE,"E648"),sQuery(id+"F0.wireOp",EDGE,"E649"),sQuery(id+"F0.wireOp",EDGE,"E650"),sQuery(id+"F0.wireOp",EDGE,"E883"),sQuery(id+"F0.wireOp",EDGE,"E884"),sQuery(id+"F0.wireOp",EDGE,"E885"),sQuery(id+"F0.wireOp",EDGE,"E886"),sQuery(id+"F0.wireOp",EDGE,"E887"),sQuery(id+"F0.wireOp",EDGE,"E888"),sQuery(id+"F0.wireOp",EDGE,"E889"),sQuery(id+"F0.wireOp",EDGE,"E890"),sQuery(id+"F0.wireOp",EDGE,"E891"),sQuery(id+"F0.wireOp",EDGE,"E892"),sQuery(id+"F0.wireOp",EDGE,"E898"),sQuery(id+"F0.wireOp",EDGE,"E900"),sQuery(id+"F0.wireOp",EDGE,"E901"),sQuery(id+"F0.wireOp",EDGE,"E902"),sQuery(id+"F0.wireOp",EDGE,"E903"),sQuery(id+"F0.wireOp",EDGE,"E904"),sQuery(id+"F0.wireOp",EDGE,"E905"),sQuery(id+"F0.wireOp",EDGE,"E906"),sQuery(id+"F0.wireOp",EDGE,"E907"),sQuery(id+"F0.wireOp",EDGE,"E908"),sQuery(id+"F0.wireOp",EDGE,"E909"),sQuery(id+"F0.wireOp",EDGE,"E915"),sQuery(id+"F0.wireOp",EDGE,"E919"),sQuery(id+"F0.wireOp",EDGE,"E922"),sQuery(id+"F0.wireOp",EDGE,"E923"),sQuery(id+"F0.wireOp",EDGE,"E924"),sQuery(id+"F0.wireOp",EDGE,"E925"),sQuery(id+"F0.wireOp",EDGE,"E926"),sQuery(id+"F0.wireOp",EDGE,"E927"),sQuery(id+"F0.wireOp",EDGE,"E928"),sQuery(id+"F0.wireOp",EDGE,"E929"),sQuery(id+"F0.wireOp",EDGE,"E930"),sQuery(id+"F0.wireOp",EDGE,"E931"),sQuery(id+"F0.wireOp",EDGE,"E932"),sQuery(id+"F0.wireOp",EDGE,"E934"),sQuery(id+"F0.wireOp",EDGE,"E942"),sQuery(id+"F0.wireOp",EDGE,"E946"),sQuery(id+"F0.wireOp",EDGE,"E950"),sQuery(id+"F0.wireOp",EDGE,"E954"),sQuery(id+"F0.wireOp",EDGE,"E958"),sQuery(id+"F0.wireOp",EDGE,"E962"),sQuery(id+"F0.wireOp",EDGE,"E966"),sQuery(id+"F0.wireOp",EDGE,"E970"),sQuery(id+"F0.wireOp",EDGE,"E974"),sQuery(id+"F0.wireOp",EDGE,"E978"),sQuery(id+"F0.wireOp",EDGE,"E981"),sQuery(id+"F0.wireOp",EDGE,"E983"),sQuery(id+"F0.wireOp",EDGE,"E984")])],"isStart":false});
            var sketch = newSketch(context, id + "F5", { "sketchPlane" : qUnion([Q0])});
            skLineSegment(sketch, "E994.bottom", {"start": v(-23.92, 7.2) * mm, "end": v(-38.71, 7.2) * mm});
            skLineSegment(sketch, "E994.top", {"start": v(-23.92, -6.78) * mm, "end": v(-38.71, -6.78) * mm});
            skLineSegment(sketch, "E994.left", {"start": v(-23.92, 7.2) * mm, "end": v(-23.92, -6.78) * mm});
            skLineSegment(sketch, "E994.right", {"start": v(-38.71, 7.2) * mm, "end": v(-38.71, -6.78) * mm});
            skSolve(sketch);
        }
        {
            var Q0;
            Q0 = qSketchRegion(id + "F5", true);
            extrude(context, id + "F6", {"entities" : qUnion([Q0]), "operationType" : NewBodyOperationType.ADD, "depth" : 2 * mm});
        }
        {
            var Q0;
            Q0=makeQuery(id+"F1.opExtrude","CAP_FACE",FACE,{"disambiguationData":[OSD([sQuery(id+"F0.wireOp",EDGE,"E0"),sQuery(id+"F0.wireOp",EDGE,"E2"),sQuery(id+"F0.wireOp",EDGE,"E4"),sQuery(id+"F0.wireOp",EDGE,"E6"),sQuery(id+"F0.wireOp",EDGE,"E7"),sQuery(id+"F0.wireOp",EDGE,"E8"),sQuery(id+"F0.wireOp",EDGE,"E11"),sQuery(id+"F0.wireOp",EDGE,"E64"),sQuery(id+"F0.wireOp",EDGE,"E648"),sQuery(id+"F0.wireOp",EDGE,"E649"),sQuery(id+"F0.wireOp",EDGE,"E650"),sQuery(id+"F0.wireOp",EDGE,"E883"),sQuery(id+"F0.wireOp",EDGE,"E884"),sQuery(id+"F0.wireOp",EDGE,"E885"),sQuery(id+"F0.wireOp",EDGE,"E886"),sQuery(id+"F0.wireOp",EDGE,"E887"),sQuery(id+"F0.wireOp",EDGE,"E888"),sQuery(id+"F0.wireOp",EDGE,"E889"),sQuery(id+"F0.wireOp",EDGE,"E890"),sQuery(id+"F0.wireOp",EDGE,"E891"),sQuery(id+"F0.wireOp",EDGE,"E892"),sQuery(id+"F0.wireOp",EDGE,"E898"),sQuery(id+"F0.wireOp",EDGE,"E900"),sQuery(id+"F0.wireOp",EDGE,"E901"),sQuery(id+"F0.wireOp",EDGE,"E902"),sQuery(id+"F0.wireOp",EDGE,"E903"),sQuery(id+"F0.wireOp",EDGE,"E904"),sQuery(id+"F0.wireOp",EDGE,"E905"),sQuery(id+"F0.wireOp",EDGE,"E906"),sQuery(id+"F0.wireOp",EDGE,"E907"),sQuery(id+"F0.wireOp",EDGE,"E908"),sQuery(id+"F0.wireOp",EDGE,"E909"),sQuery(id+"F0.wireOp",EDGE,"E915"),sQuery(id+"F0.wireOp",EDGE,"E919"),sQuery(id+"F0.wireOp",EDGE,"E922"),sQuery(id+"F0.wireOp",EDGE,"E923"),sQuery(id+"F0.wireOp",EDGE,"E924"),sQuery(id+"F0.wireOp",EDGE,"E925"),sQuery(id+"F0.wireOp",EDGE,"E926"),sQuery(id+"F0.wireOp",EDGE,"E927"),sQuery(id+"F0.wireOp",EDGE,"E928"),sQuery(id+"F0.wireOp",EDGE,"E929"),sQuery(id+"F0.wireOp",EDGE,"E930"),sQuery(id+"F0.wireOp",EDGE,"E931"),sQuery(id+"F0.wireOp",EDGE,"E932"),sQuery(id+"F0.wireOp",EDGE,"E934"),sQuery(id+"F0.wireOp",EDGE,"E942"),sQuery(id+"F0.wireOp",EDGE,"E946"),sQuery(id+"F0.wireOp",EDGE,"E950"),sQuery(id+"F0.wireOp",EDGE,"E954"),sQuery(id+"F0.wireOp",EDGE,"E958"),sQuery(id+"F0.wireOp",EDGE,"E962"),sQuery(id+"F0.wireOp",EDGE,"E966"),sQuery(id+"F0.wireOp",EDGE,"E970"),sQuery(id+"F0.wireOp",EDGE,"E974"),sQuery(id+"F0.wireOp",EDGE,"E978"),sQuery(id+"F0.wireOp",EDGE,"E981"),sQuery(id+"F0.wireOp",EDGE,"E983"),sQuery(id+"F0.wireOp",EDGE,"E984")])],"isStart":false});
            var sketch = newSketch(context, id + "F7", { "sketchPlane" : qUnion([Q0])});
            skLineSegment(sketch, "E995.bottom", {"start": v(-36.99, -8.78) * mm, "end": v(-42.06, -8.78) * mm});
            skLineSegment(sketch, "E995.top", {"start": v(-36.99, -15.88) * mm, "end": v(-42.06, -15.88) * mm});
            skLineSegment(sketch, "E995.left", {"start": v(-36.99, -8.78) * mm, "end": v(-36.99, -15.88) * mm});
            skLineSegment(sketch, "E995.right", {"start": v(-42.06, -8.78) * mm, "end": v(-42.06, -15.88) * mm});
            skSolve(sketch);
        }
        {
            var Q0;
            Q0 = qSketchRegion(id + "F7", true);
            extrude(context, id + "F8", {"entities" : qUnion([Q0]), "operationType" : NewBodyOperationType.ADD, "depth" : 2.6 * mm});
        }
        {
            var Q0;
            Q0 = qSketchRegion(id + "F4", true);
            var Q1;
            Q1=sQuery(id+"F0.wireOp",VERTEX,"E652.start");
            extrude(context, id + "F9", {"entities" : qUnion([Q0]), "operationType" : NewBodyOperationType.ADD, "endBound" : BoundingType.UP_TO_VERTEX, "endBoundEntityVertex" : qUnion([Q1]), "depth" : 25 * mm});
        }
        {
            var Q0;
            Q0=makeQuery(id+"F1.opExtrude","CAP_FACE",FACE,{"disambiguationData":[OSD([sQuery(id+"F0.wireOp",EDGE,"E0"),sQuery(id+"F0.wireOp",EDGE,"E2"),sQuery(id+"F0.wireOp",EDGE,"E4"),sQuery(id+"F0.wireOp",EDGE,"E6"),sQuery(id+"F0.wireOp",EDGE,"E7"),sQuery(id+"F0.wireOp",EDGE,"E8"),sQuery(id+"F0.wireOp",EDGE,"E11"),sQuery(id+"F0.wireOp",EDGE,"E64"),sQuery(id+"F0.wireOp",EDGE,"E648"),sQuery(id+"F0.wireOp",EDGE,"E649"),sQuery(id+"F0.wireOp",EDGE,"E650"),sQuery(id+"F0.wireOp",EDGE,"E883"),sQuery(id+"F0.wireOp",EDGE,"E884"),sQuery(id+"F0.wireOp",EDGE,"E885"),sQuery(id+"F0.wireOp",EDGE,"E886"),sQuery(id+"F0.wireOp",EDGE,"E887"),sQuery(id+"F0.wireOp",EDGE,"E888"),sQuery(id+"F0.wireOp",EDGE,"E889"),sQuery(id+"F0.wireOp",EDGE,"E890"),sQuery(id+"F0.wireOp",EDGE,"E891"),sQuery(id+"F0.wireOp",EDGE,"E892"),sQuery(id+"F0.wireOp",EDGE,"E898"),sQuery(id+"F0.wireOp",EDGE,"E900"),sQuery(id+"F0.wireOp",EDGE,"E901"),sQuery(id+"F0.wireOp",EDGE,"E902"),sQuery(id+"F0.wireOp",EDGE,"E903"),sQuery(id+"F0.wireOp",EDGE,"E904"),sQuery(id+"F0.wireOp",EDGE,"E905"),sQuery(id+"F0.wireOp",EDGE,"E906"),sQuery(id+"F0.wireOp",EDGE,"E907"),sQuery(id+"F0.wireOp",EDGE,"E908"),sQuery(id+"F0.wireOp",EDGE,"E909"),sQuery(id+"F0.wireOp",EDGE,"E915"),sQuery(id+"F0.wireOp",EDGE,"E919"),sQuery(id+"F0.wireOp",EDGE,"E922"),sQuery(id+"F0.wireOp",EDGE,"E923"),sQuery(id+"F0.wireOp",EDGE,"E924"),sQuery(id+"F0.wireOp",EDGE,"E925"),sQuery(id+"F0.wireOp",EDGE,"E926"),sQuery(id+"F0.wireOp",EDGE,"E927"),sQuery(id+"F0.wireOp",EDGE,"E928"),sQuery(id+"F0.wireOp",EDGE,"E929"),sQuery(id+"F0.wireOp",EDGE,"E930"),sQuery(id+"F0.wireOp",EDGE,"E931"),sQuery(id+"F0.wireOp",EDGE,"E932"),sQuery(id+"F0.wireOp",EDGE,"E934"),sQuery(id+"F0.wireOp",EDGE,"E942"),sQuery(id+"F0.wireOp",EDGE,"E946"),sQuery(id+"F0.wireOp",EDGE,"E950"),sQuery(id+"F0.wireOp",EDGE,"E954"),sQuery(id+"F0.wireOp",EDGE,"E958"),sQuery(id+"F0.wireOp",EDGE,"E962"),sQuery(id+"F0.wireOp",EDGE,"E966"),sQuery(id+"F0.wireOp",EDGE,"E970"),sQuery(id+"F0.wireOp",EDGE,"E974"),sQuery(id+"F0.wireOp",EDGE,"E978"),sQuery(id+"F0.wireOp",EDGE,"E981"),sQuery(id+"F0.wireOp",EDGE,"E983"),sQuery(id+"F0.wireOp",EDGE,"E984")])],"isStart":false});
            var sketch = newSketch(context, id + "F10", { "sketchPlane" : qUnion([Q0])});
            skLineSegment(sketch, "E996", {"start": v(-33.7, -17.7) * mm, "end": v(-41.68, -17.7) * mm});
            skLineSegment(sketch, "E997", {"start": v(-41.68, -17.7) * mm, "end": v(-41.68, -25.68) * mm});
            skLineSegment(sketch, "E998", {"start": v(-41.68, -25.68) * mm, "end": v(-33.7, -25.68) * mm});
            skLineSegment(sketch, "E999", {"start": v(-33.7, -25.68) * mm, "end": v(-33.7, -24.88) * mm});
            skLineSegment(sketch, "E1000", {"start": v(-33.7, -24.88) * mm, "end": v(-36.2, -24.88) * mm});
            skLineSegment(sketch, "E1001", {"start": v(-36.2, -24.88) * mm, "end": v(-36.2, -18.5) * mm});
            skLineSegment(sketch, "E1002", {"start": v(-36.2, -18.5) * mm, "end": v(-33.7, -18.5) * mm});
            skLineSegment(sketch, "E1003", {"start": v(-33.7, -18.5) * mm, "end": v(-33.7, -17.7) * mm});
            skSolve(sketch);
        }
        {
            var Q0;
            Q0 = qSketchRegion(id + "F10", true);
            extrude(context, id + "F11", {"entities" : qUnion([Q0]), "operationType" : NewBodyOperationType.ADD, "depth" : 5.5 * mm});
        }
        {
            var Q0;
            Q0=makeQuery(id+"F1.opExtrude","CAP_FACE",FACE,{"disambiguationData":[OSD([sQuery(id+"F0.wireOp",EDGE,"E0"),sQuery(id+"F0.wireOp",EDGE,"E2"),sQuery(id+"F0.wireOp",EDGE,"E4"),sQuery(id+"F0.wireOp",EDGE,"E6"),sQuery(id+"F0.wireOp",EDGE,"E7"),sQuery(id+"F0.wireOp",EDGE,"E8"),sQuery(id+"F0.wireOp",EDGE,"E11"),sQuery(id+"F0.wireOp",EDGE,"E64"),sQuery(id+"F0.wireOp",EDGE,"E648"),sQuery(id+"F0.wireOp",EDGE,"E649"),sQuery(id+"F0.wireOp",EDGE,"E650"),sQuery(id+"F0.wireOp",EDGE,"E883"),sQuery(id+"F0.wireOp",EDGE,"E884"),sQuery(id+"F0.wireOp",EDGE,"E885"),sQuery(id+"F0.wireOp",EDGE,"E886"),sQuery(id+"F0.wireOp",EDGE,"E887"),sQuery(id+"F0.wireOp",EDGE,"E888"),sQuery(id+"F0.wireOp",EDGE,"E889"),sQuery(id+"F0.wireOp",EDGE,"E890"),sQuery(id+"F0.wireOp",EDGE,"E891"),sQuery(id+"F0.wireOp",EDGE,"E892"),sQuery(id+"F0.wireOp",EDGE,"E898"),sQuery(id+"F0.wireOp",EDGE,"E900"),sQuery(id+"F0.wireOp",EDGE,"E901"),sQuery(id+"F0.wireOp",EDGE,"E902"),sQuery(id+"F0.wireOp",EDGE,"E903"),sQuery(id+"F0.wireOp",EDGE,"E904"),sQuery(id+"F0.wireOp",EDGE,"E905"),sQuery(id+"F0.wireOp",EDGE,"E906"),sQuery(id+"F0.wireOp",EDGE,"E907"),sQuery(id+"F0.wireOp",EDGE,"E908"),sQuery(id+"F0.wireOp",EDGE,"E909"),sQuery(id+"F0.wireOp",EDGE,"E915"),sQuery(id+"F0.wireOp",EDGE,"E919"),sQuery(id+"F0.wireOp",EDGE,"E922"),sQuery(id+"F0.wireOp",EDGE,"E923"),sQuery(id+"F0.wireOp",EDGE,"E924"),sQuery(id+"F0.wireOp",EDGE,"E925"),sQuery(id+"F0.wireOp",EDGE,"E926"),sQuery(id+"F0.wireOp",EDGE,"E927"),sQuery(id+"F0.wireOp",EDGE,"E928"),sQuery(id+"F0.wireOp",EDGE,"E929"),sQuery(id+"F0.wireOp",EDGE,"E930"),sQuery(id+"F0.wireOp",EDGE,"E931"),sQuery(id+"F0.wireOp",EDGE,"E932"),sQuery(id+"F0.wireOp",EDGE,"E934"),sQuery(id+"F0.wireOp",EDGE,"E942"),sQuery(id+"F0.wireOp",EDGE,"E946"),sQuery(id+"F0.wireOp",EDGE,"E950"),sQuery(id+"F0.wireOp",EDGE,"E954"),sQuery(id+"F0.wireOp",EDGE,"E958"),sQuery(id+"F0.wireOp",EDGE,"E962"),sQuery(id+"F0.wireOp",EDGE,"E966"),sQuery(id+"F0.wireOp",EDGE,"E970"),sQuery(id+"F0.wireOp",EDGE,"E974"),sQuery(id+"F0.wireOp",EDGE,"E978"),sQuery(id+"F0.wireOp",EDGE,"E981"),sQuery(id+"F0.wireOp",EDGE,"E983"),sQuery(id+"F0.wireOp",EDGE,"E984")])],"isStart":false});
            var sketch = newSketch(context, id + "F12", { "sketchPlane" : qUnion([Q0])});
            skCircle(sketch, "E1004", {"center": v(-23.45, 12) * mm, "radius": 3.25 * mm});
            skCircle(sketch, "E1005", {"center": v(-16.47, 12) * mm, "radius": 3.25 * mm});
            skLineSegment(sketch, "E1006", {"start": v(-23.45, 12) * mm, "end": v(-23.45, 15.25) * mm, "construction": true});
            skLineSegment(sketch, "E1007", {"start": v(-16.47, 12) * mm, "end": v(-16.47, 15.25) * mm, "construction": true});
            skLineSegment(sketch, "E1008", {"start": v(-23.45, 12) * mm, "end": v(-16.47, 12) * mm, "construction": true});
            skSolve(sketch);
        }
        {
            var Q0;
            Q0=makeQuery(id+"F12.imprint","IMPRINT",FACE,{"disambiguationData":[TD([[makeQuery(id+"F12.imprint","IMPRINT",EDGE,{"derivedFrom":sQuery(id+"F12.wireOp",EDGE,"E1005")}),1.0]])]});
            var Q1;
            Q1=makeQuery(id+"F12.imprint","IMPRINT",FACE,{"disambiguationData":[TD([[makeQuery(id+"F12.imprint","IMPRINT",EDGE,{"derivedFrom":sQuery(id+"F12.wireOp",EDGE,"E1004")}),1.0]])]});
            extrude(context, id + "F13", {"entities" : qUnion([Q0, Q1]), "operationType" : NewBodyOperationType.ADD, "depth" : 5.4 * mm});
        }
        {
            var Q0;
            Q0=sQuery(id+"F0.wireOp",EDGE,"E987");
            cPoint(context, id + "F14", {"entities" : qUnion([Q0]), "parameter" : 0.5});
        }
        {
            var Q0;
            Q0=qCreatedBy(makeId("Front.planeOp"),FACE);
            var Q1;
            Q1 = qCreatedBy(id + "F14" ,VERTEX);
            cPlane(context, id + "F15", {"entities" : qUnion([Q0, Q1]), "cplaneType" : CPlaneType.PLANE_POINT, "offset" : 25 * mm, "width" : 150 * mm, "height" : 150 * mm});
        }
        {
            var Q0;
            Q0=qCreatedBy(id+"F15.planeOp",FACE);
            var sketch = newSketch(context, id + "F16", { "sketchPlane" : qUnion([Q0])});
            skLineSegment(sketch, "E1009", {"start": v(-62.94, 16.4) * mm, "end": v(-62.94, -6.6) * mm});
            skLineSegment(sketch, "E1010", {"start": v(-62.94, -6.6) * mm, "end": v(66.06, -6.6) * mm});
            skLineSegment(sketch, "E1011", {"start": v(66.06, -6.6) * mm, "end": v(66.06, 16.4) * mm});
            skLineSegment(sketch, "E1012", {"start": v(66.06, 16.4) * mm, "end": v(23.06, -5) * mm});
            skLineSegment(sketch, "E1013", {"start": v(23.06, -5) * mm, "end": v(-19.94, -5) * mm});
            skLineSegment(sketch, "E1014", {"start": v(-19.94, -5) * mm, "end": v(-62.94, 16.4) * mm});
            skLineSegment(sketch, "E1015.0", {"start": v(23.24, -5.8) * mm, "end": v(-20.13, -5.8) * mm});
            skLineSegment(sketch, "E1015.1", {"start": v(-62.14, 15.1) * mm, "end": v(-62.14, -5.8) * mm});
            skLineSegment(sketch, "E1015.2", {"start": v(-62.14, -5.8) * mm, "end": v(65.26, -5.8) * mm});
            skLineSegment(sketch, "E1015.3", {"start": v(-20.13, -5.8) * mm, "end": v(-62.14, 15.1) * mm});
            skLineSegment(sketch, "E1015.4", {"start": v(65.26, -5.8) * mm, "end": v(65.26, 15.1) * mm});
            skLineSegment(sketch, "E1015.5", {"start": v(65.26, 15.1) * mm, "end": v(23.24, -5.8) * mm});
            skSolve(sketch);
        }
        {
            var Q0;
            Q0 = qSketchRegion(id + "F16", true);
            extrude(context, id + "F17", {"entities" : qUnion([Q0]), "endBound" : BoundingType.SYMMETRIC, "depth" : 100 * mm});
        }
        {
            var Q0;
            Q0=makeQuery(id+"F17.opExtrude","SWEPT_FACE",FACE,{"disambiguationData":[OSD([sQuery(id+"F16.wireOp",EDGE,"E1014")])]});
            var sketch = newSketch(context, id + "F18", { "sketchPlane" : qUnion([Q0])});
            skLineSegment(sketch, "E1016.bottom", {"start": v(-25.72, -32.5) * mm, "end": v(-39.9, -32.5) * mm});
            skLineSegment(sketch, "E1016.top", {"start": v(-25.72, 30) * mm, "end": v(-39.9, 30) * mm});
            skLineSegment(sketch, "E1016.left", {"start": v(-25.72, -32.5) * mm, "end": v(-25.72, 30) * mm});
            skLineSegment(sketch, "E1016.right", {"start": v(-39.9, -32.5) * mm, "end": v(-39.9, 30) * mm});
            skLineSegment(sketch, "E1017", {"start": v(-63.66, -1.26) * mm, "end": v(-39.9, -1.26) * mm, "construction": true});
            skSolve(sketch);
        }
        {
            var Q0;
            Q0=makeQuery(id+"F17.opExtrude","SWEPT_FACE",FACE,{"disambiguationData":[OSD([sQuery(id+"F16.wireOp",EDGE,"E1014")])]});
            var sketch = newSketch(context, id + "F19", { "sketchPlane" : qUnion([Q0])});
            skLineSegment(sketch, "E1018.bottom", {"start": v(-26.13, -32.76) * mm, "end": v(-40.13, -32.76) * mm});
            skLineSegment(sketch, "E1018.top", {"start": v(-26.13, 30.24) * mm, "end": v(-40.13, 30.24) * mm});
            skLineSegment(sketch, "E1018.left", {"start": v(-26.13, -32.76) * mm, "end": v(-26.13, 30.24) * mm});
            skLineSegment(sketch, "E1018.right", {"start": v(-40.13, -32.76) * mm, "end": v(-40.13, 30.24) * mm});
            skLineSegment(sketch, "E1019", {"start": v(-40.13, -1.26) * mm, "end": v(-63.66, -1.26) * mm, "construction": true});
            skLineSegment(sketch, "E1020.bottom", {"start": v(-40.13, 6.24) * mm, "end": v(-35.23, 6.24) * mm, "construction": true});
            skLineSegment(sketch, "E1020.top", {"start": v(-40.13, -8.76) * mm, "end": v(-35.23, -8.76) * mm, "construction": true});
            skLineSegment(sketch, "E1020.right", {"start": v(-35.23, 6.24) * mm, "end": v(-35.23, -8.76) * mm});
            skPoint(sketch, "E1020.middle", {"position": v(-40.13, -1.26) * mm});
            skPoint(sketch, "E1021.orphan", {"position": v(-45.03, 6.24) * mm});
            skPoint(sketch, "E1022.orphan", {"position": v(-45.03, -8.76) * mm});
            skLineSegment(sketch, "E1023", {"start": v(-35.23, -8.76) * mm, "end": v(-40.13, -9.76) * mm});
            skLineSegment(sketch, "E1024", {"start": v(-35.23, 6.24) * mm, "end": v(-40.13, 7.24) * mm});
            skSolve(sketch);
        }
        {
            var Q0;
            {var subQ1=sQuery(id+"F19.wireOp",EDGE,"E1018.bottom");Q0=makeQuery(id+"F19.imprint","IMPRINT",FACE,{"disambiguationData":[TD([[makeQuery(id+"F19.imprint","IMPRINT",EDGE,{"derivedFrom":subQ1}),-1.0]])]});}
            var Q1;
            {var subQ0=sQuery(id+"F19.wireOp",EDGE,"cvH0966M-vOD4-t3Ij-s306-ksNTmC8deJW0");Q1=makeQuery(id+"F19.imprint","IMPRINT",FACE,{"disambiguationData":[TD([[makeQuery(id+"F19.imprint","IMPRINT",EDGE,{"derivedFrom":subQ0}),1.0]])]});}
            var Q2;
            {var subQ0=sQuery(id+"F19.wireOp",EDGE,"clJaxFcV-2eD6-orOG-rZic-akz9M5EGohDm");Q2=makeQuery(id+"F19.imprint","IMPRINT",FACE,{"disambiguationData":[TD([[makeQuery(id+"F19.imprint","IMPRINT",EDGE,{"derivedFrom":subQ0}),1.0]])]});}
            var Q3;
            Q3=makeQuery(id+"F17.opExtrude","SWEPT_FACE",FACE,{"disambiguationData":[OSD([sQuery(id+"F16.wireOp",EDGE,"E1015.3")])]});
            extrude(context, id + "F20", {"entities" : qUnion([Q0, Q1, Q2]), "operationType" : NewBodyOperationType.REMOVE, "endBound" : BoundingType.UP_TO_SURFACE, "oppositeDirection" : true, "endBoundEntityFace" : qUnion([Q3]), "depth" : 25 * mm});
        }
        {
            var Q0;
            Q0=makeQuery(id+"F20.boolean.opBoolean","COPY",EDGE,{"derivedFrom":makeQuery(id+"F20.opExtrude","SWEPT_EDGE",EDGE,{"disambiguationData":[OSD([sQuery(id+"F19.wireOp",EDGE,"XZjFsrEt-XHdQ-qvoK-Gu2f-gOHsuDQ94MQY"),sQuery(id+"F19.wireOp",EDGE,"xD0UQtAa-FVft-0JcN-JoMk-WWRetgCgu4DL")])]})});
            var Q1;
            Q1=makeQuery(id+"F20.boolean.opBoolean","COPY",EDGE,{"derivedFrom":makeQuery(id+"F20.opExtrude","SWEPT_EDGE",EDGE,{"disambiguationData":[OSD([sQuery(id+"F19.wireOp",EDGE,"E1018.right"),sQuery(id+"F19.wireOp",EDGE,"cvH0966M-vOD4-t3Ij-s306-ksNTmC8deJW0")])]})});
            var Q2;
            Q2=makeQuery(id+"F20.boolean.opBoolean","COPY",EDGE,{"derivedFrom":makeQuery(id+"F20.opExtrude","SWEPT_EDGE",EDGE,{"disambiguationData":[OSD([sQuery(id+"F19.wireOp",EDGE,"XZjFsrEt-XHdQ-qvoK-Gu2f-gOHsuDQ94MQY"),sQuery(id+"F19.wireOp",EDGE,"xD0UQtAa-FVft-0JcN-JoMk-WWRetgCgu4DL")])]})});
            var Q3;
            Q3=makeQuery(id+"F20.boolean.opBoolean","COPY",EDGE,{"derivedFrom":makeQuery(id+"F20.opExtrude","SWEPT_EDGE",EDGE,{"disambiguationData":[OSD([sQuery(id+"F19.wireOp",EDGE,"olSYAtLZ-6eND-qpX7-nGr0-KxEVjvAU0XDS"),sQuery(id+"F19.wireOp",EDGE,"clJaxFcV-2eD6-orOG-rZic-akz9M5EGohDm")])]})});
            var Q4;
            Q4=makeQuery(id+"F20.boolean.opBoolean","COPY",EDGE,{"derivedFrom":makeQuery(id+"F20.opExtrude","SWEPT_EDGE",EDGE,{"disambiguationData":[OSD([sQuery(id+"F19.wireOp",EDGE,"cvH0966M-vOD4-t3Ij-s306-ksNTmC8deJW0"),sQuery(id+"F19.wireOp",EDGE,"olSYAtLZ-6eND-qpX7-nGr0-KxEVjvAU0XDS")])]})});
            var Q5;
            Q5=makeQuery(id+"F20.boolean.opBoolean","COPY",EDGE,{"derivedFrom":makeQuery(id+"F20.opExtrude","SWEPT_EDGE",EDGE,{"disambiguationData":[OSD([sQuery(id+"F19.wireOp",EDGE,"E1018.right"),sQuery(id+"F19.wireOp",EDGE,"cvH0966M-vOD4-t3Ij-s306-ksNTmC8deJW0")])]})});
            var Q6;
            Q6=makeQuery(id+"F20.boolean.opBoolean","COPY",EDGE,{"derivedFrom":makeQuery(id+"F20.opExtrude","SWEPT_EDGE",EDGE,{"disambiguationData":[OSD([sQuery(id+"F19.wireOp",EDGE,"E1020.right"),sQuery(id+"F19.wireOp",EDGE,"E1023")])]})});
            var Q7;
            Q7=makeQuery(id+"F20.boolean.opBoolean","COPY",EDGE,{"derivedFrom":makeQuery(id+"F20.opExtrude","SWEPT_EDGE",EDGE,{"disambiguationData":[OSD([sQuery(id+"F19.wireOp",EDGE,"E1020.right"),sQuery(id+"F19.wireOp",EDGE,"E1024")])]})});
            fillet(context, id + "F21", {"entities" : qUnion([Q0, Q1, Q2, Q3, Q4, Q5, Q6, Q7]), "radius" : 1.5 * mm, "tangentPropagation" : true, "allowEdgeOverflow" : false});
        }
        {
            var Q0;
            Q0=makeQuery(id+"F17.opExtrude","SWEPT_FACE",FACE,{"disambiguationData":[OSD([sQuery(id+"F16.wireOp",EDGE,"E1012")])]});
            var sketch = newSketch(context, id + "F22", { "sketchPlane" : qUnion([Q0])});
            skLineSegment(sketch, "E1025.bottom", {"start": v(40.91, 30.24) * mm, "end": v(28.91, 30.24) * mm});
            skLineSegment(sketch, "E1025.top", {"start": v(40.91, -32.76) * mm, "end": v(28.91, -32.76) * mm});
            skLineSegment(sketch, "E1025.left", {"start": v(40.91, 30.24) * mm, "end": v(40.91, -32.76) * mm});
            skLineSegment(sketch, "E1025.right", {"start": v(28.91, 30.24) * mm, "end": v(28.91, -32.76) * mm});
            skLineSegment(sketch, "E1026", {"start": v(40.91, -1.26) * mm, "end": v(28.91, -1.26) * mm, "construction": true});
            skLineSegment(sketch, "E1027.bottom", {"start": v(40.91, -8.76) * mm, "end": v(34.91, -8.76) * mm});
            skLineSegment(sketch, "E1027.top", {"start": v(40.91, 6.24) * mm, "end": v(34.91, 6.24) * mm});
            skLineSegment(sketch, "E1027.right", {"start": v(34.91, -8.76) * mm, "end": v(34.91, 6.24) * mm});
            skPoint(sketch, "E1027.middle", {"position": v(40.91, -1.26) * mm});
            skLineSegment(sketch, "E1028", {"start": v(34.91, 6.24) * mm, "end": v(40.91, 7.24) * mm});
            skLineSegment(sketch, "E1029", {"start": v(34.91, -8.76) * mm, "end": v(40.91, -9.76) * mm});
            skPoint(sketch, "E1027.left.end.orphan", {"position": v(46.91, 6.24) * mm});
            skPoint(sketch, "E1030.orphan", {"position": v(46.91, -8.76) * mm});
            skSolve(sketch);
        }
        {
            var Q0;
            {var subQ3=sQuery(id+"F22.wireOp",EDGE,"E1025.bottom");Q0=makeQuery(id+"F22.imprint","IMPRINT",FACE,{"disambiguationData":[TD([[makeQuery(id+"F22.imprint","IMPRINT",EDGE,{"derivedFrom":subQ3}),1.0]])]});}
            var Q1;
            Q1=makeQuery(id+"F17.opExtrude","SWEPT_FACE",FACE,{"disambiguationData":[OSD([sQuery(id+"F16.wireOp",EDGE,"E1013")])]});
            extrude(context, id + "F23", {"entities" : qUnion([Q0]), "operationType" : NewBodyOperationType.REMOVE, "endBound" : BoundingType.UP_TO_SURFACE, "oppositeDirection" : true, "endBoundEntityFace" : qUnion([Q1]), "depth" : 25 * mm});
        }
        {
            var Q0;
            Q0=makeQuery(id+"F23.boolean.opBoolean","COPY",EDGE,{"derivedFrom":makeQuery(id+"F23.opExtrude","SWEPT_EDGE",EDGE,{"disambiguationData":[OSD([sQuery(id+"F22.wireOp",EDGE,"E1025.top"),sQuery(id+"F22.wireOp",EDGE,"E1025.left")])]})});
            chamfer(context, id + "F24", {"entities" : qUnion([Q0]), "width" : 8 * mm, "tangentPropagation" : true});
        }
        {
            var Q0;
            Q0=makeQuery(id+"F17.opExtrude","SWEPT_FACE",FACE,{"disambiguationData":[OSD([sQuery(id+"F16.wireOp",EDGE,"E1012")])]});
            var sketch = newSketch(context, id + "F25", { "sketchPlane" : qUnion([Q0])});
            skCircle(sketch, "E1031", {"center": v(40.91, 30.24) * mm, "radius": 1.5 * mm});
            skSolve(sketch);
        }
        {
            var Q0;
            Q0=makeQuery(id+"F23.boolean.opBoolean","COPY",EDGE,{"derivedFrom":makeQuery(id+"F23.opExtrude","SWEPT_EDGE",EDGE,{"disambiguationData":[OSD([sQuery(id+"F22.wireOp",EDGE,"E1025.bottom"),sQuery(id+"F22.wireOp",EDGE,"E1025.left")])]})});
            var Q1;
            Q1=makeQuery(id+"F20.boolean.opBoolean","COPY",EDGE,{"derivedFrom":makeQuery(id+"F20.opExtrude","SWEPT_EDGE",EDGE,{"disambiguationData":[OSD([sQuery(id+"F19.wireOp",EDGE,"E1018.top"),sQuery(id+"F19.wireOp",EDGE,"E1018.right"),sQuery(id+"F19.wireOp",EDGE,"zIPZ5uTG-OMLx-eea0-zTnT-lUfkHDVFsSs8")])]})});
            var Q2;
            Q2=makeQuery(id+"F20.boolean.opBoolean","COPY",EDGE,{"derivedFrom":makeQuery(id+"F20.opExtrude","SWEPT_EDGE",EDGE,{"disambiguationData":[OSD([sQuery(id+"F19.wireOp",EDGE,"E1018.bottom"),sQuery(id+"F19.wireOp",EDGE,"E1018.right")])]})});
            var Q3;
            {var subQ0=sQuery(id+"F22.wireOp",EDGE,"E1025.left");Q3=makeQuery(id+"F24.opChamfer","BLEND_EDGE",EDGE,{"blendedFrom":[makeQuery(id+"F23.boolean.opBoolean","COPY",EDGE,{"derivedFrom":makeQuery(id+"F23.opExtrude","SWEPT_EDGE",EDGE,{"disambiguationData":[OSD([sQuery(id+"F22.wireOp",EDGE,"E1025.top"),subQ0])]})}),makeQuery(id+"F23.boolean.opBoolean","COPY",FACE,{"derivedFrom":makeQuery(id+"F23.opExtrude","SWEPT_FACE",FACE,{"disambiguationData":[OSD([subQ0])]})})],"blendedInto":[makeQuery(id+"F23.boolean.opBoolean","COPY",FACE,{"derivedFrom":makeQuery(id+"F23.opExtrude","SWEPT_FACE",FACE,{"disambiguationData":[OSD([subQ0])]})})]});}
            var Q4;
            {var subQ0=sQuery(id+"F22.wireOp",EDGE,"E1025.top");Q4=makeQuery(id+"F24.opChamfer","BLEND_EDGE",EDGE,{"blendedFrom":[makeQuery(id+"F23.boolean.opBoolean","COPY",EDGE,{"derivedFrom":makeQuery(id+"F23.opExtrude","SWEPT_EDGE",EDGE,{"disambiguationData":[OSD([subQ0,sQuery(id+"F22.wireOp",EDGE,"E1025.left")])]})}),makeQuery(id+"F23.boolean.opBoolean","COPY",FACE,{"derivedFrom":makeQuery(id+"F23.opExtrude","SWEPT_FACE",FACE,{"disambiguationData":[OSD([subQ0])]})})],"blendedInto":[makeQuery(id+"F23.boolean.opBoolean","COPY",FACE,{"derivedFrom":makeQuery(id+"F23.opExtrude","SWEPT_FACE",FACE,{"disambiguationData":[OSD([subQ0])]})})]});}
            var Q5;
            Q5=makeQuery(id+"F23.boolean.opBoolean","COPY",EDGE,{"derivedFrom":makeQuery(id+"F23.opExtrude","SWEPT_EDGE",EDGE,{"disambiguationData":[OSD([sQuery(id+"F22.wireOp",EDGE,"E1025.left"),sQuery(id+"F22.wireOp",EDGE,"E1029")])]})});
            var Q6;
            Q6=makeQuery(id+"F23.boolean.opBoolean","COPY",EDGE,{"derivedFrom":makeQuery(id+"F23.opExtrude","SWEPT_EDGE",EDGE,{"disambiguationData":[OSD([sQuery(id+"F22.wireOp",EDGE,"E1027.bottom"),sQuery(id+"F22.wireOp",EDGE,"E1027.right"),sQuery(id+"F22.wireOp",EDGE,"E1029")])]})});
            var Q7;
            Q7=makeQuery(id+"F23.boolean.opBoolean","COPY",EDGE,{"derivedFrom":makeQuery(id+"F23.opExtrude","SWEPT_EDGE",EDGE,{"disambiguationData":[OSD([sQuery(id+"F22.wireOp",EDGE,"E1027.top"),sQuery(id+"F22.wireOp",EDGE,"E1027.right"),sQuery(id+"F22.wireOp",EDGE,"E1028")])]})});
            var Q8;
            Q8=makeQuery(id+"F23.boolean.opBoolean","COPY",EDGE,{"derivedFrom":makeQuery(id+"F23.opExtrude","SWEPT_EDGE",EDGE,{"disambiguationData":[OSD([sQuery(id+"F22.wireOp",EDGE,"E1025.left"),sQuery(id+"F22.wireOp",EDGE,"E1028")])]})});
            fillet(context, id + "F26", {"entities" : qUnion([Q0, Q1, Q2, Q3, Q4, Q5, Q6, Q7, Q8]), "radius" : 1.5 * mm, "tangentPropagation" : true, "allowEdgeOverflow" : false});
        }
    });
